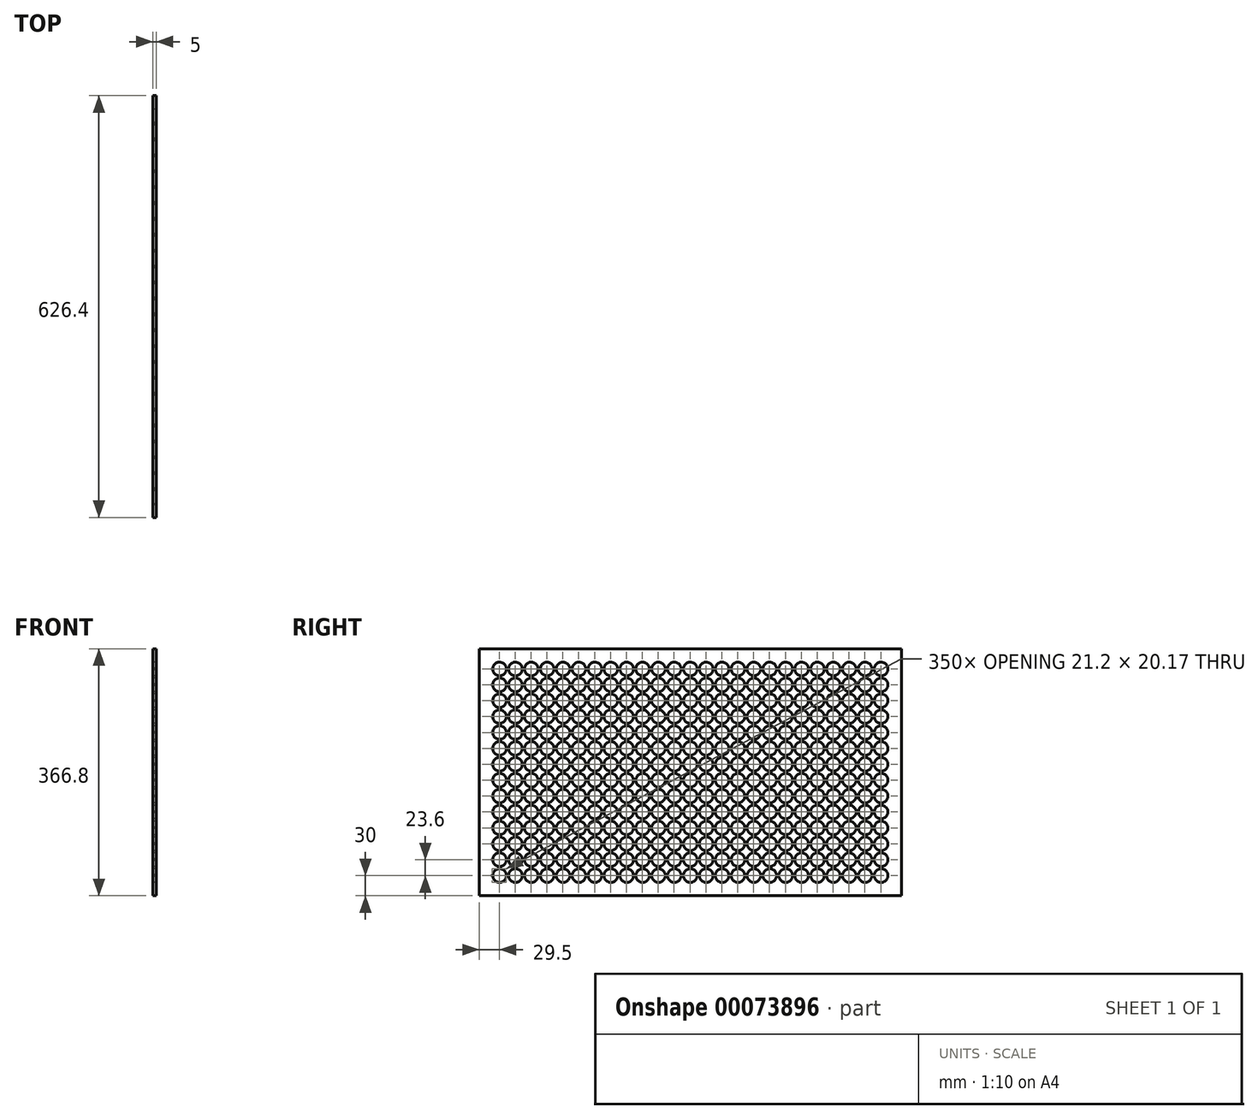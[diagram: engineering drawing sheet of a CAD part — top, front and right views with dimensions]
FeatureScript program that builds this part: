
annotation { "Feature Type Name" : "Feature", "Feature Type Description" : "" }
export const myFeature = defineFeature(function(context is Context, id is Id, definition is map)
    precondition{}
    {
        {
            var Q0;
            Q0=qCreatedBy(makeId("Right.planeOp"),FACE);
            var sketch = newSketch(context, id + "F0", { "sketchPlane" : qUnion([Q0])});
            skArc(sketch, "E0", {"start": v(-10.04, -1.1) * mm, "mid": v(10.1, 0) * mm, "end": v(-10.04, 1.1) * mm});
            skLineSegment(sketch, "E1.bottom", {"start": v(-30, 30) * mm, "end": v(596.4, 30) * mm});
            skLineSegment(sketch, "E1.top", {"start": v(-30, -336.8) * mm, "end": v(596.4, -336.8) * mm});
            skLineSegment(sketch, "E1.left", {"start": v(-30, 30) * mm, "end": v(-30, -336.8) * mm});
            skLineSegment(sketch, "E1.right", {"start": v(596.4, 30) * mm, "end": v(596.4, -336.8) * mm});
            skLineSegment(sketch, "E2", {"start": v(-10.04, -1.1) * mm, "end": v(-11.1, -1.1) * mm});
            skLineSegment(sketch, "E3", {"start": v(-10.04, 1.1) * mm, "end": v(-11.1, 1.1) * mm});
            skLineSegment(sketch, "E4", {"start": v(-11.1, 1.1) * mm, "end": v(-11.1, -1.1) * mm});
            skCircle(sketch, "E5", {"center": v(0, 0) * mm, "radius": 11.65 * mm, "construction": true});
            skArc(sketch, "E6.0.1.0", {"start": v(-10.04, -24.7) * mm, "mid": v(10.1, -23.6) * mm, "end": v(-10.04, -22.5) * mm});
            skLineSegment(sketch, "E6.0.1.1", {"start": v(-10.04, -24.7) * mm, "end": v(-11.1, -24.7) * mm});
            skLineSegment(sketch, "E6.0.1.2", {"start": v(-10.04, -22.5) * mm, "end": v(-11.1, -22.5) * mm});
            skLineSegment(sketch, "E6.0.1.3", {"start": v(-11.1, -22.5) * mm, "end": v(-11.1, -24.7) * mm});
            skArc(sketch, "E6.0.2.0", {"start": v(-10.04, -48.3) * mm, "mid": v(10.1, -47.2) * mm, "end": v(-10.04, -46.1) * mm});
            skLineSegment(sketch, "E6.0.2.1", {"start": v(-10.04, -48.3) * mm, "end": v(-11.1, -48.3) * mm});
            skLineSegment(sketch, "E6.0.2.2", {"start": v(-10.04, -46.1) * mm, "end": v(-11.1, -46.1) * mm});
            skLineSegment(sketch, "E6.0.2.3", {"start": v(-11.1, -46.1) * mm, "end": v(-11.1, -48.3) * mm});
            skArc(sketch, "E6.0.3.0", {"start": v(-10.04, -71.9) * mm, "mid": v(10.1, -70.8) * mm, "end": v(-10.04, -69.7) * mm});
            skLineSegment(sketch, "E6.0.3.1", {"start": v(-10.04, -71.9) * mm, "end": v(-11.1, -71.9) * mm});
            skLineSegment(sketch, "E6.0.3.2", {"start": v(-10.04, -69.7) * mm, "end": v(-11.1, -69.7) * mm});
            skLineSegment(sketch, "E6.0.3.3", {"start": v(-11.1, -69.7) * mm, "end": v(-11.1, -71.9) * mm});
            skArc(sketch, "E6.0.4.0", {"start": v(-10.04, -95.5) * mm, "mid": v(10.1, -94.4) * mm, "end": v(-10.04, -93.3) * mm});
            skLineSegment(sketch, "E6.0.4.1", {"start": v(-10.04, -95.5) * mm, "end": v(-11.1, -95.5) * mm});
            skLineSegment(sketch, "E6.0.4.2", {"start": v(-10.04, -93.3) * mm, "end": v(-11.1, -93.3) * mm});
            skLineSegment(sketch, "E6.0.4.3", {"start": v(-11.1, -93.3) * mm, "end": v(-11.1, -95.5) * mm});
            skArc(sketch, "E6.0.5.0", {"start": v(-10.04, -119.1) * mm, "mid": v(10.1, -118) * mm, "end": v(-10.04, -116.9) * mm});
            skLineSegment(sketch, "E6.0.5.1", {"start": v(-10.04, -119.1) * mm, "end": v(-11.1, -119.1) * mm});
            skLineSegment(sketch, "E6.0.5.2", {"start": v(-10.04, -116.9) * mm, "end": v(-11.1, -116.9) * mm});
            skLineSegment(sketch, "E6.0.5.3", {"start": v(-11.1, -116.9) * mm, "end": v(-11.1, -119.1) * mm});
            skArc(sketch, "E6.0.6.0", {"start": v(-10.04, -142.7) * mm, "mid": v(10.1, -141.6) * mm, "end": v(-10.04, -140.5) * mm});
            skLineSegment(sketch, "E6.0.6.1", {"start": v(-10.04, -142.7) * mm, "end": v(-11.1, -142.7) * mm});
            skLineSegment(sketch, "E6.0.6.2", {"start": v(-10.04, -140.5) * mm, "end": v(-11.1, -140.5) * mm});
            skLineSegment(sketch, "E6.0.6.3", {"start": v(-11.1, -140.5) * mm, "end": v(-11.1, -142.7) * mm});
            skArc(sketch, "E6.0.7.0", {"start": v(-10.04, -166.3) * mm, "mid": v(10.1, -165.2) * mm, "end": v(-10.04, -164.1) * mm});
            skLineSegment(sketch, "E6.0.7.1", {"start": v(-10.04, -166.3) * mm, "end": v(-11.1, -166.3) * mm});
            skLineSegment(sketch, "E6.0.7.2", {"start": v(-10.04, -164.1) * mm, "end": v(-11.1, -164.1) * mm});
            skLineSegment(sketch, "E6.0.7.3", {"start": v(-11.1, -164.1) * mm, "end": v(-11.1, -166.3) * mm});
            skArc(sketch, "E6.0.8.0", {"start": v(-10.04, -189.9) * mm, "mid": v(10.1, -188.8) * mm, "end": v(-10.04, -187.7) * mm});
            skLineSegment(sketch, "E6.0.8.1", {"start": v(-10.04, -189.9) * mm, "end": v(-11.1, -189.9) * mm});
            skLineSegment(sketch, "E6.0.8.2", {"start": v(-10.04, -187.7) * mm, "end": v(-11.1, -187.7) * mm});
            skLineSegment(sketch, "E6.0.8.3", {"start": v(-11.1, -187.7) * mm, "end": v(-11.1, -189.9) * mm});
            skArc(sketch, "E6.0.9.0", {"start": v(-10.04, -213.5) * mm, "mid": v(10.1, -212.4) * mm, "end": v(-10.04, -211.3) * mm});
            skLineSegment(sketch, "E6.0.9.1", {"start": v(-10.04, -213.5) * mm, "end": v(-11.1, -213.5) * mm});
            skLineSegment(sketch, "E6.0.9.2", {"start": v(-10.04, -211.3) * mm, "end": v(-11.1, -211.3) * mm});
            skLineSegment(sketch, "E6.0.9.3", {"start": v(-11.1, -211.3) * mm, "end": v(-11.1, -213.5) * mm});
            skArc(sketch, "E6.0.10.0", {"start": v(-10.04, -237.1) * mm, "mid": v(10.1, -236) * mm, "end": v(-10.04, -234.9) * mm});
            skLineSegment(sketch, "E6.0.10.1", {"start": v(-10.04, -237.1) * mm, "end": v(-11.1, -237.1) * mm});
            skLineSegment(sketch, "E6.0.10.2", {"start": v(-10.04, -234.9) * mm, "end": v(-11.1, -234.9) * mm});
            skLineSegment(sketch, "E6.0.10.3", {"start": v(-11.1, -234.9) * mm, "end": v(-11.1, -237.1) * mm});
            skArc(sketch, "E6.0.11.0", {"start": v(-10.04, -260.7) * mm, "mid": v(10.1, -259.6) * mm, "end": v(-10.04, -258.5) * mm});
            skLineSegment(sketch, "E6.0.11.1", {"start": v(-10.04, -260.7) * mm, "end": v(-11.1, -260.7) * mm});
            skLineSegment(sketch, "E6.0.11.2", {"start": v(-10.04, -258.5) * mm, "end": v(-11.1, -258.5) * mm});
            skLineSegment(sketch, "E6.0.11.3", {"start": v(-11.1, -258.5) * mm, "end": v(-11.1, -260.7) * mm});
            skArc(sketch, "E6.0.12.0", {"start": v(-10.04, -284.3) * mm, "mid": v(10.1, -283.2) * mm, "end": v(-10.04, -282.1) * mm});
            skLineSegment(sketch, "E6.0.12.1", {"start": v(-10.04, -284.3) * mm, "end": v(-11.1, -284.3) * mm});
            skLineSegment(sketch, "E6.0.12.2", {"start": v(-10.04, -282.1) * mm, "end": v(-11.1, -282.1) * mm});
            skLineSegment(sketch, "E6.0.12.3", {"start": v(-11.1, -282.1) * mm, "end": v(-11.1, -284.3) * mm});
            skArc(sketch, "E6.0.13.0", {"start": v(-10.04, -307.9) * mm, "mid": v(10.1, -306.8) * mm, "end": v(-10.04, -305.7) * mm});
            skLineSegment(sketch, "E6.0.13.1", {"start": v(-10.04, -307.9) * mm, "end": v(-11.1, -307.9) * mm});
            skLineSegment(sketch, "E6.0.13.2", {"start": v(-10.04, -305.7) * mm, "end": v(-11.1, -305.7) * mm});
            skLineSegment(sketch, "E6.0.13.3", {"start": v(-11.1, -305.7) * mm, "end": v(-11.1, -307.9) * mm});
            skArc(sketch, "E6.1.0.0", {"start": v(13.56, -1.1) * mm, "mid": v(33.7, 0) * mm, "end": v(13.56, 1.1) * mm});
            skLineSegment(sketch, "E6.1.0.1", {"start": v(13.56, -1.1) * mm, "end": v(12.5, -1.1) * mm});
            skLineSegment(sketch, "E6.1.0.2", {"start": v(13.56, 1.1) * mm, "end": v(12.5, 1.1) * mm});
            skLineSegment(sketch, "E6.1.0.3", {"start": v(12.5, 1.1) * mm, "end": v(12.5, -1.1) * mm});
            skArc(sketch, "E6.1.1.0", {"start": v(13.56, -24.7) * mm, "mid": v(33.7, -23.6) * mm, "end": v(13.56, -22.5) * mm});
            skLineSegment(sketch, "E6.1.1.1", {"start": v(13.56, -24.7) * mm, "end": v(12.5, -24.7) * mm});
            skLineSegment(sketch, "E6.1.1.2", {"start": v(13.56, -22.5) * mm, "end": v(12.5, -22.5) * mm});
            skLineSegment(sketch, "E6.1.1.3", {"start": v(12.5, -22.5) * mm, "end": v(12.5, -24.7) * mm});
            skArc(sketch, "E6.1.2.0", {"start": v(13.56, -48.3) * mm, "mid": v(33.7, -47.2) * mm, "end": v(13.56, -46.1) * mm});
            skLineSegment(sketch, "E6.1.2.1", {"start": v(13.56, -48.3) * mm, "end": v(12.5, -48.3) * mm});
            skLineSegment(sketch, "E6.1.2.2", {"start": v(13.56, -46.1) * mm, "end": v(12.5, -46.1) * mm});
            skLineSegment(sketch, "E6.1.2.3", {"start": v(12.5, -46.1) * mm, "end": v(12.5, -48.3) * mm});
            skArc(sketch, "E6.1.3.0", {"start": v(13.56, -71.9) * mm, "mid": v(33.7, -70.8) * mm, "end": v(13.56, -69.7) * mm});
            skLineSegment(sketch, "E6.1.3.1", {"start": v(13.56, -71.9) * mm, "end": v(12.5, -71.9) * mm});
            skLineSegment(sketch, "E6.1.3.2", {"start": v(13.56, -69.7) * mm, "end": v(12.5, -69.7) * mm});
            skLineSegment(sketch, "E6.1.3.3", {"start": v(12.5, -69.7) * mm, "end": v(12.5, -71.9) * mm});
            skArc(sketch, "E6.1.4.0", {"start": v(13.56, -95.5) * mm, "mid": v(33.7, -94.4) * mm, "end": v(13.56, -93.3) * mm});
            skLineSegment(sketch, "E6.1.4.1", {"start": v(13.56, -95.5) * mm, "end": v(12.5, -95.5) * mm});
            skLineSegment(sketch, "E6.1.4.2", {"start": v(13.56, -93.3) * mm, "end": v(12.5, -93.3) * mm});
            skLineSegment(sketch, "E6.1.4.3", {"start": v(12.5, -93.3) * mm, "end": v(12.5, -95.5) * mm});
            skArc(sketch, "E6.1.5.0", {"start": v(13.56, -119.1) * mm, "mid": v(33.7, -118) * mm, "end": v(13.56, -116.9) * mm});
            skLineSegment(sketch, "E6.1.5.1", {"start": v(13.56, -119.1) * mm, "end": v(12.5, -119.1) * mm});
            skLineSegment(sketch, "E6.1.5.2", {"start": v(13.56, -116.9) * mm, "end": v(12.5, -116.9) * mm});
            skLineSegment(sketch, "E6.1.5.3", {"start": v(12.5, -116.9) * mm, "end": v(12.5, -119.1) * mm});
            skArc(sketch, "E6.1.6.0", {"start": v(13.56, -142.7) * mm, "mid": v(33.7, -141.6) * mm, "end": v(13.56, -140.5) * mm});
            skLineSegment(sketch, "E6.1.6.1", {"start": v(13.56, -142.7) * mm, "end": v(12.5, -142.7) * mm});
            skLineSegment(sketch, "E6.1.6.2", {"start": v(13.56, -140.5) * mm, "end": v(12.5, -140.5) * mm});
            skLineSegment(sketch, "E6.1.6.3", {"start": v(12.5, -140.5) * mm, "end": v(12.5, -142.7) * mm});
            skArc(sketch, "E6.1.7.0", {"start": v(13.56, -166.3) * mm, "mid": v(33.7, -165.2) * mm, "end": v(13.56, -164.1) * mm});
            skLineSegment(sketch, "E6.1.7.1", {"start": v(13.56, -166.3) * mm, "end": v(12.5, -166.3) * mm});
            skLineSegment(sketch, "E6.1.7.2", {"start": v(13.56, -164.1) * mm, "end": v(12.5, -164.1) * mm});
            skLineSegment(sketch, "E6.1.7.3", {"start": v(12.5, -164.1) * mm, "end": v(12.5, -166.3) * mm});
            skArc(sketch, "E6.1.8.0", {"start": v(13.56, -189.9) * mm, "mid": v(33.7, -188.8) * mm, "end": v(13.56, -187.7) * mm});
            skLineSegment(sketch, "E6.1.8.1", {"start": v(13.56, -189.9) * mm, "end": v(12.5, -189.9) * mm});
            skLineSegment(sketch, "E6.1.8.2", {"start": v(13.56, -187.7) * mm, "end": v(12.5, -187.7) * mm});
            skLineSegment(sketch, "E6.1.8.3", {"start": v(12.5, -187.7) * mm, "end": v(12.5, -189.9) * mm});
            skArc(sketch, "E6.1.9.0", {"start": v(13.56, -213.5) * mm, "mid": v(33.7, -212.4) * mm, "end": v(13.56, -211.3) * mm});
            skLineSegment(sketch, "E6.1.9.1", {"start": v(13.56, -213.5) * mm, "end": v(12.5, -213.5) * mm});
            skLineSegment(sketch, "E6.1.9.2", {"start": v(13.56, -211.3) * mm, "end": v(12.5, -211.3) * mm});
            skLineSegment(sketch, "E6.1.9.3", {"start": v(12.5, -211.3) * mm, "end": v(12.5, -213.5) * mm});
            skArc(sketch, "E6.1.10.0", {"start": v(13.56, -237.1) * mm, "mid": v(33.7, -236) * mm, "end": v(13.56, -234.9) * mm});
            skLineSegment(sketch, "E6.1.10.1", {"start": v(13.56, -237.1) * mm, "end": v(12.5, -237.1) * mm});
            skLineSegment(sketch, "E6.1.10.2", {"start": v(13.56, -234.9) * mm, "end": v(12.5, -234.9) * mm});
            skLineSegment(sketch, "E6.1.10.3", {"start": v(12.5, -234.9) * mm, "end": v(12.5, -237.1) * mm});
            skArc(sketch, "E6.1.11.0", {"start": v(13.56, -260.7) * mm, "mid": v(33.7, -259.6) * mm, "end": v(13.56, -258.5) * mm});
            skLineSegment(sketch, "E6.1.11.1", {"start": v(13.56, -260.7) * mm, "end": v(12.5, -260.7) * mm});
            skLineSegment(sketch, "E6.1.11.2", {"start": v(13.56, -258.5) * mm, "end": v(12.5, -258.5) * mm});
            skLineSegment(sketch, "E6.1.11.3", {"start": v(12.5, -258.5) * mm, "end": v(12.5, -260.7) * mm});
            skArc(sketch, "E6.1.12.0", {"start": v(13.56, -284.3) * mm, "mid": v(33.7, -283.2) * mm, "end": v(13.56, -282.1) * mm});
            skLineSegment(sketch, "E6.1.12.1", {"start": v(13.56, -284.3) * mm, "end": v(12.5, -284.3) * mm});
            skLineSegment(sketch, "E6.1.12.2", {"start": v(13.56, -282.1) * mm, "end": v(12.5, -282.1) * mm});
            skLineSegment(sketch, "E6.1.12.3", {"start": v(12.5, -282.1) * mm, "end": v(12.5, -284.3) * mm});
            skArc(sketch, "E6.1.13.0", {"start": v(13.56, -307.9) * mm, "mid": v(33.7, -306.8) * mm, "end": v(13.56, -305.7) * mm});
            skLineSegment(sketch, "E6.1.13.1", {"start": v(13.56, -307.9) * mm, "end": v(12.5, -307.9) * mm});
            skLineSegment(sketch, "E6.1.13.2", {"start": v(13.56, -305.7) * mm, "end": v(12.5, -305.7) * mm});
            skLineSegment(sketch, "E6.1.13.3", {"start": v(12.5, -305.7) * mm, "end": v(12.5, -307.9) * mm});
            skArc(sketch, "E6.2.0.0", {"start": v(37.16, -1.1) * mm, "mid": v(57.3, 0) * mm, "end": v(37.16, 1.1) * mm});
            skLineSegment(sketch, "E6.2.0.1", {"start": v(37.16, -1.1) * mm, "end": v(36.1, -1.1) * mm});
            skLineSegment(sketch, "E6.2.0.2", {"start": v(37.16, 1.1) * mm, "end": v(36.1, 1.1) * mm});
            skLineSegment(sketch, "E6.2.0.3", {"start": v(36.1, 1.1) * mm, "end": v(36.1, -1.1) * mm});
            skArc(sketch, "E6.2.1.0", {"start": v(37.16, -24.7) * mm, "mid": v(57.3, -23.6) * mm, "end": v(37.16, -22.5) * mm});
            skLineSegment(sketch, "E6.2.1.1", {"start": v(37.16, -24.7) * mm, "end": v(36.1, -24.7) * mm});
            skLineSegment(sketch, "E6.2.1.2", {"start": v(37.16, -22.5) * mm, "end": v(36.1, -22.5) * mm});
            skLineSegment(sketch, "E6.2.1.3", {"start": v(36.1, -22.5) * mm, "end": v(36.1, -24.7) * mm});
            skArc(sketch, "E6.2.2.0", {"start": v(37.16, -48.3) * mm, "mid": v(57.3, -47.2) * mm, "end": v(37.16, -46.1) * mm});
            skLineSegment(sketch, "E6.2.2.1", {"start": v(37.16, -48.3) * mm, "end": v(36.1, -48.3) * mm});
            skLineSegment(sketch, "E6.2.2.2", {"start": v(37.16, -46.1) * mm, "end": v(36.1, -46.1) * mm});
            skLineSegment(sketch, "E6.2.2.3", {"start": v(36.1, -46.1) * mm, "end": v(36.1, -48.3) * mm});
            skArc(sketch, "E6.2.3.0", {"start": v(37.16, -71.9) * mm, "mid": v(57.3, -70.8) * mm, "end": v(37.16, -69.7) * mm});
            skLineSegment(sketch, "E6.2.3.1", {"start": v(37.16, -71.9) * mm, "end": v(36.1, -71.9) * mm});
            skLineSegment(sketch, "E6.2.3.2", {"start": v(37.16, -69.7) * mm, "end": v(36.1, -69.7) * mm});
            skLineSegment(sketch, "E6.2.3.3", {"start": v(36.1, -69.7) * mm, "end": v(36.1, -71.9) * mm});
            skArc(sketch, "E6.2.4.0", {"start": v(37.16, -95.5) * mm, "mid": v(57.3, -94.4) * mm, "end": v(37.16, -93.3) * mm});
            skLineSegment(sketch, "E6.2.4.1", {"start": v(37.16, -95.5) * mm, "end": v(36.1, -95.5) * mm});
            skLineSegment(sketch, "E6.2.4.2", {"start": v(37.16, -93.3) * mm, "end": v(36.1, -93.3) * mm});
            skLineSegment(sketch, "E6.2.4.3", {"start": v(36.1, -93.3) * mm, "end": v(36.1, -95.5) * mm});
            skArc(sketch, "E6.2.5.0", {"start": v(37.16, -119.1) * mm, "mid": v(57.3, -118) * mm, "end": v(37.16, -116.9) * mm});
            skLineSegment(sketch, "E6.2.5.1", {"start": v(37.16, -119.1) * mm, "end": v(36.1, -119.1) * mm});
            skLineSegment(sketch, "E6.2.5.2", {"start": v(37.16, -116.9) * mm, "end": v(36.1, -116.9) * mm});
            skLineSegment(sketch, "E6.2.5.3", {"start": v(36.1, -116.9) * mm, "end": v(36.1, -119.1) * mm});
            skArc(sketch, "E6.2.6.0", {"start": v(37.16, -142.7) * mm, "mid": v(57.3, -141.6) * mm, "end": v(37.16, -140.5) * mm});
            skLineSegment(sketch, "E6.2.6.1", {"start": v(37.16, -142.7) * mm, "end": v(36.1, -142.7) * mm});
            skLineSegment(sketch, "E6.2.6.2", {"start": v(37.16, -140.5) * mm, "end": v(36.1, -140.5) * mm});
            skLineSegment(sketch, "E6.2.6.3", {"start": v(36.1, -140.5) * mm, "end": v(36.1, -142.7) * mm});
            skArc(sketch, "E6.2.7.0", {"start": v(37.16, -166.3) * mm, "mid": v(57.3, -165.2) * mm, "end": v(37.16, -164.1) * mm});
            skLineSegment(sketch, "E6.2.7.1", {"start": v(37.16, -166.3) * mm, "end": v(36.1, -166.3) * mm});
            skLineSegment(sketch, "E6.2.7.2", {"start": v(37.16, -164.1) * mm, "end": v(36.1, -164.1) * mm});
            skLineSegment(sketch, "E6.2.7.3", {"start": v(36.1, -164.1) * mm, "end": v(36.1, -166.3) * mm});
            skArc(sketch, "E6.2.8.0", {"start": v(37.16, -189.9) * mm, "mid": v(57.3, -188.8) * mm, "end": v(37.16, -187.7) * mm});
            skLineSegment(sketch, "E6.2.8.1", {"start": v(37.16, -189.9) * mm, "end": v(36.1, -189.9) * mm});
            skLineSegment(sketch, "E6.2.8.2", {"start": v(37.16, -187.7) * mm, "end": v(36.1, -187.7) * mm});
            skLineSegment(sketch, "E6.2.8.3", {"start": v(36.1, -187.7) * mm, "end": v(36.1, -189.9) * mm});
            skArc(sketch, "E6.2.9.0", {"start": v(37.16, -213.5) * mm, "mid": v(57.3, -212.4) * mm, "end": v(37.16, -211.3) * mm});
            skLineSegment(sketch, "E6.2.9.1", {"start": v(37.16, -213.5) * mm, "end": v(36.1, -213.5) * mm});
            skLineSegment(sketch, "E6.2.9.2", {"start": v(37.16, -211.3) * mm, "end": v(36.1, -211.3) * mm});
            skLineSegment(sketch, "E6.2.9.3", {"start": v(36.1, -211.3) * mm, "end": v(36.1, -213.5) * mm});
            skArc(sketch, "E6.2.10.0", {"start": v(37.16, -237.1) * mm, "mid": v(57.3, -236) * mm, "end": v(37.16, -234.9) * mm});
            skLineSegment(sketch, "E6.2.10.1", {"start": v(37.16, -237.1) * mm, "end": v(36.1, -237.1) * mm});
            skLineSegment(sketch, "E6.2.10.2", {"start": v(37.16, -234.9) * mm, "end": v(36.1, -234.9) * mm});
            skLineSegment(sketch, "E6.2.10.3", {"start": v(36.1, -234.9) * mm, "end": v(36.1, -237.1) * mm});
            skArc(sketch, "E6.2.11.0", {"start": v(37.16, -260.7) * mm, "mid": v(57.3, -259.6) * mm, "end": v(37.16, -258.5) * mm});
            skLineSegment(sketch, "E6.2.11.1", {"start": v(37.16, -260.7) * mm, "end": v(36.1, -260.7) * mm});
            skLineSegment(sketch, "E6.2.11.2", {"start": v(37.16, -258.5) * mm, "end": v(36.1, -258.5) * mm});
            skLineSegment(sketch, "E6.2.11.3", {"start": v(36.1, -258.5) * mm, "end": v(36.1, -260.7) * mm});
            skArc(sketch, "E6.2.12.0", {"start": v(37.16, -284.3) * mm, "mid": v(57.3, -283.2) * mm, "end": v(37.16, -282.1) * mm});
            skLineSegment(sketch, "E6.2.12.1", {"start": v(37.16, -284.3) * mm, "end": v(36.1, -284.3) * mm});
            skLineSegment(sketch, "E6.2.12.2", {"start": v(37.16, -282.1) * mm, "end": v(36.1, -282.1) * mm});
            skLineSegment(sketch, "E6.2.12.3", {"start": v(36.1, -282.1) * mm, "end": v(36.1, -284.3) * mm});
            skArc(sketch, "E6.2.13.0", {"start": v(37.16, -307.9) * mm, "mid": v(57.3, -306.8) * mm, "end": v(37.16, -305.7) * mm});
            skLineSegment(sketch, "E6.2.13.1", {"start": v(37.16, -307.9) * mm, "end": v(36.1, -307.9) * mm});
            skLineSegment(sketch, "E6.2.13.2", {"start": v(37.16, -305.7) * mm, "end": v(36.1, -305.7) * mm});
            skLineSegment(sketch, "E6.2.13.3", {"start": v(36.1, -305.7) * mm, "end": v(36.1, -307.9) * mm});
            skArc(sketch, "E6.3.0.0", {"start": v(60.76, -1.1) * mm, "mid": v(80.9, 0) * mm, "end": v(60.76, 1.1) * mm});
            skLineSegment(sketch, "E6.3.0.1", {"start": v(60.76, -1.1) * mm, "end": v(59.7, -1.1) * mm});
            skLineSegment(sketch, "E6.3.0.2", {"start": v(60.76, 1.1) * mm, "end": v(59.7, 1.1) * mm});
            skLineSegment(sketch, "E6.3.0.3", {"start": v(59.7, 1.1) * mm, "end": v(59.7, -1.1) * mm});
            skArc(sketch, "E6.3.1.0", {"start": v(60.76, -24.7) * mm, "mid": v(80.9, -23.6) * mm, "end": v(60.76, -22.5) * mm});
            skLineSegment(sketch, "E6.3.1.1", {"start": v(60.76, -24.7) * mm, "end": v(59.7, -24.7) * mm});
            skLineSegment(sketch, "E6.3.1.2", {"start": v(60.76, -22.5) * mm, "end": v(59.7, -22.5) * mm});
            skLineSegment(sketch, "E6.3.1.3", {"start": v(59.7, -22.5) * mm, "end": v(59.7, -24.7) * mm});
            skArc(sketch, "E6.3.2.0", {"start": v(60.76, -48.3) * mm, "mid": v(80.9, -47.2) * mm, "end": v(60.76, -46.1) * mm});
            skLineSegment(sketch, "E6.3.2.1", {"start": v(60.76, -48.3) * mm, "end": v(59.7, -48.3) * mm});
            skLineSegment(sketch, "E6.3.2.2", {"start": v(60.76, -46.1) * mm, "end": v(59.7, -46.1) * mm});
            skLineSegment(sketch, "E6.3.2.3", {"start": v(59.7, -46.1) * mm, "end": v(59.7, -48.3) * mm});
            skArc(sketch, "E6.3.3.0", {"start": v(60.76, -71.9) * mm, "mid": v(80.9, -70.8) * mm, "end": v(60.76, -69.7) * mm});
            skLineSegment(sketch, "E6.3.3.1", {"start": v(60.76, -71.9) * mm, "end": v(59.7, -71.9) * mm});
            skLineSegment(sketch, "E6.3.3.2", {"start": v(60.76, -69.7) * mm, "end": v(59.7, -69.7) * mm});
            skLineSegment(sketch, "E6.3.3.3", {"start": v(59.7, -69.7) * mm, "end": v(59.7, -71.9) * mm});
            skArc(sketch, "E6.3.4.0", {"start": v(60.76, -95.5) * mm, "mid": v(80.9, -94.4) * mm, "end": v(60.76, -93.3) * mm});
            skLineSegment(sketch, "E6.3.4.1", {"start": v(60.76, -95.5) * mm, "end": v(59.7, -95.5) * mm});
            skLineSegment(sketch, "E6.3.4.2", {"start": v(60.76, -93.3) * mm, "end": v(59.7, -93.3) * mm});
            skLineSegment(sketch, "E6.3.4.3", {"start": v(59.7, -93.3) * mm, "end": v(59.7, -95.5) * mm});
            skArc(sketch, "E6.3.5.0", {"start": v(60.76, -119.1) * mm, "mid": v(80.9, -118) * mm, "end": v(60.76, -116.9) * mm});
            skLineSegment(sketch, "E6.3.5.1", {"start": v(60.76, -119.1) * mm, "end": v(59.7, -119.1) * mm});
            skLineSegment(sketch, "E6.3.5.2", {"start": v(60.76, -116.9) * mm, "end": v(59.7, -116.9) * mm});
            skLineSegment(sketch, "E6.3.5.3", {"start": v(59.7, -116.9) * mm, "end": v(59.7, -119.1) * mm});
            skArc(sketch, "E6.3.6.0", {"start": v(60.76, -142.7) * mm, "mid": v(80.9, -141.6) * mm, "end": v(60.76, -140.5) * mm});
            skLineSegment(sketch, "E6.3.6.1", {"start": v(60.76, -142.7) * mm, "end": v(59.7, -142.7) * mm});
            skLineSegment(sketch, "E6.3.6.2", {"start": v(60.76, -140.5) * mm, "end": v(59.7, -140.5) * mm});
            skLineSegment(sketch, "E6.3.6.3", {"start": v(59.7, -140.5) * mm, "end": v(59.7, -142.7) * mm});
            skArc(sketch, "E6.3.7.0", {"start": v(60.76, -166.3) * mm, "mid": v(80.9, -165.2) * mm, "end": v(60.76, -164.1) * mm});
            skLineSegment(sketch, "E6.3.7.1", {"start": v(60.76, -166.3) * mm, "end": v(59.7, -166.3) * mm});
            skLineSegment(sketch, "E6.3.7.2", {"start": v(60.76, -164.1) * mm, "end": v(59.7, -164.1) * mm});
            skLineSegment(sketch, "E6.3.7.3", {"start": v(59.7, -164.1) * mm, "end": v(59.7, -166.3) * mm});
            skArc(sketch, "E6.3.8.0", {"start": v(60.76, -189.9) * mm, "mid": v(80.9, -188.8) * mm, "end": v(60.76, -187.7) * mm});
            skLineSegment(sketch, "E6.3.8.1", {"start": v(60.76, -189.9) * mm, "end": v(59.7, -189.9) * mm});
            skLineSegment(sketch, "E6.3.8.2", {"start": v(60.76, -187.7) * mm, "end": v(59.7, -187.7) * mm});
            skLineSegment(sketch, "E6.3.8.3", {"start": v(59.7, -187.7) * mm, "end": v(59.7, -189.9) * mm});
            skArc(sketch, "E6.3.9.0", {"start": v(60.76, -213.5) * mm, "mid": v(80.9, -212.4) * mm, "end": v(60.76, -211.3) * mm});
            skLineSegment(sketch, "E6.3.9.1", {"start": v(60.76, -213.5) * mm, "end": v(59.7, -213.5) * mm});
            skLineSegment(sketch, "E6.3.9.2", {"start": v(60.76, -211.3) * mm, "end": v(59.7, -211.3) * mm});
            skLineSegment(sketch, "E6.3.9.3", {"start": v(59.7, -211.3) * mm, "end": v(59.7, -213.5) * mm});
            skArc(sketch, "E6.3.10.0", {"start": v(60.76, -237.1) * mm, "mid": v(80.9, -236) * mm, "end": v(60.76, -234.9) * mm});
            skLineSegment(sketch, "E6.3.10.1", {"start": v(60.76, -237.1) * mm, "end": v(59.7, -237.1) * mm});
            skLineSegment(sketch, "E6.3.10.2", {"start": v(60.76, -234.9) * mm, "end": v(59.7, -234.9) * mm});
            skLineSegment(sketch, "E6.3.10.3", {"start": v(59.7, -234.9) * mm, "end": v(59.7, -237.1) * mm});
            skArc(sketch, "E6.3.11.0", {"start": v(60.76, -260.7) * mm, "mid": v(80.9, -259.6) * mm, "end": v(60.76, -258.5) * mm});
            skLineSegment(sketch, "E6.3.11.1", {"start": v(60.76, -260.7) * mm, "end": v(59.7, -260.7) * mm});
            skLineSegment(sketch, "E6.3.11.2", {"start": v(60.76, -258.5) * mm, "end": v(59.7, -258.5) * mm});
            skLineSegment(sketch, "E6.3.11.3", {"start": v(59.7, -258.5) * mm, "end": v(59.7, -260.7) * mm});
            skArc(sketch, "E6.3.12.0", {"start": v(60.76, -284.3) * mm, "mid": v(80.9, -283.2) * mm, "end": v(60.76, -282.1) * mm});
            skLineSegment(sketch, "E6.3.12.1", {"start": v(60.76, -284.3) * mm, "end": v(59.7, -284.3) * mm});
            skLineSegment(sketch, "E6.3.12.2", {"start": v(60.76, -282.1) * mm, "end": v(59.7, -282.1) * mm});
            skLineSegment(sketch, "E6.3.12.3", {"start": v(59.7, -282.1) * mm, "end": v(59.7, -284.3) * mm});
            skArc(sketch, "E6.3.13.0", {"start": v(60.76, -307.9) * mm, "mid": v(80.9, -306.8) * mm, "end": v(60.76, -305.7) * mm});
            skLineSegment(sketch, "E6.3.13.1", {"start": v(60.76, -307.9) * mm, "end": v(59.7, -307.9) * mm});
            skLineSegment(sketch, "E6.3.13.2", {"start": v(60.76, -305.7) * mm, "end": v(59.7, -305.7) * mm});
            skLineSegment(sketch, "E6.3.13.3", {"start": v(59.7, -305.7) * mm, "end": v(59.7, -307.9) * mm});
            skArc(sketch, "E6.4.0.0", {"start": v(84.36, -1.1) * mm, "mid": v(104.5, 0) * mm, "end": v(84.36, 1.1) * mm});
            skLineSegment(sketch, "E6.4.0.1", {"start": v(84.36, -1.1) * mm, "end": v(83.3, -1.1) * mm});
            skLineSegment(sketch, "E6.4.0.2", {"start": v(84.36, 1.1) * mm, "end": v(83.3, 1.1) * mm});
            skLineSegment(sketch, "E6.4.0.3", {"start": v(83.3, 1.1) * mm, "end": v(83.3, -1.1) * mm});
            skArc(sketch, "E6.4.1.0", {"start": v(84.36, -24.7) * mm, "mid": v(104.5, -23.6) * mm, "end": v(84.36, -22.5) * mm});
            skLineSegment(sketch, "E6.4.1.1", {"start": v(84.36, -24.7) * mm, "end": v(83.3, -24.7) * mm});
            skLineSegment(sketch, "E6.4.1.2", {"start": v(84.36, -22.5) * mm, "end": v(83.3, -22.5) * mm});
            skLineSegment(sketch, "E6.4.1.3", {"start": v(83.3, -22.5) * mm, "end": v(83.3, -24.7) * mm});
            skArc(sketch, "E6.4.2.0", {"start": v(84.36, -48.3) * mm, "mid": v(104.5, -47.2) * mm, "end": v(84.36, -46.1) * mm});
            skLineSegment(sketch, "E6.4.2.1", {"start": v(84.36, -48.3) * mm, "end": v(83.3, -48.3) * mm});
            skLineSegment(sketch, "E6.4.2.2", {"start": v(84.36, -46.1) * mm, "end": v(83.3, -46.1) * mm});
            skLineSegment(sketch, "E6.4.2.3", {"start": v(83.3, -46.1) * mm, "end": v(83.3, -48.3) * mm});
            skArc(sketch, "E6.4.3.0", {"start": v(84.36, -71.9) * mm, "mid": v(104.5, -70.8) * mm, "end": v(84.36, -69.7) * mm});
            skLineSegment(sketch, "E6.4.3.1", {"start": v(84.36, -71.9) * mm, "end": v(83.3, -71.9) * mm});
            skLineSegment(sketch, "E6.4.3.2", {"start": v(84.36, -69.7) * mm, "end": v(83.3, -69.7) * mm});
            skLineSegment(sketch, "E6.4.3.3", {"start": v(83.3, -69.7) * mm, "end": v(83.3, -71.9) * mm});
            skArc(sketch, "E6.4.4.0", {"start": v(84.36, -95.5) * mm, "mid": v(104.5, -94.4) * mm, "end": v(84.36, -93.3) * mm});
            skLineSegment(sketch, "E6.4.4.1", {"start": v(84.36, -95.5) * mm, "end": v(83.3, -95.5) * mm});
            skLineSegment(sketch, "E6.4.4.2", {"start": v(84.36, -93.3) * mm, "end": v(83.3, -93.3) * mm});
            skLineSegment(sketch, "E6.4.4.3", {"start": v(83.3, -93.3) * mm, "end": v(83.3, -95.5) * mm});
            skArc(sketch, "E6.4.5.0", {"start": v(84.36, -119.1) * mm, "mid": v(104.5, -118) * mm, "end": v(84.36, -116.9) * mm});
            skLineSegment(sketch, "E6.4.5.1", {"start": v(84.36, -119.1) * mm, "end": v(83.3, -119.1) * mm});
            skLineSegment(sketch, "E6.4.5.2", {"start": v(84.36, -116.9) * mm, "end": v(83.3, -116.9) * mm});
            skLineSegment(sketch, "E6.4.5.3", {"start": v(83.3, -116.9) * mm, "end": v(83.3, -119.1) * mm});
            skArc(sketch, "E6.4.6.0", {"start": v(84.36, -142.7) * mm, "mid": v(104.5, -141.6) * mm, "end": v(84.36, -140.5) * mm});
            skLineSegment(sketch, "E6.4.6.1", {"start": v(84.36, -142.7) * mm, "end": v(83.3, -142.7) * mm});
            skLineSegment(sketch, "E6.4.6.2", {"start": v(84.36, -140.5) * mm, "end": v(83.3, -140.5) * mm});
            skLineSegment(sketch, "E6.4.6.3", {"start": v(83.3, -140.5) * mm, "end": v(83.3, -142.7) * mm});
            skArc(sketch, "E6.4.7.0", {"start": v(84.36, -166.3) * mm, "mid": v(104.5, -165.2) * mm, "end": v(84.36, -164.1) * mm});
            skLineSegment(sketch, "E6.4.7.1", {"start": v(84.36, -166.3) * mm, "end": v(83.3, -166.3) * mm});
            skLineSegment(sketch, "E6.4.7.2", {"start": v(84.36, -164.1) * mm, "end": v(83.3, -164.1) * mm});
            skLineSegment(sketch, "E6.4.7.3", {"start": v(83.3, -164.1) * mm, "end": v(83.3, -166.3) * mm});
            skArc(sketch, "E6.4.8.0", {"start": v(84.36, -189.9) * mm, "mid": v(104.5, -188.8) * mm, "end": v(84.36, -187.7) * mm});
            skLineSegment(sketch, "E6.4.8.1", {"start": v(84.36, -189.9) * mm, "end": v(83.3, -189.9) * mm});
            skLineSegment(sketch, "E6.4.8.2", {"start": v(84.36, -187.7) * mm, "end": v(83.3, -187.7) * mm});
            skLineSegment(sketch, "E6.4.8.3", {"start": v(83.3, -187.7) * mm, "end": v(83.3, -189.9) * mm});
            skArc(sketch, "E6.4.9.0", {"start": v(84.36, -213.5) * mm, "mid": v(104.5, -212.4) * mm, "end": v(84.36, -211.3) * mm});
            skLineSegment(sketch, "E6.4.9.1", {"start": v(84.36, -213.5) * mm, "end": v(83.3, -213.5) * mm});
            skLineSegment(sketch, "E6.4.9.2", {"start": v(84.36, -211.3) * mm, "end": v(83.3, -211.3) * mm});
            skLineSegment(sketch, "E6.4.9.3", {"start": v(83.3, -211.3) * mm, "end": v(83.3, -213.5) * mm});
            skArc(sketch, "E6.4.10.0", {"start": v(84.36, -237.1) * mm, "mid": v(104.5, -236) * mm, "end": v(84.36, -234.9) * mm});
            skLineSegment(sketch, "E6.4.10.1", {"start": v(84.36, -237.1) * mm, "end": v(83.3, -237.1) * mm});
            skLineSegment(sketch, "E6.4.10.2", {"start": v(84.36, -234.9) * mm, "end": v(83.3, -234.9) * mm});
            skLineSegment(sketch, "E6.4.10.3", {"start": v(83.3, -234.9) * mm, "end": v(83.3, -237.1) * mm});
            skArc(sketch, "E6.4.11.0", {"start": v(84.36, -260.7) * mm, "mid": v(104.5, -259.6) * mm, "end": v(84.36, -258.5) * mm});
            skLineSegment(sketch, "E6.4.11.1", {"start": v(84.36, -260.7) * mm, "end": v(83.3, -260.7) * mm});
            skLineSegment(sketch, "E6.4.11.2", {"start": v(84.36, -258.5) * mm, "end": v(83.3, -258.5) * mm});
            skLineSegment(sketch, "E6.4.11.3", {"start": v(83.3, -258.5) * mm, "end": v(83.3, -260.7) * mm});
            skArc(sketch, "E6.4.12.0", {"start": v(84.36, -284.3) * mm, "mid": v(104.5, -283.2) * mm, "end": v(84.36, -282.1) * mm});
            skLineSegment(sketch, "E6.4.12.1", {"start": v(84.36, -284.3) * mm, "end": v(83.3, -284.3) * mm});
            skLineSegment(sketch, "E6.4.12.2", {"start": v(84.36, -282.1) * mm, "end": v(83.3, -282.1) * mm});
            skLineSegment(sketch, "E6.4.12.3", {"start": v(83.3, -282.1) * mm, "end": v(83.3, -284.3) * mm});
            skArc(sketch, "E6.4.13.0", {"start": v(84.36, -307.9) * mm, "mid": v(104.5, -306.8) * mm, "end": v(84.36, -305.7) * mm});
            skLineSegment(sketch, "E6.4.13.1", {"start": v(84.36, -307.9) * mm, "end": v(83.3, -307.9) * mm});
            skLineSegment(sketch, "E6.4.13.2", {"start": v(84.36, -305.7) * mm, "end": v(83.3, -305.7) * mm});
            skLineSegment(sketch, "E6.4.13.3", {"start": v(83.3, -305.7) * mm, "end": v(83.3, -307.9) * mm});
            skArc(sketch, "E6.5.0.0", {"start": v(107.96, -1.1) * mm, "mid": v(128.1, 0) * mm, "end": v(107.96, 1.1) * mm});
            skLineSegment(sketch, "E6.5.0.1", {"start": v(107.96, -1.1) * mm, "end": v(106.9, -1.1) * mm});
            skLineSegment(sketch, "E6.5.0.2", {"start": v(107.96, 1.1) * mm, "end": v(106.9, 1.1) * mm});
            skLineSegment(sketch, "E6.5.0.3", {"start": v(106.9, 1.1) * mm, "end": v(106.9, -1.1) * mm});
            skArc(sketch, "E6.5.1.0", {"start": v(107.96, -24.7) * mm, "mid": v(128.1, -23.6) * mm, "end": v(107.96, -22.5) * mm});
            skLineSegment(sketch, "E6.5.1.1", {"start": v(107.96, -24.7) * mm, "end": v(106.9, -24.7) * mm});
            skLineSegment(sketch, "E6.5.1.2", {"start": v(107.96, -22.5) * mm, "end": v(106.9, -22.5) * mm});
            skLineSegment(sketch, "E6.5.1.3", {"start": v(106.9, -22.5) * mm, "end": v(106.9, -24.7) * mm});
            skArc(sketch, "E6.5.2.0", {"start": v(107.96, -48.3) * mm, "mid": v(128.1, -47.2) * mm, "end": v(107.96, -46.1) * mm});
            skLineSegment(sketch, "E6.5.2.1", {"start": v(107.96, -48.3) * mm, "end": v(106.9, -48.3) * mm});
            skLineSegment(sketch, "E6.5.2.2", {"start": v(107.96, -46.1) * mm, "end": v(106.9, -46.1) * mm});
            skLineSegment(sketch, "E6.5.2.3", {"start": v(106.9, -46.1) * mm, "end": v(106.9, -48.3) * mm});
            skArc(sketch, "E6.5.3.0", {"start": v(107.96, -71.9) * mm, "mid": v(128.1, -70.8) * mm, "end": v(107.96, -69.7) * mm});
            skLineSegment(sketch, "E6.5.3.1", {"start": v(107.96, -71.9) * mm, "end": v(106.9, -71.9) * mm});
            skLineSegment(sketch, "E6.5.3.2", {"start": v(107.96, -69.7) * mm, "end": v(106.9, -69.7) * mm});
            skLineSegment(sketch, "E6.5.3.3", {"start": v(106.9, -69.7) * mm, "end": v(106.9, -71.9) * mm});
            skArc(sketch, "E6.5.4.0", {"start": v(107.96, -95.5) * mm, "mid": v(128.1, -94.4) * mm, "end": v(107.96, -93.3) * mm});
            skLineSegment(sketch, "E6.5.4.1", {"start": v(107.96, -95.5) * mm, "end": v(106.9, -95.5) * mm});
            skLineSegment(sketch, "E6.5.4.2", {"start": v(107.96, -93.3) * mm, "end": v(106.9, -93.3) * mm});
            skLineSegment(sketch, "E6.5.4.3", {"start": v(106.9, -93.3) * mm, "end": v(106.9, -95.5) * mm});
            skArc(sketch, "E6.5.5.0", {"start": v(107.96, -119.1) * mm, "mid": v(128.1, -118) * mm, "end": v(107.96, -116.9) * mm});
            skLineSegment(sketch, "E6.5.5.1", {"start": v(107.96, -119.1) * mm, "end": v(106.9, -119.1) * mm});
            skLineSegment(sketch, "E6.5.5.2", {"start": v(107.96, -116.9) * mm, "end": v(106.9, -116.9) * mm});
            skLineSegment(sketch, "E6.5.5.3", {"start": v(106.9, -116.9) * mm, "end": v(106.9, -119.1) * mm});
            skArc(sketch, "E6.5.6.0", {"start": v(107.96, -142.7) * mm, "mid": v(128.1, -141.6) * mm, "end": v(107.96, -140.5) * mm});
            skLineSegment(sketch, "E6.5.6.1", {"start": v(107.96, -142.7) * mm, "end": v(106.9, -142.7) * mm});
            skLineSegment(sketch, "E6.5.6.2", {"start": v(107.96, -140.5) * mm, "end": v(106.9, -140.5) * mm});
            skLineSegment(sketch, "E6.5.6.3", {"start": v(106.9, -140.5) * mm, "end": v(106.9, -142.7) * mm});
            skArc(sketch, "E6.5.7.0", {"start": v(107.96, -166.3) * mm, "mid": v(128.1, -165.2) * mm, "end": v(107.96, -164.1) * mm});
            skLineSegment(sketch, "E6.5.7.1", {"start": v(107.96, -166.3) * mm, "end": v(106.9, -166.3) * mm});
            skLineSegment(sketch, "E6.5.7.2", {"start": v(107.96, -164.1) * mm, "end": v(106.9, -164.1) * mm});
            skLineSegment(sketch, "E6.5.7.3", {"start": v(106.9, -164.1) * mm, "end": v(106.9, -166.3) * mm});
            skArc(sketch, "E6.5.8.0", {"start": v(107.96, -189.9) * mm, "mid": v(128.1, -188.8) * mm, "end": v(107.96, -187.7) * mm});
            skLineSegment(sketch, "E6.5.8.1", {"start": v(107.96, -189.9) * mm, "end": v(106.9, -189.9) * mm});
            skLineSegment(sketch, "E6.5.8.2", {"start": v(107.96, -187.7) * mm, "end": v(106.9, -187.7) * mm});
            skLineSegment(sketch, "E6.5.8.3", {"start": v(106.9, -187.7) * mm, "end": v(106.9, -189.9) * mm});
            skArc(sketch, "E6.5.9.0", {"start": v(107.96, -213.5) * mm, "mid": v(128.1, -212.4) * mm, "end": v(107.96, -211.3) * mm});
            skLineSegment(sketch, "E6.5.9.1", {"start": v(107.96, -213.5) * mm, "end": v(106.9, -213.5) * mm});
            skLineSegment(sketch, "E6.5.9.2", {"start": v(107.96, -211.3) * mm, "end": v(106.9, -211.3) * mm});
            skLineSegment(sketch, "E6.5.9.3", {"start": v(106.9, -211.3) * mm, "end": v(106.9, -213.5) * mm});
            skArc(sketch, "E6.5.10.0", {"start": v(107.96, -237.1) * mm, "mid": v(128.1, -236) * mm, "end": v(107.96, -234.9) * mm});
            skLineSegment(sketch, "E6.5.10.1", {"start": v(107.96, -237.1) * mm, "end": v(106.9, -237.1) * mm});
            skLineSegment(sketch, "E6.5.10.2", {"start": v(107.96, -234.9) * mm, "end": v(106.9, -234.9) * mm});
            skLineSegment(sketch, "E6.5.10.3", {"start": v(106.9, -234.9) * mm, "end": v(106.9, -237.1) * mm});
            skArc(sketch, "E6.5.11.0", {"start": v(107.96, -260.7) * mm, "mid": v(128.1, -259.6) * mm, "end": v(107.96, -258.5) * mm});
            skLineSegment(sketch, "E6.5.11.1", {"start": v(107.96, -260.7) * mm, "end": v(106.9, -260.7) * mm});
            skLineSegment(sketch, "E6.5.11.2", {"start": v(107.96, -258.5) * mm, "end": v(106.9, -258.5) * mm});
            skLineSegment(sketch, "E6.5.11.3", {"start": v(106.9, -258.5) * mm, "end": v(106.9, -260.7) * mm});
            skArc(sketch, "E6.5.12.0", {"start": v(107.96, -284.3) * mm, "mid": v(128.1, -283.2) * mm, "end": v(107.96, -282.1) * mm});
            skLineSegment(sketch, "E6.5.12.1", {"start": v(107.96, -284.3) * mm, "end": v(106.9, -284.3) * mm});
            skLineSegment(sketch, "E6.5.12.2", {"start": v(107.96, -282.1) * mm, "end": v(106.9, -282.1) * mm});
            skLineSegment(sketch, "E6.5.12.3", {"start": v(106.9, -282.1) * mm, "end": v(106.9, -284.3) * mm});
            skArc(sketch, "E6.5.13.0", {"start": v(107.96, -307.9) * mm, "mid": v(128.1, -306.8) * mm, "end": v(107.96, -305.7) * mm});
            skLineSegment(sketch, "E6.5.13.1", {"start": v(107.96, -307.9) * mm, "end": v(106.9, -307.9) * mm});
            skLineSegment(sketch, "E6.5.13.2", {"start": v(107.96, -305.7) * mm, "end": v(106.9, -305.7) * mm});
            skLineSegment(sketch, "E6.5.13.3", {"start": v(106.9, -305.7) * mm, "end": v(106.9, -307.9) * mm});
            skArc(sketch, "E6.6.0.0", {"start": v(131.56, -1.1) * mm, "mid": v(151.7, 0) * mm, "end": v(131.56, 1.1) * mm});
            skLineSegment(sketch, "E6.6.0.1", {"start": v(131.56, -1.1) * mm, "end": v(130.5, -1.1) * mm});
            skLineSegment(sketch, "E6.6.0.2", {"start": v(131.56, 1.1) * mm, "end": v(130.5, 1.1) * mm});
            skLineSegment(sketch, "E6.6.0.3", {"start": v(130.5, 1.1) * mm, "end": v(130.5, -1.1) * mm});
            skArc(sketch, "E6.6.1.0", {"start": v(131.56, -24.7) * mm, "mid": v(151.7, -23.6) * mm, "end": v(131.56, -22.5) * mm});
            skLineSegment(sketch, "E6.6.1.1", {"start": v(131.56, -24.7) * mm, "end": v(130.5, -24.7) * mm});
            skLineSegment(sketch, "E6.6.1.2", {"start": v(131.56, -22.5) * mm, "end": v(130.5, -22.5) * mm});
            skLineSegment(sketch, "E6.6.1.3", {"start": v(130.5, -22.5) * mm, "end": v(130.5, -24.7) * mm});
            skArc(sketch, "E6.6.2.0", {"start": v(131.56, -48.3) * mm, "mid": v(151.7, -47.2) * mm, "end": v(131.56, -46.1) * mm});
            skLineSegment(sketch, "E6.6.2.1", {"start": v(131.56, -48.3) * mm, "end": v(130.5, -48.3) * mm});
            skLineSegment(sketch, "E6.6.2.2", {"start": v(131.56, -46.1) * mm, "end": v(130.5, -46.1) * mm});
            skLineSegment(sketch, "E6.6.2.3", {"start": v(130.5, -46.1) * mm, "end": v(130.5, -48.3) * mm});
            skArc(sketch, "E6.6.3.0", {"start": v(131.56, -71.9) * mm, "mid": v(151.7, -70.8) * mm, "end": v(131.56, -69.7) * mm});
            skLineSegment(sketch, "E6.6.3.1", {"start": v(131.56, -71.9) * mm, "end": v(130.5, -71.9) * mm});
            skLineSegment(sketch, "E6.6.3.2", {"start": v(131.56, -69.7) * mm, "end": v(130.5, -69.7) * mm});
            skLineSegment(sketch, "E6.6.3.3", {"start": v(130.5, -69.7) * mm, "end": v(130.5, -71.9) * mm});
            skArc(sketch, "E6.6.4.0", {"start": v(131.56, -95.5) * mm, "mid": v(151.7, -94.4) * mm, "end": v(131.56, -93.3) * mm});
            skLineSegment(sketch, "E6.6.4.1", {"start": v(131.56, -95.5) * mm, "end": v(130.5, -95.5) * mm});
            skLineSegment(sketch, "E6.6.4.2", {"start": v(131.56, -93.3) * mm, "end": v(130.5, -93.3) * mm});
            skLineSegment(sketch, "E6.6.4.3", {"start": v(130.5, -93.3) * mm, "end": v(130.5, -95.5) * mm});
            skArc(sketch, "E6.6.5.0", {"start": v(131.56, -119.1) * mm, "mid": v(151.7, -118) * mm, "end": v(131.56, -116.9) * mm});
            skLineSegment(sketch, "E6.6.5.1", {"start": v(131.56, -119.1) * mm, "end": v(130.5, -119.1) * mm});
            skLineSegment(sketch, "E6.6.5.2", {"start": v(131.56, -116.9) * mm, "end": v(130.5, -116.9) * mm});
            skLineSegment(sketch, "E6.6.5.3", {"start": v(130.5, -116.9) * mm, "end": v(130.5, -119.1) * mm});
            skArc(sketch, "E6.6.6.0", {"start": v(131.56, -142.7) * mm, "mid": v(151.7, -141.6) * mm, "end": v(131.56, -140.5) * mm});
            skLineSegment(sketch, "E6.6.6.1", {"start": v(131.56, -142.7) * mm, "end": v(130.5, -142.7) * mm});
            skLineSegment(sketch, "E6.6.6.2", {"start": v(131.56, -140.5) * mm, "end": v(130.5, -140.5) * mm});
            skLineSegment(sketch, "E6.6.6.3", {"start": v(130.5, -140.5) * mm, "end": v(130.5, -142.7) * mm});
            skArc(sketch, "E6.6.7.0", {"start": v(131.56, -166.3) * mm, "mid": v(151.7, -165.2) * mm, "end": v(131.56, -164.1) * mm});
            skLineSegment(sketch, "E6.6.7.1", {"start": v(131.56, -166.3) * mm, "end": v(130.5, -166.3) * mm});
            skLineSegment(sketch, "E6.6.7.2", {"start": v(131.56, -164.1) * mm, "end": v(130.5, -164.1) * mm});
            skLineSegment(sketch, "E6.6.7.3", {"start": v(130.5, -164.1) * mm, "end": v(130.5, -166.3) * mm});
            skArc(sketch, "E6.6.8.0", {"start": v(131.56, -189.9) * mm, "mid": v(151.7, -188.8) * mm, "end": v(131.56, -187.7) * mm});
            skLineSegment(sketch, "E6.6.8.1", {"start": v(131.56, -189.9) * mm, "end": v(130.5, -189.9) * mm});
            skLineSegment(sketch, "E6.6.8.2", {"start": v(131.56, -187.7) * mm, "end": v(130.5, -187.7) * mm});
            skLineSegment(sketch, "E6.6.8.3", {"start": v(130.5, -187.7) * mm, "end": v(130.5, -189.9) * mm});
            skArc(sketch, "E6.6.9.0", {"start": v(131.56, -213.5) * mm, "mid": v(151.7, -212.4) * mm, "end": v(131.56, -211.3) * mm});
            skLineSegment(sketch, "E6.6.9.1", {"start": v(131.56, -213.5) * mm, "end": v(130.5, -213.5) * mm});
            skLineSegment(sketch, "E6.6.9.2", {"start": v(131.56, -211.3) * mm, "end": v(130.5, -211.3) * mm});
            skLineSegment(sketch, "E6.6.9.3", {"start": v(130.5, -211.3) * mm, "end": v(130.5, -213.5) * mm});
            skArc(sketch, "E6.6.10.0", {"start": v(131.56, -237.1) * mm, "mid": v(151.7, -236) * mm, "end": v(131.56, -234.9) * mm});
            skLineSegment(sketch, "E6.6.10.1", {"start": v(131.56, -237.1) * mm, "end": v(130.5, -237.1) * mm});
            skLineSegment(sketch, "E6.6.10.2", {"start": v(131.56, -234.9) * mm, "end": v(130.5, -234.9) * mm});
            skLineSegment(sketch, "E6.6.10.3", {"start": v(130.5, -234.9) * mm, "end": v(130.5, -237.1) * mm});
            skArc(sketch, "E6.6.11.0", {"start": v(131.56, -260.7) * mm, "mid": v(151.7, -259.6) * mm, "end": v(131.56, -258.5) * mm});
            skLineSegment(sketch, "E6.6.11.1", {"start": v(131.56, -260.7) * mm, "end": v(130.5, -260.7) * mm});
            skLineSegment(sketch, "E6.6.11.2", {"start": v(131.56, -258.5) * mm, "end": v(130.5, -258.5) * mm});
            skLineSegment(sketch, "E6.6.11.3", {"start": v(130.5, -258.5) * mm, "end": v(130.5, -260.7) * mm});
            skArc(sketch, "E6.6.12.0", {"start": v(131.56, -284.3) * mm, "mid": v(151.7, -283.2) * mm, "end": v(131.56, -282.1) * mm});
            skLineSegment(sketch, "E6.6.12.1", {"start": v(131.56, -284.3) * mm, "end": v(130.5, -284.3) * mm});
            skLineSegment(sketch, "E6.6.12.2", {"start": v(131.56, -282.1) * mm, "end": v(130.5, -282.1) * mm});
            skLineSegment(sketch, "E6.6.12.3", {"start": v(130.5, -282.1) * mm, "end": v(130.5, -284.3) * mm});
            skArc(sketch, "E6.6.13.0", {"start": v(131.56, -307.9) * mm, "mid": v(151.7, -306.8) * mm, "end": v(131.56, -305.7) * mm});
            skLineSegment(sketch, "E6.6.13.1", {"start": v(131.56, -307.9) * mm, "end": v(130.5, -307.9) * mm});
            skLineSegment(sketch, "E6.6.13.2", {"start": v(131.56, -305.7) * mm, "end": v(130.5, -305.7) * mm});
            skLineSegment(sketch, "E6.6.13.3", {"start": v(130.5, -305.7) * mm, "end": v(130.5, -307.9) * mm});
            skArc(sketch, "E6.7.0.0", {"start": v(155.16, -1.1) * mm, "mid": v(175.3, 0) * mm, "end": v(155.16, 1.1) * mm});
            skLineSegment(sketch, "E6.7.0.1", {"start": v(155.16, -1.1) * mm, "end": v(154.1, -1.1) * mm});
            skLineSegment(sketch, "E6.7.0.2", {"start": v(155.16, 1.1) * mm, "end": v(154.1, 1.1) * mm});
            skLineSegment(sketch, "E6.7.0.3", {"start": v(154.1, 1.1) * mm, "end": v(154.1, -1.1) * mm});
            skArc(sketch, "E6.7.1.0", {"start": v(155.16, -24.7) * mm, "mid": v(175.3, -23.6) * mm, "end": v(155.16, -22.5) * mm});
            skLineSegment(sketch, "E6.7.1.1", {"start": v(155.16, -24.7) * mm, "end": v(154.1, -24.7) * mm});
            skLineSegment(sketch, "E6.7.1.2", {"start": v(155.16, -22.5) * mm, "end": v(154.1, -22.5) * mm});
            skLineSegment(sketch, "E6.7.1.3", {"start": v(154.1, -22.5) * mm, "end": v(154.1, -24.7) * mm});
            skArc(sketch, "E6.7.2.0", {"start": v(155.16, -48.3) * mm, "mid": v(175.3, -47.2) * mm, "end": v(155.16, -46.1) * mm});
            skLineSegment(sketch, "E6.7.2.1", {"start": v(155.16, -48.3) * mm, "end": v(154.1, -48.3) * mm});
            skLineSegment(sketch, "E6.7.2.2", {"start": v(155.16, -46.1) * mm, "end": v(154.1, -46.1) * mm});
            skLineSegment(sketch, "E6.7.2.3", {"start": v(154.1, -46.1) * mm, "end": v(154.1, -48.3) * mm});
            skArc(sketch, "E6.7.3.0", {"start": v(155.16, -71.9) * mm, "mid": v(175.3, -70.8) * mm, "end": v(155.16, -69.7) * mm});
            skLineSegment(sketch, "E6.7.3.1", {"start": v(155.16, -71.9) * mm, "end": v(154.1, -71.9) * mm});
            skLineSegment(sketch, "E6.7.3.2", {"start": v(155.16, -69.7) * mm, "end": v(154.1, -69.7) * mm});
            skLineSegment(sketch, "E6.7.3.3", {"start": v(154.1, -69.7) * mm, "end": v(154.1, -71.9) * mm});
            skArc(sketch, "E6.7.4.0", {"start": v(155.16, -95.5) * mm, "mid": v(175.3, -94.4) * mm, "end": v(155.16, -93.3) * mm});
            skLineSegment(sketch, "E6.7.4.1", {"start": v(155.16, -95.5) * mm, "end": v(154.1, -95.5) * mm});
            skLineSegment(sketch, "E6.7.4.2", {"start": v(155.16, -93.3) * mm, "end": v(154.1, -93.3) * mm});
            skLineSegment(sketch, "E6.7.4.3", {"start": v(154.1, -93.3) * mm, "end": v(154.1, -95.5) * mm});
            skArc(sketch, "E6.7.5.0", {"start": v(155.16, -119.1) * mm, "mid": v(175.3, -118) * mm, "end": v(155.16, -116.9) * mm});
            skLineSegment(sketch, "E6.7.5.1", {"start": v(155.16, -119.1) * mm, "end": v(154.1, -119.1) * mm});
            skLineSegment(sketch, "E6.7.5.2", {"start": v(155.16, -116.9) * mm, "end": v(154.1, -116.9) * mm});
            skLineSegment(sketch, "E6.7.5.3", {"start": v(154.1, -116.9) * mm, "end": v(154.1, -119.1) * mm});
            skArc(sketch, "E6.7.6.0", {"start": v(155.16, -142.7) * mm, "mid": v(175.3, -141.6) * mm, "end": v(155.16, -140.5) * mm});
            skLineSegment(sketch, "E6.7.6.1", {"start": v(155.16, -142.7) * mm, "end": v(154.1, -142.7) * mm});
            skLineSegment(sketch, "E6.7.6.2", {"start": v(155.16, -140.5) * mm, "end": v(154.1, -140.5) * mm});
            skLineSegment(sketch, "E6.7.6.3", {"start": v(154.1, -140.5) * mm, "end": v(154.1, -142.7) * mm});
            skArc(sketch, "E6.7.7.0", {"start": v(155.16, -166.3) * mm, "mid": v(175.3, -165.2) * mm, "end": v(155.16, -164.1) * mm});
            skLineSegment(sketch, "E6.7.7.1", {"start": v(155.16, -166.3) * mm, "end": v(154.1, -166.3) * mm});
            skLineSegment(sketch, "E6.7.7.2", {"start": v(155.16, -164.1) * mm, "end": v(154.1, -164.1) * mm});
            skLineSegment(sketch, "E6.7.7.3", {"start": v(154.1, -164.1) * mm, "end": v(154.1, -166.3) * mm});
            skArc(sketch, "E6.7.8.0", {"start": v(155.16, -189.9) * mm, "mid": v(175.3, -188.8) * mm, "end": v(155.16, -187.7) * mm});
            skLineSegment(sketch, "E6.7.8.1", {"start": v(155.16, -189.9) * mm, "end": v(154.1, -189.9) * mm});
            skLineSegment(sketch, "E6.7.8.2", {"start": v(155.16, -187.7) * mm, "end": v(154.1, -187.7) * mm});
            skLineSegment(sketch, "E6.7.8.3", {"start": v(154.1, -187.7) * mm, "end": v(154.1, -189.9) * mm});
            skArc(sketch, "E6.7.9.0", {"start": v(155.16, -213.5) * mm, "mid": v(175.3, -212.4) * mm, "end": v(155.16, -211.3) * mm});
            skLineSegment(sketch, "E6.7.9.1", {"start": v(155.16, -213.5) * mm, "end": v(154.1, -213.5) * mm});
            skLineSegment(sketch, "E6.7.9.2", {"start": v(155.16, -211.3) * mm, "end": v(154.1, -211.3) * mm});
            skLineSegment(sketch, "E6.7.9.3", {"start": v(154.1, -211.3) * mm, "end": v(154.1, -213.5) * mm});
            skArc(sketch, "E6.7.10.0", {"start": v(155.16, -237.1) * mm, "mid": v(175.3, -236) * mm, "end": v(155.16, -234.9) * mm});
            skLineSegment(sketch, "E6.7.10.1", {"start": v(155.16, -237.1) * mm, "end": v(154.1, -237.1) * mm});
            skLineSegment(sketch, "E6.7.10.2", {"start": v(155.16, -234.9) * mm, "end": v(154.1, -234.9) * mm});
            skLineSegment(sketch, "E6.7.10.3", {"start": v(154.1, -234.9) * mm, "end": v(154.1, -237.1) * mm});
            skArc(sketch, "E6.7.11.0", {"start": v(155.16, -260.7) * mm, "mid": v(175.3, -259.6) * mm, "end": v(155.16, -258.5) * mm});
            skLineSegment(sketch, "E6.7.11.1", {"start": v(155.16, -260.7) * mm, "end": v(154.1, -260.7) * mm});
            skLineSegment(sketch, "E6.7.11.2", {"start": v(155.16, -258.5) * mm, "end": v(154.1, -258.5) * mm});
            skLineSegment(sketch, "E6.7.11.3", {"start": v(154.1, -258.5) * mm, "end": v(154.1, -260.7) * mm});
            skArc(sketch, "E6.7.12.0", {"start": v(155.16, -284.3) * mm, "mid": v(175.3, -283.2) * mm, "end": v(155.16, -282.1) * mm});
            skLineSegment(sketch, "E6.7.12.1", {"start": v(155.16, -284.3) * mm, "end": v(154.1, -284.3) * mm});
            skLineSegment(sketch, "E6.7.12.2", {"start": v(155.16, -282.1) * mm, "end": v(154.1, -282.1) * mm});
            skLineSegment(sketch, "E6.7.12.3", {"start": v(154.1, -282.1) * mm, "end": v(154.1, -284.3) * mm});
            skArc(sketch, "E6.7.13.0", {"start": v(155.16, -307.9) * mm, "mid": v(175.3, -306.8) * mm, "end": v(155.16, -305.7) * mm});
            skLineSegment(sketch, "E6.7.13.1", {"start": v(155.16, -307.9) * mm, "end": v(154.1, -307.9) * mm});
            skLineSegment(sketch, "E6.7.13.2", {"start": v(155.16, -305.7) * mm, "end": v(154.1, -305.7) * mm});
            skLineSegment(sketch, "E6.7.13.3", {"start": v(154.1, -305.7) * mm, "end": v(154.1, -307.9) * mm});
            skArc(sketch, "E6.8.0.0", {"start": v(178.76, -1.1) * mm, "mid": v(198.9, 0) * mm, "end": v(178.76, 1.1) * mm});
            skLineSegment(sketch, "E6.8.0.1", {"start": v(178.76, -1.1) * mm, "end": v(177.7, -1.1) * mm});
            skLineSegment(sketch, "E6.8.0.2", {"start": v(178.76, 1.1) * mm, "end": v(177.7, 1.1) * mm});
            skLineSegment(sketch, "E6.8.0.3", {"start": v(177.7, 1.1) * mm, "end": v(177.7, -1.1) * mm});
            skArc(sketch, "E6.8.1.0", {"start": v(178.76, -24.7) * mm, "mid": v(198.9, -23.6) * mm, "end": v(178.76, -22.5) * mm});
            skLineSegment(sketch, "E6.8.1.1", {"start": v(178.76, -24.7) * mm, "end": v(177.7, -24.7) * mm});
            skLineSegment(sketch, "E6.8.1.2", {"start": v(178.76, -22.5) * mm, "end": v(177.7, -22.5) * mm});
            skLineSegment(sketch, "E6.8.1.3", {"start": v(177.7, -22.5) * mm, "end": v(177.7, -24.7) * mm});
            skArc(sketch, "E6.8.2.0", {"start": v(178.76, -48.3) * mm, "mid": v(198.9, -47.2) * mm, "end": v(178.76, -46.1) * mm});
            skLineSegment(sketch, "E6.8.2.1", {"start": v(178.76, -48.3) * mm, "end": v(177.7, -48.3) * mm});
            skLineSegment(sketch, "E6.8.2.2", {"start": v(178.76, -46.1) * mm, "end": v(177.7, -46.1) * mm});
            skLineSegment(sketch, "E6.8.2.3", {"start": v(177.7, -46.1) * mm, "end": v(177.7, -48.3) * mm});
            skArc(sketch, "E6.8.3.0", {"start": v(178.76, -71.9) * mm, "mid": v(198.9, -70.8) * mm, "end": v(178.76, -69.7) * mm});
            skLineSegment(sketch, "E6.8.3.1", {"start": v(178.76, -71.9) * mm, "end": v(177.7, -71.9) * mm});
            skLineSegment(sketch, "E6.8.3.2", {"start": v(178.76, -69.7) * mm, "end": v(177.7, -69.7) * mm});
            skLineSegment(sketch, "E6.8.3.3", {"start": v(177.7, -69.7) * mm, "end": v(177.7, -71.9) * mm});
            skArc(sketch, "E6.8.4.0", {"start": v(178.76, -95.5) * mm, "mid": v(198.9, -94.4) * mm, "end": v(178.76, -93.3) * mm});
            skLineSegment(sketch, "E6.8.4.1", {"start": v(178.76, -95.5) * mm, "end": v(177.7, -95.5) * mm});
            skLineSegment(sketch, "E6.8.4.2", {"start": v(178.76, -93.3) * mm, "end": v(177.7, -93.3) * mm});
            skLineSegment(sketch, "E6.8.4.3", {"start": v(177.7, -93.3) * mm, "end": v(177.7, -95.5) * mm});
            skArc(sketch, "E6.8.5.0", {"start": v(178.76, -119.1) * mm, "mid": v(198.9, -118) * mm, "end": v(178.76, -116.9) * mm});
            skLineSegment(sketch, "E6.8.5.1", {"start": v(178.76, -119.1) * mm, "end": v(177.7, -119.1) * mm});
            skLineSegment(sketch, "E6.8.5.2", {"start": v(178.76, -116.9) * mm, "end": v(177.7, -116.9) * mm});
            skLineSegment(sketch, "E6.8.5.3", {"start": v(177.7, -116.9) * mm, "end": v(177.7, -119.1) * mm});
            skArc(sketch, "E6.8.6.0", {"start": v(178.76, -142.7) * mm, "mid": v(198.9, -141.6) * mm, "end": v(178.76, -140.5) * mm});
            skLineSegment(sketch, "E6.8.6.1", {"start": v(178.76, -142.7) * mm, "end": v(177.7, -142.7) * mm});
            skLineSegment(sketch, "E6.8.6.2", {"start": v(178.76, -140.5) * mm, "end": v(177.7, -140.5) * mm});
            skLineSegment(sketch, "E6.8.6.3", {"start": v(177.7, -140.5) * mm, "end": v(177.7, -142.7) * mm});
            skArc(sketch, "E6.8.7.0", {"start": v(178.76, -166.3) * mm, "mid": v(198.9, -165.2) * mm, "end": v(178.76, -164.1) * mm});
            skLineSegment(sketch, "E6.8.7.1", {"start": v(178.76, -166.3) * mm, "end": v(177.7, -166.3) * mm});
            skLineSegment(sketch, "E6.8.7.2", {"start": v(178.76, -164.1) * mm, "end": v(177.7, -164.1) * mm});
            skLineSegment(sketch, "E6.8.7.3", {"start": v(177.7, -164.1) * mm, "end": v(177.7, -166.3) * mm});
            skArc(sketch, "E6.8.8.0", {"start": v(178.76, -189.9) * mm, "mid": v(198.9, -188.8) * mm, "end": v(178.76, -187.7) * mm});
            skLineSegment(sketch, "E6.8.8.1", {"start": v(178.76, -189.9) * mm, "end": v(177.7, -189.9) * mm});
            skLineSegment(sketch, "E6.8.8.2", {"start": v(178.76, -187.7) * mm, "end": v(177.7, -187.7) * mm});
            skLineSegment(sketch, "E6.8.8.3", {"start": v(177.7, -187.7) * mm, "end": v(177.7, -189.9) * mm});
            skArc(sketch, "E6.8.9.0", {"start": v(178.76, -213.5) * mm, "mid": v(198.9, -212.4) * mm, "end": v(178.76, -211.3) * mm});
            skLineSegment(sketch, "E6.8.9.1", {"start": v(178.76, -213.5) * mm, "end": v(177.7, -213.5) * mm});
            skLineSegment(sketch, "E6.8.9.2", {"start": v(178.76, -211.3) * mm, "end": v(177.7, -211.3) * mm});
            skLineSegment(sketch, "E6.8.9.3", {"start": v(177.7, -211.3) * mm, "end": v(177.7, -213.5) * mm});
            skArc(sketch, "E6.8.10.0", {"start": v(178.76, -237.1) * mm, "mid": v(198.9, -236) * mm, "end": v(178.76, -234.9) * mm});
            skLineSegment(sketch, "E6.8.10.1", {"start": v(178.76, -237.1) * mm, "end": v(177.7, -237.1) * mm});
            skLineSegment(sketch, "E6.8.10.2", {"start": v(178.76, -234.9) * mm, "end": v(177.7, -234.9) * mm});
            skLineSegment(sketch, "E6.8.10.3", {"start": v(177.7, -234.9) * mm, "end": v(177.7, -237.1) * mm});
            skArc(sketch, "E6.8.11.0", {"start": v(178.76, -260.7) * mm, "mid": v(198.9, -259.6) * mm, "end": v(178.76, -258.5) * mm});
            skLineSegment(sketch, "E6.8.11.1", {"start": v(178.76, -260.7) * mm, "end": v(177.7, -260.7) * mm});
            skLineSegment(sketch, "E6.8.11.2", {"start": v(178.76, -258.5) * mm, "end": v(177.7, -258.5) * mm});
            skLineSegment(sketch, "E6.8.11.3", {"start": v(177.7, -258.5) * mm, "end": v(177.7, -260.7) * mm});
            skArc(sketch, "E6.8.12.0", {"start": v(178.76, -284.3) * mm, "mid": v(198.9, -283.2) * mm, "end": v(178.76, -282.1) * mm});
            skLineSegment(sketch, "E6.8.12.1", {"start": v(178.76, -284.3) * mm, "end": v(177.7, -284.3) * mm});
            skLineSegment(sketch, "E6.8.12.2", {"start": v(178.76, -282.1) * mm, "end": v(177.7, -282.1) * mm});
            skLineSegment(sketch, "E6.8.12.3", {"start": v(177.7, -282.1) * mm, "end": v(177.7, -284.3) * mm});
            skArc(sketch, "E6.8.13.0", {"start": v(178.76, -307.9) * mm, "mid": v(198.9, -306.8) * mm, "end": v(178.76, -305.7) * mm});
            skLineSegment(sketch, "E6.8.13.1", {"start": v(178.76, -307.9) * mm, "end": v(177.7, -307.9) * mm});
            skLineSegment(sketch, "E6.8.13.2", {"start": v(178.76, -305.7) * mm, "end": v(177.7, -305.7) * mm});
            skLineSegment(sketch, "E6.8.13.3", {"start": v(177.7, -305.7) * mm, "end": v(177.7, -307.9) * mm});
            skArc(sketch, "E6.9.0.0", {"start": v(202.36, -1.1) * mm, "mid": v(222.5, 0) * mm, "end": v(202.36, 1.1) * mm});
            skLineSegment(sketch, "E6.9.0.1", {"start": v(202.36, -1.1) * mm, "end": v(201.3, -1.1) * mm});
            skLineSegment(sketch, "E6.9.0.2", {"start": v(202.36, 1.1) * mm, "end": v(201.3, 1.1) * mm});
            skLineSegment(sketch, "E6.9.0.3", {"start": v(201.3, 1.1) * mm, "end": v(201.3, -1.1) * mm});
            skArc(sketch, "E6.9.1.0", {"start": v(202.36, -24.7) * mm, "mid": v(222.5, -23.6) * mm, "end": v(202.36, -22.5) * mm});
            skLineSegment(sketch, "E6.9.1.1", {"start": v(202.36, -24.7) * mm, "end": v(201.3, -24.7) * mm});
            skLineSegment(sketch, "E6.9.1.2", {"start": v(202.36, -22.5) * mm, "end": v(201.3, -22.5) * mm});
            skLineSegment(sketch, "E6.9.1.3", {"start": v(201.3, -22.5) * mm, "end": v(201.3, -24.7) * mm});
            skArc(sketch, "E6.9.2.0", {"start": v(202.36, -48.3) * mm, "mid": v(222.5, -47.2) * mm, "end": v(202.36, -46.1) * mm});
            skLineSegment(sketch, "E6.9.2.1", {"start": v(202.36, -48.3) * mm, "end": v(201.3, -48.3) * mm});
            skLineSegment(sketch, "E6.9.2.2", {"start": v(202.36, -46.1) * mm, "end": v(201.3, -46.1) * mm});
            skLineSegment(sketch, "E6.9.2.3", {"start": v(201.3, -46.1) * mm, "end": v(201.3, -48.3) * mm});
            skArc(sketch, "E6.9.3.0", {"start": v(202.36, -71.9) * mm, "mid": v(222.5, -70.8) * mm, "end": v(202.36, -69.7) * mm});
            skLineSegment(sketch, "E6.9.3.1", {"start": v(202.36, -71.9) * mm, "end": v(201.3, -71.9) * mm});
            skLineSegment(sketch, "E6.9.3.2", {"start": v(202.36, -69.7) * mm, "end": v(201.3, -69.7) * mm});
            skLineSegment(sketch, "E6.9.3.3", {"start": v(201.3, -69.7) * mm, "end": v(201.3, -71.9) * mm});
            skArc(sketch, "E6.9.4.0", {"start": v(202.36, -95.5) * mm, "mid": v(222.5, -94.4) * mm, "end": v(202.36, -93.3) * mm});
            skLineSegment(sketch, "E6.9.4.1", {"start": v(202.36, -95.5) * mm, "end": v(201.3, -95.5) * mm});
            skLineSegment(sketch, "E6.9.4.2", {"start": v(202.36, -93.3) * mm, "end": v(201.3, -93.3) * mm});
            skLineSegment(sketch, "E6.9.4.3", {"start": v(201.3, -93.3) * mm, "end": v(201.3, -95.5) * mm});
            skArc(sketch, "E6.9.5.0", {"start": v(202.36, -119.1) * mm, "mid": v(222.5, -118) * mm, "end": v(202.36, -116.9) * mm});
            skLineSegment(sketch, "E6.9.5.1", {"start": v(202.36, -119.1) * mm, "end": v(201.3, -119.1) * mm});
            skLineSegment(sketch, "E6.9.5.2", {"start": v(202.36, -116.9) * mm, "end": v(201.3, -116.9) * mm});
            skLineSegment(sketch, "E6.9.5.3", {"start": v(201.3, -116.9) * mm, "end": v(201.3, -119.1) * mm});
            skArc(sketch, "E6.9.6.0", {"start": v(202.36, -142.7) * mm, "mid": v(222.5, -141.6) * mm, "end": v(202.36, -140.5) * mm});
            skLineSegment(sketch, "E6.9.6.1", {"start": v(202.36, -142.7) * mm, "end": v(201.3, -142.7) * mm});
            skLineSegment(sketch, "E6.9.6.2", {"start": v(202.36, -140.5) * mm, "end": v(201.3, -140.5) * mm});
            skLineSegment(sketch, "E6.9.6.3", {"start": v(201.3, -140.5) * mm, "end": v(201.3, -142.7) * mm});
            skArc(sketch, "E6.9.7.0", {"start": v(202.36, -166.3) * mm, "mid": v(222.5, -165.2) * mm, "end": v(202.36, -164.1) * mm});
            skLineSegment(sketch, "E6.9.7.1", {"start": v(202.36, -166.3) * mm, "end": v(201.3, -166.3) * mm});
            skLineSegment(sketch, "E6.9.7.2", {"start": v(202.36, -164.1) * mm, "end": v(201.3, -164.1) * mm});
            skLineSegment(sketch, "E6.9.7.3", {"start": v(201.3, -164.1) * mm, "end": v(201.3, -166.3) * mm});
            skArc(sketch, "E6.9.8.0", {"start": v(202.36, -189.9) * mm, "mid": v(222.5, -188.8) * mm, "end": v(202.36, -187.7) * mm});
            skLineSegment(sketch, "E6.9.8.1", {"start": v(202.36, -189.9) * mm, "end": v(201.3, -189.9) * mm});
            skLineSegment(sketch, "E6.9.8.2", {"start": v(202.36, -187.7) * mm, "end": v(201.3, -187.7) * mm});
            skLineSegment(sketch, "E6.9.8.3", {"start": v(201.3, -187.7) * mm, "end": v(201.3, -189.9) * mm});
            skArc(sketch, "E6.9.9.0", {"start": v(202.36, -213.5) * mm, "mid": v(222.5, -212.4) * mm, "end": v(202.36, -211.3) * mm});
            skLineSegment(sketch, "E6.9.9.1", {"start": v(202.36, -213.5) * mm, "end": v(201.3, -213.5) * mm});
            skLineSegment(sketch, "E6.9.9.2", {"start": v(202.36, -211.3) * mm, "end": v(201.3, -211.3) * mm});
            skLineSegment(sketch, "E6.9.9.3", {"start": v(201.3, -211.3) * mm, "end": v(201.3, -213.5) * mm});
            skArc(sketch, "E6.9.10.0", {"start": v(202.36, -237.1) * mm, "mid": v(222.5, -236) * mm, "end": v(202.36, -234.9) * mm});
            skLineSegment(sketch, "E6.9.10.1", {"start": v(202.36, -237.1) * mm, "end": v(201.3, -237.1) * mm});
            skLineSegment(sketch, "E6.9.10.2", {"start": v(202.36, -234.9) * mm, "end": v(201.3, -234.9) * mm});
            skLineSegment(sketch, "E6.9.10.3", {"start": v(201.3, -234.9) * mm, "end": v(201.3, -237.1) * mm});
            skArc(sketch, "E6.9.11.0", {"start": v(202.36, -260.7) * mm, "mid": v(222.5, -259.6) * mm, "end": v(202.36, -258.5) * mm});
            skLineSegment(sketch, "E6.9.11.1", {"start": v(202.36, -260.7) * mm, "end": v(201.3, -260.7) * mm});
            skLineSegment(sketch, "E6.9.11.2", {"start": v(202.36, -258.5) * mm, "end": v(201.3, -258.5) * mm});
            skLineSegment(sketch, "E6.9.11.3", {"start": v(201.3, -258.5) * mm, "end": v(201.3, -260.7) * mm});
            skArc(sketch, "E6.9.12.0", {"start": v(202.36, -284.3) * mm, "mid": v(222.5, -283.2) * mm, "end": v(202.36, -282.1) * mm});
            skLineSegment(sketch, "E6.9.12.1", {"start": v(202.36, -284.3) * mm, "end": v(201.3, -284.3) * mm});
            skLineSegment(sketch, "E6.9.12.2", {"start": v(202.36, -282.1) * mm, "end": v(201.3, -282.1) * mm});
            skLineSegment(sketch, "E6.9.12.3", {"start": v(201.3, -282.1) * mm, "end": v(201.3, -284.3) * mm});
            skArc(sketch, "E6.9.13.0", {"start": v(202.36, -307.9) * mm, "mid": v(222.5, -306.8) * mm, "end": v(202.36, -305.7) * mm});
            skLineSegment(sketch, "E6.9.13.1", {"start": v(202.36, -307.9) * mm, "end": v(201.3, -307.9) * mm});
            skLineSegment(sketch, "E6.9.13.2", {"start": v(202.36, -305.7) * mm, "end": v(201.3, -305.7) * mm});
            skLineSegment(sketch, "E6.9.13.3", {"start": v(201.3, -305.7) * mm, "end": v(201.3, -307.9) * mm});
            skArc(sketch, "E6.10.0.0", {"start": v(225.96, -1.1) * mm, "mid": v(246.1, 0) * mm, "end": v(225.96, 1.1) * mm});
            skLineSegment(sketch, "E6.10.0.1", {"start": v(225.96, -1.1) * mm, "end": v(224.9, -1.1) * mm});
            skLineSegment(sketch, "E6.10.0.2", {"start": v(225.96, 1.1) * mm, "end": v(224.9, 1.1) * mm});
            skLineSegment(sketch, "E6.10.0.3", {"start": v(224.9, 1.1) * mm, "end": v(224.9, -1.1) * mm});
            skArc(sketch, "E6.10.1.0", {"start": v(225.96, -24.7) * mm, "mid": v(246.1, -23.6) * mm, "end": v(225.96, -22.5) * mm});
            skLineSegment(sketch, "E6.10.1.1", {"start": v(225.96, -24.7) * mm, "end": v(224.9, -24.7) * mm});
            skLineSegment(sketch, "E6.10.1.2", {"start": v(225.96, -22.5) * mm, "end": v(224.9, -22.5) * mm});
            skLineSegment(sketch, "E6.10.1.3", {"start": v(224.9, -22.5) * mm, "end": v(224.9, -24.7) * mm});
            skArc(sketch, "E6.10.2.0", {"start": v(225.96, -48.3) * mm, "mid": v(246.1, -47.2) * mm, "end": v(225.96, -46.1) * mm});
            skLineSegment(sketch, "E6.10.2.1", {"start": v(225.96, -48.3) * mm, "end": v(224.9, -48.3) * mm});
            skLineSegment(sketch, "E6.10.2.2", {"start": v(225.96, -46.1) * mm, "end": v(224.9, -46.1) * mm});
            skLineSegment(sketch, "E6.10.2.3", {"start": v(224.9, -46.1) * mm, "end": v(224.9, -48.3) * mm});
            skArc(sketch, "E6.10.3.0", {"start": v(225.96, -71.9) * mm, "mid": v(246.1, -70.8) * mm, "end": v(225.96, -69.7) * mm});
            skLineSegment(sketch, "E6.10.3.1", {"start": v(225.96, -71.9) * mm, "end": v(224.9, -71.9) * mm});
            skLineSegment(sketch, "E6.10.3.2", {"start": v(225.96, -69.7) * mm, "end": v(224.9, -69.7) * mm});
            skLineSegment(sketch, "E6.10.3.3", {"start": v(224.9, -69.7) * mm, "end": v(224.9, -71.9) * mm});
            skArc(sketch, "E6.10.4.0", {"start": v(225.96, -95.5) * mm, "mid": v(246.1, -94.4) * mm, "end": v(225.96, -93.3) * mm});
            skLineSegment(sketch, "E6.10.4.1", {"start": v(225.96, -95.5) * mm, "end": v(224.9, -95.5) * mm});
            skLineSegment(sketch, "E6.10.4.2", {"start": v(225.96, -93.3) * mm, "end": v(224.9, -93.3) * mm});
            skLineSegment(sketch, "E6.10.4.3", {"start": v(224.9, -93.3) * mm, "end": v(224.9, -95.5) * mm});
            skArc(sketch, "E6.10.5.0", {"start": v(225.96, -119.1) * mm, "mid": v(246.1, -118) * mm, "end": v(225.96, -116.9) * mm});
            skLineSegment(sketch, "E6.10.5.1", {"start": v(225.96, -119.1) * mm, "end": v(224.9, -119.1) * mm});
            skLineSegment(sketch, "E6.10.5.2", {"start": v(225.96, -116.9) * mm, "end": v(224.9, -116.9) * mm});
            skLineSegment(sketch, "E6.10.5.3", {"start": v(224.9, -116.9) * mm, "end": v(224.9, -119.1) * mm});
            skArc(sketch, "E6.10.6.0", {"start": v(225.96, -142.7) * mm, "mid": v(246.1, -141.6) * mm, "end": v(225.96, -140.5) * mm});
            skLineSegment(sketch, "E6.10.6.1", {"start": v(225.96, -142.7) * mm, "end": v(224.9, -142.7) * mm});
            skLineSegment(sketch, "E6.10.6.2", {"start": v(225.96, -140.5) * mm, "end": v(224.9, -140.5) * mm});
            skLineSegment(sketch, "E6.10.6.3", {"start": v(224.9, -140.5) * mm, "end": v(224.9, -142.7) * mm});
            skArc(sketch, "E6.10.7.0", {"start": v(225.96, -166.3) * mm, "mid": v(246.1, -165.2) * mm, "end": v(225.96, -164.1) * mm});
            skLineSegment(sketch, "E6.10.7.1", {"start": v(225.96, -166.3) * mm, "end": v(224.9, -166.3) * mm});
            skLineSegment(sketch, "E6.10.7.2", {"start": v(225.96, -164.1) * mm, "end": v(224.9, -164.1) * mm});
            skLineSegment(sketch, "E6.10.7.3", {"start": v(224.9, -164.1) * mm, "end": v(224.9, -166.3) * mm});
            skArc(sketch, "E6.10.8.0", {"start": v(225.96, -189.9) * mm, "mid": v(246.1, -188.8) * mm, "end": v(225.96, -187.7) * mm});
            skLineSegment(sketch, "E6.10.8.1", {"start": v(225.96, -189.9) * mm, "end": v(224.9, -189.9) * mm});
            skLineSegment(sketch, "E6.10.8.2", {"start": v(225.96, -187.7) * mm, "end": v(224.9, -187.7) * mm});
            skLineSegment(sketch, "E6.10.8.3", {"start": v(224.9, -187.7) * mm, "end": v(224.9, -189.9) * mm});
            skArc(sketch, "E6.10.9.0", {"start": v(225.96, -213.5) * mm, "mid": v(246.1, -212.4) * mm, "end": v(225.96, -211.3) * mm});
            skLineSegment(sketch, "E6.10.9.1", {"start": v(225.96, -213.5) * mm, "end": v(224.9, -213.5) * mm});
            skLineSegment(sketch, "E6.10.9.2", {"start": v(225.96, -211.3) * mm, "end": v(224.9, -211.3) * mm});
            skLineSegment(sketch, "E6.10.9.3", {"start": v(224.9, -211.3) * mm, "end": v(224.9, -213.5) * mm});
            skArc(sketch, "E6.10.10.0", {"start": v(225.96, -237.1) * mm, "mid": v(246.1, -236) * mm, "end": v(225.96, -234.9) * mm});
            skLineSegment(sketch, "E6.10.10.1", {"start": v(225.96, -237.1) * mm, "end": v(224.9, -237.1) * mm});
            skLineSegment(sketch, "E6.10.10.2", {"start": v(225.96, -234.9) * mm, "end": v(224.9, -234.9) * mm});
            skLineSegment(sketch, "E6.10.10.3", {"start": v(224.9, -234.9) * mm, "end": v(224.9, -237.1) * mm});
            skArc(sketch, "E6.10.11.0", {"start": v(225.96, -260.7) * mm, "mid": v(246.1, -259.6) * mm, "end": v(225.96, -258.5) * mm});
            skLineSegment(sketch, "E6.10.11.1", {"start": v(225.96, -260.7) * mm, "end": v(224.9, -260.7) * mm});
            skLineSegment(sketch, "E6.10.11.2", {"start": v(225.96, -258.5) * mm, "end": v(224.9, -258.5) * mm});
            skLineSegment(sketch, "E6.10.11.3", {"start": v(224.9, -258.5) * mm, "end": v(224.9, -260.7) * mm});
            skArc(sketch, "E6.10.12.0", {"start": v(225.96, -284.3) * mm, "mid": v(246.1, -283.2) * mm, "end": v(225.96, -282.1) * mm});
            skLineSegment(sketch, "E6.10.12.1", {"start": v(225.96, -284.3) * mm, "end": v(224.9, -284.3) * mm});
            skLineSegment(sketch, "E6.10.12.2", {"start": v(225.96, -282.1) * mm, "end": v(224.9, -282.1) * mm});
            skLineSegment(sketch, "E6.10.12.3", {"start": v(224.9, -282.1) * mm, "end": v(224.9, -284.3) * mm});
            skArc(sketch, "E6.10.13.0", {"start": v(225.96, -307.9) * mm, "mid": v(246.1, -306.8) * mm, "end": v(225.96, -305.7) * mm});
            skLineSegment(sketch, "E6.10.13.1", {"start": v(225.96, -307.9) * mm, "end": v(224.9, -307.9) * mm});
            skLineSegment(sketch, "E6.10.13.2", {"start": v(225.96, -305.7) * mm, "end": v(224.9, -305.7) * mm});
            skLineSegment(sketch, "E6.10.13.3", {"start": v(224.9, -305.7) * mm, "end": v(224.9, -307.9) * mm});
            skArc(sketch, "E6.11.0.0", {"start": v(249.56, -1.1) * mm, "mid": v(269.7, 0) * mm, "end": v(249.56, 1.1) * mm});
            skLineSegment(sketch, "E6.11.0.1", {"start": v(249.56, -1.1) * mm, "end": v(248.5, -1.1) * mm});
            skLineSegment(sketch, "E6.11.0.2", {"start": v(249.56, 1.1) * mm, "end": v(248.5, 1.1) * mm});
            skLineSegment(sketch, "E6.11.0.3", {"start": v(248.5, 1.1) * mm, "end": v(248.5, -1.1) * mm});
            skArc(sketch, "E6.11.1.0", {"start": v(249.56, -24.7) * mm, "mid": v(269.7, -23.6) * mm, "end": v(249.56, -22.5) * mm});
            skLineSegment(sketch, "E6.11.1.1", {"start": v(249.56, -24.7) * mm, "end": v(248.5, -24.7) * mm});
            skLineSegment(sketch, "E6.11.1.2", {"start": v(249.56, -22.5) * mm, "end": v(248.5, -22.5) * mm});
            skLineSegment(sketch, "E6.11.1.3", {"start": v(248.5, -22.5) * mm, "end": v(248.5, -24.7) * mm});
            skArc(sketch, "E6.11.2.0", {"start": v(249.56, -48.3) * mm, "mid": v(269.7, -47.2) * mm, "end": v(249.56, -46.1) * mm});
            skLineSegment(sketch, "E6.11.2.1", {"start": v(249.56, -48.3) * mm, "end": v(248.5, -48.3) * mm});
            skLineSegment(sketch, "E6.11.2.2", {"start": v(249.56, -46.1) * mm, "end": v(248.5, -46.1) * mm});
            skLineSegment(sketch, "E6.11.2.3", {"start": v(248.5, -46.1) * mm, "end": v(248.5, -48.3) * mm});
            skArc(sketch, "E6.11.3.0", {"start": v(249.56, -71.9) * mm, "mid": v(269.7, -70.8) * mm, "end": v(249.56, -69.7) * mm});
            skLineSegment(sketch, "E6.11.3.1", {"start": v(249.56, -71.9) * mm, "end": v(248.5, -71.9) * mm});
            skLineSegment(sketch, "E6.11.3.2", {"start": v(249.56, -69.7) * mm, "end": v(248.5, -69.7) * mm});
            skLineSegment(sketch, "E6.11.3.3", {"start": v(248.5, -69.7) * mm, "end": v(248.5, -71.9) * mm});
            skArc(sketch, "E6.11.4.0", {"start": v(249.56, -95.5) * mm, "mid": v(269.7, -94.4) * mm, "end": v(249.56, -93.3) * mm});
            skLineSegment(sketch, "E6.11.4.1", {"start": v(249.56, -95.5) * mm, "end": v(248.5, -95.5) * mm});
            skLineSegment(sketch, "E6.11.4.2", {"start": v(249.56, -93.3) * mm, "end": v(248.5, -93.3) * mm});
            skLineSegment(sketch, "E6.11.4.3", {"start": v(248.5, -93.3) * mm, "end": v(248.5, -95.5) * mm});
            skArc(sketch, "E6.11.5.0", {"start": v(249.56, -119.1) * mm, "mid": v(269.7, -118) * mm, "end": v(249.56, -116.9) * mm});
            skLineSegment(sketch, "E6.11.5.1", {"start": v(249.56, -119.1) * mm, "end": v(248.5, -119.1) * mm});
            skLineSegment(sketch, "E6.11.5.2", {"start": v(249.56, -116.9) * mm, "end": v(248.5, -116.9) * mm});
            skLineSegment(sketch, "E6.11.5.3", {"start": v(248.5, -116.9) * mm, "end": v(248.5, -119.1) * mm});
            skArc(sketch, "E6.11.6.0", {"start": v(249.56, -142.7) * mm, "mid": v(269.7, -141.6) * mm, "end": v(249.56, -140.5) * mm});
            skLineSegment(sketch, "E6.11.6.1", {"start": v(249.56, -142.7) * mm, "end": v(248.5, -142.7) * mm});
            skLineSegment(sketch, "E6.11.6.2", {"start": v(249.56, -140.5) * mm, "end": v(248.5, -140.5) * mm});
            skLineSegment(sketch, "E6.11.6.3", {"start": v(248.5, -140.5) * mm, "end": v(248.5, -142.7) * mm});
            skArc(sketch, "E6.11.7.0", {"start": v(249.56, -166.3) * mm, "mid": v(269.7, -165.2) * mm, "end": v(249.56, -164.1) * mm});
            skLineSegment(sketch, "E6.11.7.1", {"start": v(249.56, -166.3) * mm, "end": v(248.5, -166.3) * mm});
            skLineSegment(sketch, "E6.11.7.2", {"start": v(249.56, -164.1) * mm, "end": v(248.5, -164.1) * mm});
            skLineSegment(sketch, "E6.11.7.3", {"start": v(248.5, -164.1) * mm, "end": v(248.5, -166.3) * mm});
            skArc(sketch, "E6.11.8.0", {"start": v(249.56, -189.9) * mm, "mid": v(269.7, -188.8) * mm, "end": v(249.56, -187.7) * mm});
            skLineSegment(sketch, "E6.11.8.1", {"start": v(249.56, -189.9) * mm, "end": v(248.5, -189.9) * mm});
            skLineSegment(sketch, "E6.11.8.2", {"start": v(249.56, -187.7) * mm, "end": v(248.5, -187.7) * mm});
            skLineSegment(sketch, "E6.11.8.3", {"start": v(248.5, -187.7) * mm, "end": v(248.5, -189.9) * mm});
            skArc(sketch, "E6.11.9.0", {"start": v(249.56, -213.5) * mm, "mid": v(269.7, -212.4) * mm, "end": v(249.56, -211.3) * mm});
            skLineSegment(sketch, "E6.11.9.1", {"start": v(249.56, -213.5) * mm, "end": v(248.5, -213.5) * mm});
            skLineSegment(sketch, "E6.11.9.2", {"start": v(249.56, -211.3) * mm, "end": v(248.5, -211.3) * mm});
            skLineSegment(sketch, "E6.11.9.3", {"start": v(248.5, -211.3) * mm, "end": v(248.5, -213.5) * mm});
            skArc(sketch, "E6.11.10.0", {"start": v(249.56, -237.1) * mm, "mid": v(269.7, -236) * mm, "end": v(249.56, -234.9) * mm});
            skLineSegment(sketch, "E6.11.10.1", {"start": v(249.56, -237.1) * mm, "end": v(248.5, -237.1) * mm});
            skLineSegment(sketch, "E6.11.10.2", {"start": v(249.56, -234.9) * mm, "end": v(248.5, -234.9) * mm});
            skLineSegment(sketch, "E6.11.10.3", {"start": v(248.5, -234.9) * mm, "end": v(248.5, -237.1) * mm});
            skArc(sketch, "E6.11.11.0", {"start": v(249.56, -260.7) * mm, "mid": v(269.7, -259.6) * mm, "end": v(249.56, -258.5) * mm});
            skLineSegment(sketch, "E6.11.11.1", {"start": v(249.56, -260.7) * mm, "end": v(248.5, -260.7) * mm});
            skLineSegment(sketch, "E6.11.11.2", {"start": v(249.56, -258.5) * mm, "end": v(248.5, -258.5) * mm});
            skLineSegment(sketch, "E6.11.11.3", {"start": v(248.5, -258.5) * mm, "end": v(248.5, -260.7) * mm});
            skArc(sketch, "E6.11.12.0", {"start": v(249.56, -284.3) * mm, "mid": v(269.7, -283.2) * mm, "end": v(249.56, -282.1) * mm});
            skLineSegment(sketch, "E6.11.12.1", {"start": v(249.56, -284.3) * mm, "end": v(248.5, -284.3) * mm});
            skLineSegment(sketch, "E6.11.12.2", {"start": v(249.56, -282.1) * mm, "end": v(248.5, -282.1) * mm});
            skLineSegment(sketch, "E6.11.12.3", {"start": v(248.5, -282.1) * mm, "end": v(248.5, -284.3) * mm});
            skArc(sketch, "E6.11.13.0", {"start": v(249.56, -307.9) * mm, "mid": v(269.7, -306.8) * mm, "end": v(249.56, -305.7) * mm});
            skLineSegment(sketch, "E6.11.13.1", {"start": v(249.56, -307.9) * mm, "end": v(248.5, -307.9) * mm});
            skLineSegment(sketch, "E6.11.13.2", {"start": v(249.56, -305.7) * mm, "end": v(248.5, -305.7) * mm});
            skLineSegment(sketch, "E6.11.13.3", {"start": v(248.5, -305.7) * mm, "end": v(248.5, -307.9) * mm});
            skArc(sketch, "E6.12.0.0", {"start": v(273.16, -1.1) * mm, "mid": v(293.3, 0) * mm, "end": v(273.16, 1.1) * mm});
            skLineSegment(sketch, "E6.12.0.1", {"start": v(273.16, -1.1) * mm, "end": v(272.1, -1.1) * mm});
            skLineSegment(sketch, "E6.12.0.2", {"start": v(273.16, 1.1) * mm, "end": v(272.1, 1.1) * mm});
            skLineSegment(sketch, "E6.12.0.3", {"start": v(272.1, 1.1) * mm, "end": v(272.1, -1.1) * mm});
            skArc(sketch, "E6.12.1.0", {"start": v(273.16, -24.7) * mm, "mid": v(293.3, -23.6) * mm, "end": v(273.16, -22.5) * mm});
            skLineSegment(sketch, "E6.12.1.1", {"start": v(273.16, -24.7) * mm, "end": v(272.1, -24.7) * mm});
            skLineSegment(sketch, "E6.12.1.2", {"start": v(273.16, -22.5) * mm, "end": v(272.1, -22.5) * mm});
            skLineSegment(sketch, "E6.12.1.3", {"start": v(272.1, -22.5) * mm, "end": v(272.1, -24.7) * mm});
            skArc(sketch, "E6.12.2.0", {"start": v(273.16, -48.3) * mm, "mid": v(293.3, -47.2) * mm, "end": v(273.16, -46.1) * mm});
            skLineSegment(sketch, "E6.12.2.1", {"start": v(273.16, -48.3) * mm, "end": v(272.1, -48.3) * mm});
            skLineSegment(sketch, "E6.12.2.2", {"start": v(273.16, -46.1) * mm, "end": v(272.1, -46.1) * mm});
            skLineSegment(sketch, "E6.12.2.3", {"start": v(272.1, -46.1) * mm, "end": v(272.1, -48.3) * mm});
            skArc(sketch, "E6.12.3.0", {"start": v(273.16, -71.9) * mm, "mid": v(293.3, -70.8) * mm, "end": v(273.16, -69.7) * mm});
            skLineSegment(sketch, "E6.12.3.1", {"start": v(273.16, -71.9) * mm, "end": v(272.1, -71.9) * mm});
            skLineSegment(sketch, "E6.12.3.2", {"start": v(273.16, -69.7) * mm, "end": v(272.1, -69.7) * mm});
            skLineSegment(sketch, "E6.12.3.3", {"start": v(272.1, -69.7) * mm, "end": v(272.1, -71.9) * mm});
            skArc(sketch, "E6.12.4.0", {"start": v(273.16, -95.5) * mm, "mid": v(293.3, -94.4) * mm, "end": v(273.16, -93.3) * mm});
            skLineSegment(sketch, "E6.12.4.1", {"start": v(273.16, -95.5) * mm, "end": v(272.1, -95.5) * mm});
            skLineSegment(sketch, "E6.12.4.2", {"start": v(273.16, -93.3) * mm, "end": v(272.1, -93.3) * mm});
            skLineSegment(sketch, "E6.12.4.3", {"start": v(272.1, -93.3) * mm, "end": v(272.1, -95.5) * mm});
            skArc(sketch, "E6.12.5.0", {"start": v(273.16, -119.1) * mm, "mid": v(293.3, -118) * mm, "end": v(273.16, -116.9) * mm});
            skLineSegment(sketch, "E6.12.5.1", {"start": v(273.16, -119.1) * mm, "end": v(272.1, -119.1) * mm});
            skLineSegment(sketch, "E6.12.5.2", {"start": v(273.16, -116.9) * mm, "end": v(272.1, -116.9) * mm});
            skLineSegment(sketch, "E6.12.5.3", {"start": v(272.1, -116.9) * mm, "end": v(272.1, -119.1) * mm});
            skArc(sketch, "E6.12.6.0", {"start": v(273.16, -142.7) * mm, "mid": v(293.3, -141.6) * mm, "end": v(273.16, -140.5) * mm});
            skLineSegment(sketch, "E6.12.6.1", {"start": v(273.16, -142.7) * mm, "end": v(272.1, -142.7) * mm});
            skLineSegment(sketch, "E6.12.6.2", {"start": v(273.16, -140.5) * mm, "end": v(272.1, -140.5) * mm});
            skLineSegment(sketch, "E6.12.6.3", {"start": v(272.1, -140.5) * mm, "end": v(272.1, -142.7) * mm});
            skArc(sketch, "E6.12.7.0", {"start": v(273.16, -166.3) * mm, "mid": v(293.3, -165.2) * mm, "end": v(273.16, -164.1) * mm});
            skLineSegment(sketch, "E6.12.7.1", {"start": v(273.16, -166.3) * mm, "end": v(272.1, -166.3) * mm});
            skLineSegment(sketch, "E6.12.7.2", {"start": v(273.16, -164.1) * mm, "end": v(272.1, -164.1) * mm});
            skLineSegment(sketch, "E6.12.7.3", {"start": v(272.1, -164.1) * mm, "end": v(272.1, -166.3) * mm});
            skArc(sketch, "E6.12.8.0", {"start": v(273.16, -189.9) * mm, "mid": v(293.3, -188.8) * mm, "end": v(273.16, -187.7) * mm});
            skLineSegment(sketch, "E6.12.8.1", {"start": v(273.16, -189.9) * mm, "end": v(272.1, -189.9) * mm});
            skLineSegment(sketch, "E6.12.8.2", {"start": v(273.16, -187.7) * mm, "end": v(272.1, -187.7) * mm});
            skLineSegment(sketch, "E6.12.8.3", {"start": v(272.1, -187.7) * mm, "end": v(272.1, -189.9) * mm});
            skArc(sketch, "E6.12.9.0", {"start": v(273.16, -213.5) * mm, "mid": v(293.3, -212.4) * mm, "end": v(273.16, -211.3) * mm});
            skLineSegment(sketch, "E6.12.9.1", {"start": v(273.16, -213.5) * mm, "end": v(272.1, -213.5) * mm});
            skLineSegment(sketch, "E6.12.9.2", {"start": v(273.16, -211.3) * mm, "end": v(272.1, -211.3) * mm});
            skLineSegment(sketch, "E6.12.9.3", {"start": v(272.1, -211.3) * mm, "end": v(272.1, -213.5) * mm});
            skArc(sketch, "E6.12.10.0", {"start": v(273.16, -237.1) * mm, "mid": v(293.3, -236) * mm, "end": v(273.16, -234.9) * mm});
            skLineSegment(sketch, "E6.12.10.1", {"start": v(273.16, -237.1) * mm, "end": v(272.1, -237.1) * mm});
            skLineSegment(sketch, "E6.12.10.2", {"start": v(273.16, -234.9) * mm, "end": v(272.1, -234.9) * mm});
            skLineSegment(sketch, "E6.12.10.3", {"start": v(272.1, -234.9) * mm, "end": v(272.1, -237.1) * mm});
            skArc(sketch, "E6.12.11.0", {"start": v(273.16, -260.7) * mm, "mid": v(293.3, -259.6) * mm, "end": v(273.16, -258.5) * mm});
            skLineSegment(sketch, "E6.12.11.1", {"start": v(273.16, -260.7) * mm, "end": v(272.1, -260.7) * mm});
            skLineSegment(sketch, "E6.12.11.2", {"start": v(273.16, -258.5) * mm, "end": v(272.1, -258.5) * mm});
            skLineSegment(sketch, "E6.12.11.3", {"start": v(272.1, -258.5) * mm, "end": v(272.1, -260.7) * mm});
            skArc(sketch, "E6.12.12.0", {"start": v(273.16, -284.3) * mm, "mid": v(293.3, -283.2) * mm, "end": v(273.16, -282.1) * mm});
            skLineSegment(sketch, "E6.12.12.1", {"start": v(273.16, -284.3) * mm, "end": v(272.1, -284.3) * mm});
            skLineSegment(sketch, "E6.12.12.2", {"start": v(273.16, -282.1) * mm, "end": v(272.1, -282.1) * mm});
            skLineSegment(sketch, "E6.12.12.3", {"start": v(272.1, -282.1) * mm, "end": v(272.1, -284.3) * mm});
            skArc(sketch, "E6.12.13.0", {"start": v(273.16, -307.9) * mm, "mid": v(293.3, -306.8) * mm, "end": v(273.16, -305.7) * mm});
            skLineSegment(sketch, "E6.12.13.1", {"start": v(273.16, -307.9) * mm, "end": v(272.1, -307.9) * mm});
            skLineSegment(sketch, "E6.12.13.2", {"start": v(273.16, -305.7) * mm, "end": v(272.1, -305.7) * mm});
            skLineSegment(sketch, "E6.12.13.3", {"start": v(272.1, -305.7) * mm, "end": v(272.1, -307.9) * mm});
            skArc(sketch, "E6.13.0.0", {"start": v(296.76, -1.1) * mm, "mid": v(316.9, 0) * mm, "end": v(296.76, 1.1) * mm});
            skLineSegment(sketch, "E6.13.0.1", {"start": v(296.76, -1.1) * mm, "end": v(295.7, -1.1) * mm});
            skLineSegment(sketch, "E6.13.0.2", {"start": v(296.76, 1.1) * mm, "end": v(295.7, 1.1) * mm});
            skLineSegment(sketch, "E6.13.0.3", {"start": v(295.7, 1.1) * mm, "end": v(295.7, -1.1) * mm});
            skArc(sketch, "E6.13.1.0", {"start": v(296.76, -24.7) * mm, "mid": v(316.9, -23.6) * mm, "end": v(296.76, -22.5) * mm});
            skLineSegment(sketch, "E6.13.1.1", {"start": v(296.76, -24.7) * mm, "end": v(295.7, -24.7) * mm});
            skLineSegment(sketch, "E6.13.1.2", {"start": v(296.76, -22.5) * mm, "end": v(295.7, -22.5) * mm});
            skLineSegment(sketch, "E6.13.1.3", {"start": v(295.7, -22.5) * mm, "end": v(295.7, -24.7) * mm});
            skArc(sketch, "E6.13.2.0", {"start": v(296.76, -48.3) * mm, "mid": v(316.9, -47.2) * mm, "end": v(296.76, -46.1) * mm});
            skLineSegment(sketch, "E6.13.2.1", {"start": v(296.76, -48.3) * mm, "end": v(295.7, -48.3) * mm});
            skLineSegment(sketch, "E6.13.2.2", {"start": v(296.76, -46.1) * mm, "end": v(295.7, -46.1) * mm});
            skLineSegment(sketch, "E6.13.2.3", {"start": v(295.7, -46.1) * mm, "end": v(295.7, -48.3) * mm});
            skArc(sketch, "E6.13.3.0", {"start": v(296.76, -71.9) * mm, "mid": v(316.9, -70.8) * mm, "end": v(296.76, -69.7) * mm});
            skLineSegment(sketch, "E6.13.3.1", {"start": v(296.76, -71.9) * mm, "end": v(295.7, -71.9) * mm});
            skLineSegment(sketch, "E6.13.3.2", {"start": v(296.76, -69.7) * mm, "end": v(295.7, -69.7) * mm});
            skLineSegment(sketch, "E6.13.3.3", {"start": v(295.7, -69.7) * mm, "end": v(295.7, -71.9) * mm});
            skArc(sketch, "E6.13.4.0", {"start": v(296.76, -95.5) * mm, "mid": v(316.9, -94.4) * mm, "end": v(296.76, -93.3) * mm});
            skLineSegment(sketch, "E6.13.4.1", {"start": v(296.76, -95.5) * mm, "end": v(295.7, -95.5) * mm});
            skLineSegment(sketch, "E6.13.4.2", {"start": v(296.76, -93.3) * mm, "end": v(295.7, -93.3) * mm});
            skLineSegment(sketch, "E6.13.4.3", {"start": v(295.7, -93.3) * mm, "end": v(295.7, -95.5) * mm});
            skArc(sketch, "E6.13.5.0", {"start": v(296.76, -119.1) * mm, "mid": v(316.9, -118) * mm, "end": v(296.76, -116.9) * mm});
            skLineSegment(sketch, "E6.13.5.1", {"start": v(296.76, -119.1) * mm, "end": v(295.7, -119.1) * mm});
            skLineSegment(sketch, "E6.13.5.2", {"start": v(296.76, -116.9) * mm, "end": v(295.7, -116.9) * mm});
            skLineSegment(sketch, "E6.13.5.3", {"start": v(295.7, -116.9) * mm, "end": v(295.7, -119.1) * mm});
            skArc(sketch, "E6.13.6.0", {"start": v(296.76, -142.7) * mm, "mid": v(316.9, -141.6) * mm, "end": v(296.76, -140.5) * mm});
            skLineSegment(sketch, "E6.13.6.1", {"start": v(296.76, -142.7) * mm, "end": v(295.7, -142.7) * mm});
            skLineSegment(sketch, "E6.13.6.2", {"start": v(296.76, -140.5) * mm, "end": v(295.7, -140.5) * mm});
            skLineSegment(sketch, "E6.13.6.3", {"start": v(295.7, -140.5) * mm, "end": v(295.7, -142.7) * mm});
            skArc(sketch, "E6.13.7.0", {"start": v(296.76, -166.3) * mm, "mid": v(316.9, -165.2) * mm, "end": v(296.76, -164.1) * mm});
            skLineSegment(sketch, "E6.13.7.1", {"start": v(296.76, -166.3) * mm, "end": v(295.7, -166.3) * mm});
            skLineSegment(sketch, "E6.13.7.2", {"start": v(296.76, -164.1) * mm, "end": v(295.7, -164.1) * mm});
            skLineSegment(sketch, "E6.13.7.3", {"start": v(295.7, -164.1) * mm, "end": v(295.7, -166.3) * mm});
            skArc(sketch, "E6.13.8.0", {"start": v(296.76, -189.9) * mm, "mid": v(316.9, -188.8) * mm, "end": v(296.76, -187.7) * mm});
            skLineSegment(sketch, "E6.13.8.1", {"start": v(296.76, -189.9) * mm, "end": v(295.7, -189.9) * mm});
            skLineSegment(sketch, "E6.13.8.2", {"start": v(296.76, -187.7) * mm, "end": v(295.7, -187.7) * mm});
            skLineSegment(sketch, "E6.13.8.3", {"start": v(295.7, -187.7) * mm, "end": v(295.7, -189.9) * mm});
            skArc(sketch, "E6.13.9.0", {"start": v(296.76, -213.5) * mm, "mid": v(316.9, -212.4) * mm, "end": v(296.76, -211.3) * mm});
            skLineSegment(sketch, "E6.13.9.1", {"start": v(296.76, -213.5) * mm, "end": v(295.7, -213.5) * mm});
            skLineSegment(sketch, "E6.13.9.2", {"start": v(296.76, -211.3) * mm, "end": v(295.7, -211.3) * mm});
            skLineSegment(sketch, "E6.13.9.3", {"start": v(295.7, -211.3) * mm, "end": v(295.7, -213.5) * mm});
            skArc(sketch, "E6.13.10.0", {"start": v(296.76, -237.1) * mm, "mid": v(316.9, -236) * mm, "end": v(296.76, -234.9) * mm});
            skLineSegment(sketch, "E6.13.10.1", {"start": v(296.76, -237.1) * mm, "end": v(295.7, -237.1) * mm});
            skLineSegment(sketch, "E6.13.10.2", {"start": v(296.76, -234.9) * mm, "end": v(295.7, -234.9) * mm});
            skLineSegment(sketch, "E6.13.10.3", {"start": v(295.7, -234.9) * mm, "end": v(295.7, -237.1) * mm});
            skArc(sketch, "E6.13.11.0", {"start": v(296.76, -260.7) * mm, "mid": v(316.9, -259.6) * mm, "end": v(296.76, -258.5) * mm});
            skLineSegment(sketch, "E6.13.11.1", {"start": v(296.76, -260.7) * mm, "end": v(295.7, -260.7) * mm});
            skLineSegment(sketch, "E6.13.11.2", {"start": v(296.76, -258.5) * mm, "end": v(295.7, -258.5) * mm});
            skLineSegment(sketch, "E6.13.11.3", {"start": v(295.7, -258.5) * mm, "end": v(295.7, -260.7) * mm});
            skArc(sketch, "E6.13.12.0", {"start": v(296.76, -284.3) * mm, "mid": v(316.9, -283.2) * mm, "end": v(296.76, -282.1) * mm});
            skLineSegment(sketch, "E6.13.12.1", {"start": v(296.76, -284.3) * mm, "end": v(295.7, -284.3) * mm});
            skLineSegment(sketch, "E6.13.12.2", {"start": v(296.76, -282.1) * mm, "end": v(295.7, -282.1) * mm});
            skLineSegment(sketch, "E6.13.12.3", {"start": v(295.7, -282.1) * mm, "end": v(295.7, -284.3) * mm});
            skArc(sketch, "E6.13.13.0", {"start": v(296.76, -307.9) * mm, "mid": v(316.9, -306.8) * mm, "end": v(296.76, -305.7) * mm});
            skLineSegment(sketch, "E6.13.13.1", {"start": v(296.76, -307.9) * mm, "end": v(295.7, -307.9) * mm});
            skLineSegment(sketch, "E6.13.13.2", {"start": v(296.76, -305.7) * mm, "end": v(295.7, -305.7) * mm});
            skLineSegment(sketch, "E6.13.13.3", {"start": v(295.7, -305.7) * mm, "end": v(295.7, -307.9) * mm});
            skArc(sketch, "E6.14.0.0", {"start": v(320.36, -1.1) * mm, "mid": v(340.5, 0) * mm, "end": v(320.36, 1.1) * mm});
            skLineSegment(sketch, "E6.14.0.1", {"start": v(320.36, -1.1) * mm, "end": v(319.3, -1.1) * mm});
            skLineSegment(sketch, "E6.14.0.2", {"start": v(320.36, 1.1) * mm, "end": v(319.3, 1.1) * mm});
            skLineSegment(sketch, "E6.14.0.3", {"start": v(319.3, 1.1) * mm, "end": v(319.3, -1.1) * mm});
            skArc(sketch, "E6.14.1.0", {"start": v(320.36, -24.7) * mm, "mid": v(340.5, -23.6) * mm, "end": v(320.36, -22.5) * mm});
            skLineSegment(sketch, "E6.14.1.1", {"start": v(320.36, -24.7) * mm, "end": v(319.3, -24.7) * mm});
            skLineSegment(sketch, "E6.14.1.2", {"start": v(320.36, -22.5) * mm, "end": v(319.3, -22.5) * mm});
            skLineSegment(sketch, "E6.14.1.3", {"start": v(319.3, -22.5) * mm, "end": v(319.3, -24.7) * mm});
            skArc(sketch, "E6.14.2.0", {"start": v(320.36, -48.3) * mm, "mid": v(340.5, -47.2) * mm, "end": v(320.36, -46.1) * mm});
            skLineSegment(sketch, "E6.14.2.1", {"start": v(320.36, -48.3) * mm, "end": v(319.3, -48.3) * mm});
            skLineSegment(sketch, "E6.14.2.2", {"start": v(320.36, -46.1) * mm, "end": v(319.3, -46.1) * mm});
            skLineSegment(sketch, "E6.14.2.3", {"start": v(319.3, -46.1) * mm, "end": v(319.3, -48.3) * mm});
            skArc(sketch, "E6.14.3.0", {"start": v(320.36, -71.9) * mm, "mid": v(340.5, -70.8) * mm, "end": v(320.36, -69.7) * mm});
            skLineSegment(sketch, "E6.14.3.1", {"start": v(320.36, -71.9) * mm, "end": v(319.3, -71.9) * mm});
            skLineSegment(sketch, "E6.14.3.2", {"start": v(320.36, -69.7) * mm, "end": v(319.3, -69.7) * mm});
            skLineSegment(sketch, "E6.14.3.3", {"start": v(319.3, -69.7) * mm, "end": v(319.3, -71.9) * mm});
            skArc(sketch, "E6.14.4.0", {"start": v(320.36, -95.5) * mm, "mid": v(340.5, -94.4) * mm, "end": v(320.36, -93.3) * mm});
            skLineSegment(sketch, "E6.14.4.1", {"start": v(320.36, -95.5) * mm, "end": v(319.3, -95.5) * mm});
            skLineSegment(sketch, "E6.14.4.2", {"start": v(320.36, -93.3) * mm, "end": v(319.3, -93.3) * mm});
            skLineSegment(sketch, "E6.14.4.3", {"start": v(319.3, -93.3) * mm, "end": v(319.3, -95.5) * mm});
            skArc(sketch, "E6.14.5.0", {"start": v(320.36, -119.1) * mm, "mid": v(340.5, -118) * mm, "end": v(320.36, -116.9) * mm});
            skLineSegment(sketch, "E6.14.5.1", {"start": v(320.36, -119.1) * mm, "end": v(319.3, -119.1) * mm});
            skLineSegment(sketch, "E6.14.5.2", {"start": v(320.36, -116.9) * mm, "end": v(319.3, -116.9) * mm});
            skLineSegment(sketch, "E6.14.5.3", {"start": v(319.3, -116.9) * mm, "end": v(319.3, -119.1) * mm});
            skArc(sketch, "E6.14.6.0", {"start": v(320.36, -142.7) * mm, "mid": v(340.5, -141.6) * mm, "end": v(320.36, -140.5) * mm});
            skLineSegment(sketch, "E6.14.6.1", {"start": v(320.36, -142.7) * mm, "end": v(319.3, -142.7) * mm});
            skLineSegment(sketch, "E6.14.6.2", {"start": v(320.36, -140.5) * mm, "end": v(319.3, -140.5) * mm});
            skLineSegment(sketch, "E6.14.6.3", {"start": v(319.3, -140.5) * mm, "end": v(319.3, -142.7) * mm});
            skArc(sketch, "E6.14.7.0", {"start": v(320.36, -166.3) * mm, "mid": v(340.5, -165.2) * mm, "end": v(320.36, -164.1) * mm});
            skLineSegment(sketch, "E6.14.7.1", {"start": v(320.36, -166.3) * mm, "end": v(319.3, -166.3) * mm});
            skLineSegment(sketch, "E6.14.7.2", {"start": v(320.36, -164.1) * mm, "end": v(319.3, -164.1) * mm});
            skLineSegment(sketch, "E6.14.7.3", {"start": v(319.3, -164.1) * mm, "end": v(319.3, -166.3) * mm});
            skArc(sketch, "E6.14.8.0", {"start": v(320.36, -189.9) * mm, "mid": v(340.5, -188.8) * mm, "end": v(320.36, -187.7) * mm});
            skLineSegment(sketch, "E6.14.8.1", {"start": v(320.36, -189.9) * mm, "end": v(319.3, -189.9) * mm});
            skLineSegment(sketch, "E6.14.8.2", {"start": v(320.36, -187.7) * mm, "end": v(319.3, -187.7) * mm});
            skLineSegment(sketch, "E6.14.8.3", {"start": v(319.3, -187.7) * mm, "end": v(319.3, -189.9) * mm});
            skArc(sketch, "E6.14.9.0", {"start": v(320.36, -213.5) * mm, "mid": v(340.5, -212.4) * mm, "end": v(320.36, -211.3) * mm});
            skLineSegment(sketch, "E6.14.9.1", {"start": v(320.36, -213.5) * mm, "end": v(319.3, -213.5) * mm});
            skLineSegment(sketch, "E6.14.9.2", {"start": v(320.36, -211.3) * mm, "end": v(319.3, -211.3) * mm});
            skLineSegment(sketch, "E6.14.9.3", {"start": v(319.3, -211.3) * mm, "end": v(319.3, -213.5) * mm});
            skArc(sketch, "E6.14.10.0", {"start": v(320.36, -237.1) * mm, "mid": v(340.5, -236) * mm, "end": v(320.36, -234.9) * mm});
            skLineSegment(sketch, "E6.14.10.1", {"start": v(320.36, -237.1) * mm, "end": v(319.3, -237.1) * mm});
            skLineSegment(sketch, "E6.14.10.2", {"start": v(320.36, -234.9) * mm, "end": v(319.3, -234.9) * mm});
            skLineSegment(sketch, "E6.14.10.3", {"start": v(319.3, -234.9) * mm, "end": v(319.3, -237.1) * mm});
            skArc(sketch, "E6.14.11.0", {"start": v(320.36, -260.7) * mm, "mid": v(340.5, -259.6) * mm, "end": v(320.36, -258.5) * mm});
            skLineSegment(sketch, "E6.14.11.1", {"start": v(320.36, -260.7) * mm, "end": v(319.3, -260.7) * mm});
            skLineSegment(sketch, "E6.14.11.2", {"start": v(320.36, -258.5) * mm, "end": v(319.3, -258.5) * mm});
            skLineSegment(sketch, "E6.14.11.3", {"start": v(319.3, -258.5) * mm, "end": v(319.3, -260.7) * mm});
            skArc(sketch, "E6.14.12.0", {"start": v(320.36, -284.3) * mm, "mid": v(340.5, -283.2) * mm, "end": v(320.36, -282.1) * mm});
            skLineSegment(sketch, "E6.14.12.1", {"start": v(320.36, -284.3) * mm, "end": v(319.3, -284.3) * mm});
            skLineSegment(sketch, "E6.14.12.2", {"start": v(320.36, -282.1) * mm, "end": v(319.3, -282.1) * mm});
            skLineSegment(sketch, "E6.14.12.3", {"start": v(319.3, -282.1) * mm, "end": v(319.3, -284.3) * mm});
            skArc(sketch, "E6.14.13.0", {"start": v(320.36, -307.9) * mm, "mid": v(340.5, -306.8) * mm, "end": v(320.36, -305.7) * mm});
            skLineSegment(sketch, "E6.14.13.1", {"start": v(320.36, -307.9) * mm, "end": v(319.3, -307.9) * mm});
            skLineSegment(sketch, "E6.14.13.2", {"start": v(320.36, -305.7) * mm, "end": v(319.3, -305.7) * mm});
            skLineSegment(sketch, "E6.14.13.3", {"start": v(319.3, -305.7) * mm, "end": v(319.3, -307.9) * mm});
            skArc(sketch, "E6.15.0.0", {"start": v(343.96, -1.1) * mm, "mid": v(364.1, 0) * mm, "end": v(343.96, 1.1) * mm});
            skLineSegment(sketch, "E6.15.0.1", {"start": v(343.96, -1.1) * mm, "end": v(342.9, -1.1) * mm});
            skLineSegment(sketch, "E6.15.0.2", {"start": v(343.96, 1.1) * mm, "end": v(342.9, 1.1) * mm});
            skLineSegment(sketch, "E6.15.0.3", {"start": v(342.9, 1.1) * mm, "end": v(342.9, -1.1) * mm});
            skArc(sketch, "E6.15.1.0", {"start": v(343.96, -24.7) * mm, "mid": v(364.1, -23.6) * mm, "end": v(343.96, -22.5) * mm});
            skLineSegment(sketch, "E6.15.1.1", {"start": v(343.96, -24.7) * mm, "end": v(342.9, -24.7) * mm});
            skLineSegment(sketch, "E6.15.1.2", {"start": v(343.96, -22.5) * mm, "end": v(342.9, -22.5) * mm});
            skLineSegment(sketch, "E6.15.1.3", {"start": v(342.9, -22.5) * mm, "end": v(342.9, -24.7) * mm});
            skArc(sketch, "E6.15.2.0", {"start": v(343.96, -48.3) * mm, "mid": v(364.1, -47.2) * mm, "end": v(343.96, -46.1) * mm});
            skLineSegment(sketch, "E6.15.2.1", {"start": v(343.96, -48.3) * mm, "end": v(342.9, -48.3) * mm});
            skLineSegment(sketch, "E6.15.2.2", {"start": v(343.96, -46.1) * mm, "end": v(342.9, -46.1) * mm});
            skLineSegment(sketch, "E6.15.2.3", {"start": v(342.9, -46.1) * mm, "end": v(342.9, -48.3) * mm});
            skArc(sketch, "E6.15.3.0", {"start": v(343.96, -71.9) * mm, "mid": v(364.1, -70.8) * mm, "end": v(343.96, -69.7) * mm});
            skLineSegment(sketch, "E6.15.3.1", {"start": v(343.96, -71.9) * mm, "end": v(342.9, -71.9) * mm});
            skLineSegment(sketch, "E6.15.3.2", {"start": v(343.96, -69.7) * mm, "end": v(342.9, -69.7) * mm});
            skLineSegment(sketch, "E6.15.3.3", {"start": v(342.9, -69.7) * mm, "end": v(342.9, -71.9) * mm});
            skArc(sketch, "E6.15.4.0", {"start": v(343.96, -95.5) * mm, "mid": v(364.1, -94.4) * mm, "end": v(343.96, -93.3) * mm});
            skLineSegment(sketch, "E6.15.4.1", {"start": v(343.96, -95.5) * mm, "end": v(342.9, -95.5) * mm});
            skLineSegment(sketch, "E6.15.4.2", {"start": v(343.96, -93.3) * mm, "end": v(342.9, -93.3) * mm});
            skLineSegment(sketch, "E6.15.4.3", {"start": v(342.9, -93.3) * mm, "end": v(342.9, -95.5) * mm});
            skArc(sketch, "E6.15.5.0", {"start": v(343.96, -119.1) * mm, "mid": v(364.1, -118) * mm, "end": v(343.96, -116.9) * mm});
            skLineSegment(sketch, "E6.15.5.1", {"start": v(343.96, -119.1) * mm, "end": v(342.9, -119.1) * mm});
            skLineSegment(sketch, "E6.15.5.2", {"start": v(343.96, -116.9) * mm, "end": v(342.9, -116.9) * mm});
            skLineSegment(sketch, "E6.15.5.3", {"start": v(342.9, -116.9) * mm, "end": v(342.9, -119.1) * mm});
            skArc(sketch, "E6.15.6.0", {"start": v(343.96, -142.7) * mm, "mid": v(364.1, -141.6) * mm, "end": v(343.96, -140.5) * mm});
            skLineSegment(sketch, "E6.15.6.1", {"start": v(343.96, -142.7) * mm, "end": v(342.9, -142.7) * mm});
            skLineSegment(sketch, "E6.15.6.2", {"start": v(343.96, -140.5) * mm, "end": v(342.9, -140.5) * mm});
            skLineSegment(sketch, "E6.15.6.3", {"start": v(342.9, -140.5) * mm, "end": v(342.9, -142.7) * mm});
            skArc(sketch, "E6.15.7.0", {"start": v(343.96, -166.3) * mm, "mid": v(364.1, -165.2) * mm, "end": v(343.96, -164.1) * mm});
            skLineSegment(sketch, "E6.15.7.1", {"start": v(343.96, -166.3) * mm, "end": v(342.9, -166.3) * mm});
            skLineSegment(sketch, "E6.15.7.2", {"start": v(343.96, -164.1) * mm, "end": v(342.9, -164.1) * mm});
            skLineSegment(sketch, "E6.15.7.3", {"start": v(342.9, -164.1) * mm, "end": v(342.9, -166.3) * mm});
            skArc(sketch, "E6.15.8.0", {"start": v(343.96, -189.9) * mm, "mid": v(364.1, -188.8) * mm, "end": v(343.96, -187.7) * mm});
            skLineSegment(sketch, "E6.15.8.1", {"start": v(343.96, -189.9) * mm, "end": v(342.9, -189.9) * mm});
            skLineSegment(sketch, "E6.15.8.2", {"start": v(343.96, -187.7) * mm, "end": v(342.9, -187.7) * mm});
            skLineSegment(sketch, "E6.15.8.3", {"start": v(342.9, -187.7) * mm, "end": v(342.9, -189.9) * mm});
            skArc(sketch, "E6.15.9.0", {"start": v(343.96, -213.5) * mm, "mid": v(364.1, -212.4) * mm, "end": v(343.96, -211.3) * mm});
            skLineSegment(sketch, "E6.15.9.1", {"start": v(343.96, -213.5) * mm, "end": v(342.9, -213.5) * mm});
            skLineSegment(sketch, "E6.15.9.2", {"start": v(343.96, -211.3) * mm, "end": v(342.9, -211.3) * mm});
            skLineSegment(sketch, "E6.15.9.3", {"start": v(342.9, -211.3) * mm, "end": v(342.9, -213.5) * mm});
            skArc(sketch, "E6.15.10.0", {"start": v(343.96, -237.1) * mm, "mid": v(364.1, -236) * mm, "end": v(343.96, -234.9) * mm});
            skLineSegment(sketch, "E6.15.10.1", {"start": v(343.96, -237.1) * mm, "end": v(342.9, -237.1) * mm});
            skLineSegment(sketch, "E6.15.10.2", {"start": v(343.96, -234.9) * mm, "end": v(342.9, -234.9) * mm});
            skLineSegment(sketch, "E6.15.10.3", {"start": v(342.9, -234.9) * mm, "end": v(342.9, -237.1) * mm});
            skArc(sketch, "E6.15.11.0", {"start": v(343.96, -260.7) * mm, "mid": v(364.1, -259.6) * mm, "end": v(343.96, -258.5) * mm});
            skLineSegment(sketch, "E6.15.11.1", {"start": v(343.96, -260.7) * mm, "end": v(342.9, -260.7) * mm});
            skLineSegment(sketch, "E6.15.11.2", {"start": v(343.96, -258.5) * mm, "end": v(342.9, -258.5) * mm});
            skLineSegment(sketch, "E6.15.11.3", {"start": v(342.9, -258.5) * mm, "end": v(342.9, -260.7) * mm});
            skArc(sketch, "E6.15.12.0", {"start": v(343.96, -284.3) * mm, "mid": v(364.1, -283.2) * mm, "end": v(343.96, -282.1) * mm});
            skLineSegment(sketch, "E6.15.12.1", {"start": v(343.96, -284.3) * mm, "end": v(342.9, -284.3) * mm});
            skLineSegment(sketch, "E6.15.12.2", {"start": v(343.96, -282.1) * mm, "end": v(342.9, -282.1) * mm});
            skLineSegment(sketch, "E6.15.12.3", {"start": v(342.9, -282.1) * mm, "end": v(342.9, -284.3) * mm});
            skArc(sketch, "E6.15.13.0", {"start": v(343.96, -307.9) * mm, "mid": v(364.1, -306.8) * mm, "end": v(343.96, -305.7) * mm});
            skLineSegment(sketch, "E6.15.13.1", {"start": v(343.96, -307.9) * mm, "end": v(342.9, -307.9) * mm});
            skLineSegment(sketch, "E6.15.13.2", {"start": v(343.96, -305.7) * mm, "end": v(342.9, -305.7) * mm});
            skLineSegment(sketch, "E6.15.13.3", {"start": v(342.9, -305.7) * mm, "end": v(342.9, -307.9) * mm});
            skArc(sketch, "E6.16.0.0", {"start": v(367.56, -1.1) * mm, "mid": v(387.7, 0) * mm, "end": v(367.56, 1.1) * mm});
            skLineSegment(sketch, "E6.16.0.1", {"start": v(367.56, -1.1) * mm, "end": v(366.5, -1.1) * mm});
            skLineSegment(sketch, "E6.16.0.2", {"start": v(367.56, 1.1) * mm, "end": v(366.5, 1.1) * mm});
            skLineSegment(sketch, "E6.16.0.3", {"start": v(366.5, 1.1) * mm, "end": v(366.5, -1.1) * mm});
            skArc(sketch, "E6.16.1.0", {"start": v(367.56, -24.7) * mm, "mid": v(387.7, -23.6) * mm, "end": v(367.56, -22.5) * mm});
            skLineSegment(sketch, "E6.16.1.1", {"start": v(367.56, -24.7) * mm, "end": v(366.5, -24.7) * mm});
            skLineSegment(sketch, "E6.16.1.2", {"start": v(367.56, -22.5) * mm, "end": v(366.5, -22.5) * mm});
            skLineSegment(sketch, "E6.16.1.3", {"start": v(366.5, -22.5) * mm, "end": v(366.5, -24.7) * mm});
            skArc(sketch, "E6.16.2.0", {"start": v(367.56, -48.3) * mm, "mid": v(387.7, -47.2) * mm, "end": v(367.56, -46.1) * mm});
            skLineSegment(sketch, "E6.16.2.1", {"start": v(367.56, -48.3) * mm, "end": v(366.5, -48.3) * mm});
            skLineSegment(sketch, "E6.16.2.2", {"start": v(367.56, -46.1) * mm, "end": v(366.5, -46.1) * mm});
            skLineSegment(sketch, "E6.16.2.3", {"start": v(366.5, -46.1) * mm, "end": v(366.5, -48.3) * mm});
            skArc(sketch, "E6.16.3.0", {"start": v(367.56, -71.9) * mm, "mid": v(387.7, -70.8) * mm, "end": v(367.56, -69.7) * mm});
            skLineSegment(sketch, "E6.16.3.1", {"start": v(367.56, -71.9) * mm, "end": v(366.5, -71.9) * mm});
            skLineSegment(sketch, "E6.16.3.2", {"start": v(367.56, -69.7) * mm, "end": v(366.5, -69.7) * mm});
            skLineSegment(sketch, "E6.16.3.3", {"start": v(366.5, -69.7) * mm, "end": v(366.5, -71.9) * mm});
            skArc(sketch, "E6.16.4.0", {"start": v(367.56, -95.5) * mm, "mid": v(387.7, -94.4) * mm, "end": v(367.56, -93.3) * mm});
            skLineSegment(sketch, "E6.16.4.1", {"start": v(367.56, -95.5) * mm, "end": v(366.5, -95.5) * mm});
            skLineSegment(sketch, "E6.16.4.2", {"start": v(367.56, -93.3) * mm, "end": v(366.5, -93.3) * mm});
            skLineSegment(sketch, "E6.16.4.3", {"start": v(366.5, -93.3) * mm, "end": v(366.5, -95.5) * mm});
            skArc(sketch, "E6.16.5.0", {"start": v(367.56, -119.1) * mm, "mid": v(387.7, -118) * mm, "end": v(367.56, -116.9) * mm});
            skLineSegment(sketch, "E6.16.5.1", {"start": v(367.56, -119.1) * mm, "end": v(366.5, -119.1) * mm});
            skLineSegment(sketch, "E6.16.5.2", {"start": v(367.56, -116.9) * mm, "end": v(366.5, -116.9) * mm});
            skLineSegment(sketch, "E6.16.5.3", {"start": v(366.5, -116.9) * mm, "end": v(366.5, -119.1) * mm});
            skArc(sketch, "E6.16.6.0", {"start": v(367.56, -142.7) * mm, "mid": v(387.7, -141.6) * mm, "end": v(367.56, -140.5) * mm});
            skLineSegment(sketch, "E6.16.6.1", {"start": v(367.56, -142.7) * mm, "end": v(366.5, -142.7) * mm});
            skLineSegment(sketch, "E6.16.6.2", {"start": v(367.56, -140.5) * mm, "end": v(366.5, -140.5) * mm});
            skLineSegment(sketch, "E6.16.6.3", {"start": v(366.5, -140.5) * mm, "end": v(366.5, -142.7) * mm});
            skArc(sketch, "E6.16.7.0", {"start": v(367.56, -166.3) * mm, "mid": v(387.7, -165.2) * mm, "end": v(367.56, -164.1) * mm});
            skLineSegment(sketch, "E6.16.7.1", {"start": v(367.56, -166.3) * mm, "end": v(366.5, -166.3) * mm});
            skLineSegment(sketch, "E6.16.7.2", {"start": v(367.56, -164.1) * mm, "end": v(366.5, -164.1) * mm});
            skLineSegment(sketch, "E6.16.7.3", {"start": v(366.5, -164.1) * mm, "end": v(366.5, -166.3) * mm});
            skArc(sketch, "E6.16.8.0", {"start": v(367.56, -189.9) * mm, "mid": v(387.7, -188.8) * mm, "end": v(367.56, -187.7) * mm});
            skLineSegment(sketch, "E6.16.8.1", {"start": v(367.56, -189.9) * mm, "end": v(366.5, -189.9) * mm});
            skLineSegment(sketch, "E6.16.8.2", {"start": v(367.56, -187.7) * mm, "end": v(366.5, -187.7) * mm});
            skLineSegment(sketch, "E6.16.8.3", {"start": v(366.5, -187.7) * mm, "end": v(366.5, -189.9) * mm});
            skArc(sketch, "E6.16.9.0", {"start": v(367.56, -213.5) * mm, "mid": v(387.7, -212.4) * mm, "end": v(367.56, -211.3) * mm});
            skLineSegment(sketch, "E6.16.9.1", {"start": v(367.56, -213.5) * mm, "end": v(366.5, -213.5) * mm});
            skLineSegment(sketch, "E6.16.9.2", {"start": v(367.56, -211.3) * mm, "end": v(366.5, -211.3) * mm});
            skLineSegment(sketch, "E6.16.9.3", {"start": v(366.5, -211.3) * mm, "end": v(366.5, -213.5) * mm});
            skArc(sketch, "E6.16.10.0", {"start": v(367.56, -237.1) * mm, "mid": v(387.7, -236) * mm, "end": v(367.56, -234.9) * mm});
            skLineSegment(sketch, "E6.16.10.1", {"start": v(367.56, -237.1) * mm, "end": v(366.5, -237.1) * mm});
            skLineSegment(sketch, "E6.16.10.2", {"start": v(367.56, -234.9) * mm, "end": v(366.5, -234.9) * mm});
            skLineSegment(sketch, "E6.16.10.3", {"start": v(366.5, -234.9) * mm, "end": v(366.5, -237.1) * mm});
            skArc(sketch, "E6.16.11.0", {"start": v(367.56, -260.7) * mm, "mid": v(387.7, -259.6) * mm, "end": v(367.56, -258.5) * mm});
            skLineSegment(sketch, "E6.16.11.1", {"start": v(367.56, -260.7) * mm, "end": v(366.5, -260.7) * mm});
            skLineSegment(sketch, "E6.16.11.2", {"start": v(367.56, -258.5) * mm, "end": v(366.5, -258.5) * mm});
            skLineSegment(sketch, "E6.16.11.3", {"start": v(366.5, -258.5) * mm, "end": v(366.5, -260.7) * mm});
            skArc(sketch, "E6.16.12.0", {"start": v(367.56, -284.3) * mm, "mid": v(387.7, -283.2) * mm, "end": v(367.56, -282.1) * mm});
            skLineSegment(sketch, "E6.16.12.1", {"start": v(367.56, -284.3) * mm, "end": v(366.5, -284.3) * mm});
            skLineSegment(sketch, "E6.16.12.2", {"start": v(367.56, -282.1) * mm, "end": v(366.5, -282.1) * mm});
            skLineSegment(sketch, "E6.16.12.3", {"start": v(366.5, -282.1) * mm, "end": v(366.5, -284.3) * mm});
            skArc(sketch, "E6.16.13.0", {"start": v(367.56, -307.9) * mm, "mid": v(387.7, -306.8) * mm, "end": v(367.56, -305.7) * mm});
            skLineSegment(sketch, "E6.16.13.1", {"start": v(367.56, -307.9) * mm, "end": v(366.5, -307.9) * mm});
            skLineSegment(sketch, "E6.16.13.2", {"start": v(367.56, -305.7) * mm, "end": v(366.5, -305.7) * mm});
            skLineSegment(sketch, "E6.16.13.3", {"start": v(366.5, -305.7) * mm, "end": v(366.5, -307.9) * mm});
            skArc(sketch, "E6.17.0.0", {"start": v(391.16, -1.1) * mm, "mid": v(411.3, 0) * mm, "end": v(391.16, 1.1) * mm});
            skLineSegment(sketch, "E6.17.0.1", {"start": v(391.16, -1.1) * mm, "end": v(390.1, -1.1) * mm});
            skLineSegment(sketch, "E6.17.0.2", {"start": v(391.16, 1.1) * mm, "end": v(390.1, 1.1) * mm});
            skLineSegment(sketch, "E6.17.0.3", {"start": v(390.1, 1.1) * mm, "end": v(390.1, -1.1) * mm});
            skArc(sketch, "E6.17.1.0", {"start": v(391.16, -24.7) * mm, "mid": v(411.3, -23.6) * mm, "end": v(391.16, -22.5) * mm});
            skLineSegment(sketch, "E6.17.1.1", {"start": v(391.16, -24.7) * mm, "end": v(390.1, -24.7) * mm});
            skLineSegment(sketch, "E6.17.1.2", {"start": v(391.16, -22.5) * mm, "end": v(390.1, -22.5) * mm});
            skLineSegment(sketch, "E6.17.1.3", {"start": v(390.1, -22.5) * mm, "end": v(390.1, -24.7) * mm});
            skArc(sketch, "E6.17.2.0", {"start": v(391.16, -48.3) * mm, "mid": v(411.3, -47.2) * mm, "end": v(391.16, -46.1) * mm});
            skLineSegment(sketch, "E6.17.2.1", {"start": v(391.16, -48.3) * mm, "end": v(390.1, -48.3) * mm});
            skLineSegment(sketch, "E6.17.2.2", {"start": v(391.16, -46.1) * mm, "end": v(390.1, -46.1) * mm});
            skLineSegment(sketch, "E6.17.2.3", {"start": v(390.1, -46.1) * mm, "end": v(390.1, -48.3) * mm});
            skArc(sketch, "E6.17.3.0", {"start": v(391.16, -71.9) * mm, "mid": v(411.3, -70.8) * mm, "end": v(391.16, -69.7) * mm});
            skLineSegment(sketch, "E6.17.3.1", {"start": v(391.16, -71.9) * mm, "end": v(390.1, -71.9) * mm});
            skLineSegment(sketch, "E6.17.3.2", {"start": v(391.16, -69.7) * mm, "end": v(390.1, -69.7) * mm});
            skLineSegment(sketch, "E6.17.3.3", {"start": v(390.1, -69.7) * mm, "end": v(390.1, -71.9) * mm});
            skArc(sketch, "E6.17.4.0", {"start": v(391.16, -95.5) * mm, "mid": v(411.3, -94.4) * mm, "end": v(391.16, -93.3) * mm});
            skLineSegment(sketch, "E6.17.4.1", {"start": v(391.16, -95.5) * mm, "end": v(390.1, -95.5) * mm});
            skLineSegment(sketch, "E6.17.4.2", {"start": v(391.16, -93.3) * mm, "end": v(390.1, -93.3) * mm});
            skLineSegment(sketch, "E6.17.4.3", {"start": v(390.1, -93.3) * mm, "end": v(390.1, -95.5) * mm});
            skArc(sketch, "E6.17.5.0", {"start": v(391.16, -119.1) * mm, "mid": v(411.3, -118) * mm, "end": v(391.16, -116.9) * mm});
            skLineSegment(sketch, "E6.17.5.1", {"start": v(391.16, -119.1) * mm, "end": v(390.1, -119.1) * mm});
            skLineSegment(sketch, "E6.17.5.2", {"start": v(391.16, -116.9) * mm, "end": v(390.1, -116.9) * mm});
            skLineSegment(sketch, "E6.17.5.3", {"start": v(390.1, -116.9) * mm, "end": v(390.1, -119.1) * mm});
            skArc(sketch, "E6.17.6.0", {"start": v(391.16, -142.7) * mm, "mid": v(411.3, -141.6) * mm, "end": v(391.16, -140.5) * mm});
            skLineSegment(sketch, "E6.17.6.1", {"start": v(391.16, -142.7) * mm, "end": v(390.1, -142.7) * mm});
            skLineSegment(sketch, "E6.17.6.2", {"start": v(391.16, -140.5) * mm, "end": v(390.1, -140.5) * mm});
            skLineSegment(sketch, "E6.17.6.3", {"start": v(390.1, -140.5) * mm, "end": v(390.1, -142.7) * mm});
            skArc(sketch, "E6.17.7.0", {"start": v(391.16, -166.3) * mm, "mid": v(411.3, -165.2) * mm, "end": v(391.16, -164.1) * mm});
            skLineSegment(sketch, "E6.17.7.1", {"start": v(391.16, -166.3) * mm, "end": v(390.1, -166.3) * mm});
            skLineSegment(sketch, "E6.17.7.2", {"start": v(391.16, -164.1) * mm, "end": v(390.1, -164.1) * mm});
            skLineSegment(sketch, "E6.17.7.3", {"start": v(390.1, -164.1) * mm, "end": v(390.1, -166.3) * mm});
            skArc(sketch, "E6.17.8.0", {"start": v(391.16, -189.9) * mm, "mid": v(411.3, -188.8) * mm, "end": v(391.16, -187.7) * mm});
            skLineSegment(sketch, "E6.17.8.1", {"start": v(391.16, -189.9) * mm, "end": v(390.1, -189.9) * mm});
            skLineSegment(sketch, "E6.17.8.2", {"start": v(391.16, -187.7) * mm, "end": v(390.1, -187.7) * mm});
            skLineSegment(sketch, "E6.17.8.3", {"start": v(390.1, -187.7) * mm, "end": v(390.1, -189.9) * mm});
            skArc(sketch, "E6.17.9.0", {"start": v(391.16, -213.5) * mm, "mid": v(411.3, -212.4) * mm, "end": v(391.16, -211.3) * mm});
            skLineSegment(sketch, "E6.17.9.1", {"start": v(391.16, -213.5) * mm, "end": v(390.1, -213.5) * mm});
            skLineSegment(sketch, "E6.17.9.2", {"start": v(391.16, -211.3) * mm, "end": v(390.1, -211.3) * mm});
            skLineSegment(sketch, "E6.17.9.3", {"start": v(390.1, -211.3) * mm, "end": v(390.1, -213.5) * mm});
            skArc(sketch, "E6.17.10.0", {"start": v(391.16, -237.1) * mm, "mid": v(411.3, -236) * mm, "end": v(391.16, -234.9) * mm});
            skLineSegment(sketch, "E6.17.10.1", {"start": v(391.16, -237.1) * mm, "end": v(390.1, -237.1) * mm});
            skLineSegment(sketch, "E6.17.10.2", {"start": v(391.16, -234.9) * mm, "end": v(390.1, -234.9) * mm});
            skLineSegment(sketch, "E6.17.10.3", {"start": v(390.1, -234.9) * mm, "end": v(390.1, -237.1) * mm});
            skArc(sketch, "E6.17.11.0", {"start": v(391.16, -260.7) * mm, "mid": v(411.3, -259.6) * mm, "end": v(391.16, -258.5) * mm});
            skLineSegment(sketch, "E6.17.11.1", {"start": v(391.16, -260.7) * mm, "end": v(390.1, -260.7) * mm});
            skLineSegment(sketch, "E6.17.11.2", {"start": v(391.16, -258.5) * mm, "end": v(390.1, -258.5) * mm});
            skLineSegment(sketch, "E6.17.11.3", {"start": v(390.1, -258.5) * mm, "end": v(390.1, -260.7) * mm});
            skArc(sketch, "E6.17.12.0", {"start": v(391.16, -284.3) * mm, "mid": v(411.3, -283.2) * mm, "end": v(391.16, -282.1) * mm});
            skLineSegment(sketch, "E6.17.12.1", {"start": v(391.16, -284.3) * mm, "end": v(390.1, -284.3) * mm});
            skLineSegment(sketch, "E6.17.12.2", {"start": v(391.16, -282.1) * mm, "end": v(390.1, -282.1) * mm});
            skLineSegment(sketch, "E6.17.12.3", {"start": v(390.1, -282.1) * mm, "end": v(390.1, -284.3) * mm});
            skArc(sketch, "E6.17.13.0", {"start": v(391.16, -307.9) * mm, "mid": v(411.3, -306.8) * mm, "end": v(391.16, -305.7) * mm});
            skLineSegment(sketch, "E6.17.13.1", {"start": v(391.16, -307.9) * mm, "end": v(390.1, -307.9) * mm});
            skLineSegment(sketch, "E6.17.13.2", {"start": v(391.16, -305.7) * mm, "end": v(390.1, -305.7) * mm});
            skLineSegment(sketch, "E6.17.13.3", {"start": v(390.1, -305.7) * mm, "end": v(390.1, -307.9) * mm});
            skArc(sketch, "E6.18.0.0", {"start": v(414.76, -1.1) * mm, "mid": v(434.9, 0) * mm, "end": v(414.76, 1.1) * mm});
            skLineSegment(sketch, "E6.18.0.1", {"start": v(414.76, -1.1) * mm, "end": v(413.7, -1.1) * mm});
            skLineSegment(sketch, "E6.18.0.2", {"start": v(414.76, 1.1) * mm, "end": v(413.7, 1.1) * mm});
            skLineSegment(sketch, "E6.18.0.3", {"start": v(413.7, 1.1) * mm, "end": v(413.7, -1.1) * mm});
            skArc(sketch, "E6.18.1.0", {"start": v(414.76, -24.7) * mm, "mid": v(434.9, -23.6) * mm, "end": v(414.76, -22.5) * mm});
            skLineSegment(sketch, "E6.18.1.1", {"start": v(414.76, -24.7) * mm, "end": v(413.7, -24.7) * mm});
            skLineSegment(sketch, "E6.18.1.2", {"start": v(414.76, -22.5) * mm, "end": v(413.7, -22.5) * mm});
            skLineSegment(sketch, "E6.18.1.3", {"start": v(413.7, -22.5) * mm, "end": v(413.7, -24.7) * mm});
            skArc(sketch, "E6.18.2.0", {"start": v(414.76, -48.3) * mm, "mid": v(434.9, -47.2) * mm, "end": v(414.76, -46.1) * mm});
            skLineSegment(sketch, "E6.18.2.1", {"start": v(414.76, -48.3) * mm, "end": v(413.7, -48.3) * mm});
            skLineSegment(sketch, "E6.18.2.2", {"start": v(414.76, -46.1) * mm, "end": v(413.7, -46.1) * mm});
            skLineSegment(sketch, "E6.18.2.3", {"start": v(413.7, -46.1) * mm, "end": v(413.7, -48.3) * mm});
            skArc(sketch, "E6.18.3.0", {"start": v(414.76, -71.9) * mm, "mid": v(434.9, -70.8) * mm, "end": v(414.76, -69.7) * mm});
            skLineSegment(sketch, "E6.18.3.1", {"start": v(414.76, -71.9) * mm, "end": v(413.7, -71.9) * mm});
            skLineSegment(sketch, "E6.18.3.2", {"start": v(414.76, -69.7) * mm, "end": v(413.7, -69.7) * mm});
            skLineSegment(sketch, "E6.18.3.3", {"start": v(413.7, -69.7) * mm, "end": v(413.7, -71.9) * mm});
            skArc(sketch, "E6.18.4.0", {"start": v(414.76, -95.5) * mm, "mid": v(434.9, -94.4) * mm, "end": v(414.76, -93.3) * mm});
            skLineSegment(sketch, "E6.18.4.1", {"start": v(414.76, -95.5) * mm, "end": v(413.7, -95.5) * mm});
            skLineSegment(sketch, "E6.18.4.2", {"start": v(414.76, -93.3) * mm, "end": v(413.7, -93.3) * mm});
            skLineSegment(sketch, "E6.18.4.3", {"start": v(413.7, -93.3) * mm, "end": v(413.7, -95.5) * mm});
            skArc(sketch, "E6.18.5.0", {"start": v(414.76, -119.1) * mm, "mid": v(434.9, -118) * mm, "end": v(414.76, -116.9) * mm});
            skLineSegment(sketch, "E6.18.5.1", {"start": v(414.76, -119.1) * mm, "end": v(413.7, -119.1) * mm});
            skLineSegment(sketch, "E6.18.5.2", {"start": v(414.76, -116.9) * mm, "end": v(413.7, -116.9) * mm});
            skLineSegment(sketch, "E6.18.5.3", {"start": v(413.7, -116.9) * mm, "end": v(413.7, -119.1) * mm});
            skArc(sketch, "E6.18.6.0", {"start": v(414.76, -142.7) * mm, "mid": v(434.9, -141.6) * mm, "end": v(414.76, -140.5) * mm});
            skLineSegment(sketch, "E6.18.6.1", {"start": v(414.76, -142.7) * mm, "end": v(413.7, -142.7) * mm});
            skLineSegment(sketch, "E6.18.6.2", {"start": v(414.76, -140.5) * mm, "end": v(413.7, -140.5) * mm});
            skLineSegment(sketch, "E6.18.6.3", {"start": v(413.7, -140.5) * mm, "end": v(413.7, -142.7) * mm});
            skArc(sketch, "E6.18.7.0", {"start": v(414.76, -166.3) * mm, "mid": v(434.9, -165.2) * mm, "end": v(414.76, -164.1) * mm});
            skLineSegment(sketch, "E6.18.7.1", {"start": v(414.76, -166.3) * mm, "end": v(413.7, -166.3) * mm});
            skLineSegment(sketch, "E6.18.7.2", {"start": v(414.76, -164.1) * mm, "end": v(413.7, -164.1) * mm});
            skLineSegment(sketch, "E6.18.7.3", {"start": v(413.7, -164.1) * mm, "end": v(413.7, -166.3) * mm});
            skArc(sketch, "E6.18.8.0", {"start": v(414.76, -189.9) * mm, "mid": v(434.9, -188.8) * mm, "end": v(414.76, -187.7) * mm});
            skLineSegment(sketch, "E6.18.8.1", {"start": v(414.76, -189.9) * mm, "end": v(413.7, -189.9) * mm});
            skLineSegment(sketch, "E6.18.8.2", {"start": v(414.76, -187.7) * mm, "end": v(413.7, -187.7) * mm});
            skLineSegment(sketch, "E6.18.8.3", {"start": v(413.7, -187.7) * mm, "end": v(413.7, -189.9) * mm});
            skArc(sketch, "E6.18.9.0", {"start": v(414.76, -213.5) * mm, "mid": v(434.9, -212.4) * mm, "end": v(414.76, -211.3) * mm});
            skLineSegment(sketch, "E6.18.9.1", {"start": v(414.76, -213.5) * mm, "end": v(413.7, -213.5) * mm});
            skLineSegment(sketch, "E6.18.9.2", {"start": v(414.76, -211.3) * mm, "end": v(413.7, -211.3) * mm});
            skLineSegment(sketch, "E6.18.9.3", {"start": v(413.7, -211.3) * mm, "end": v(413.7, -213.5) * mm});
            skArc(sketch, "E6.18.10.0", {"start": v(414.76, -237.1) * mm, "mid": v(434.9, -236) * mm, "end": v(414.76, -234.9) * mm});
            skLineSegment(sketch, "E6.18.10.1", {"start": v(414.76, -237.1) * mm, "end": v(413.7, -237.1) * mm});
            skLineSegment(sketch, "E6.18.10.2", {"start": v(414.76, -234.9) * mm, "end": v(413.7, -234.9) * mm});
            skLineSegment(sketch, "E6.18.10.3", {"start": v(413.7, -234.9) * mm, "end": v(413.7, -237.1) * mm});
            skArc(sketch, "E6.18.11.0", {"start": v(414.76, -260.7) * mm, "mid": v(434.9, -259.6) * mm, "end": v(414.76, -258.5) * mm});
            skLineSegment(sketch, "E6.18.11.1", {"start": v(414.76, -260.7) * mm, "end": v(413.7, -260.7) * mm});
            skLineSegment(sketch, "E6.18.11.2", {"start": v(414.76, -258.5) * mm, "end": v(413.7, -258.5) * mm});
            skLineSegment(sketch, "E6.18.11.3", {"start": v(413.7, -258.5) * mm, "end": v(413.7, -260.7) * mm});
            skArc(sketch, "E6.18.12.0", {"start": v(414.76, -284.3) * mm, "mid": v(434.9, -283.2) * mm, "end": v(414.76, -282.1) * mm});
            skLineSegment(sketch, "E6.18.12.1", {"start": v(414.76, -284.3) * mm, "end": v(413.7, -284.3) * mm});
            skLineSegment(sketch, "E6.18.12.2", {"start": v(414.76, -282.1) * mm, "end": v(413.7, -282.1) * mm});
            skLineSegment(sketch, "E6.18.12.3", {"start": v(413.7, -282.1) * mm, "end": v(413.7, -284.3) * mm});
            skArc(sketch, "E6.18.13.0", {"start": v(414.76, -307.9) * mm, "mid": v(434.9, -306.8) * mm, "end": v(414.76, -305.7) * mm});
            skLineSegment(sketch, "E6.18.13.1", {"start": v(414.76, -307.9) * mm, "end": v(413.7, -307.9) * mm});
            skLineSegment(sketch, "E6.18.13.2", {"start": v(414.76, -305.7) * mm, "end": v(413.7, -305.7) * mm});
            skLineSegment(sketch, "E6.18.13.3", {"start": v(413.7, -305.7) * mm, "end": v(413.7, -307.9) * mm});
            skArc(sketch, "E6.19.0.0", {"start": v(438.36, -1.1) * mm, "mid": v(458.5, 0) * mm, "end": v(438.36, 1.1) * mm});
            skLineSegment(sketch, "E6.19.0.1", {"start": v(438.36, -1.1) * mm, "end": v(437.3, -1.1) * mm});
            skLineSegment(sketch, "E6.19.0.2", {"start": v(438.36, 1.1) * mm, "end": v(437.3, 1.1) * mm});
            skLineSegment(sketch, "E6.19.0.3", {"start": v(437.3, 1.1) * mm, "end": v(437.3, -1.1) * mm});
            skArc(sketch, "E6.19.1.0", {"start": v(438.36, -24.7) * mm, "mid": v(458.5, -23.6) * mm, "end": v(438.36, -22.5) * mm});
            skLineSegment(sketch, "E6.19.1.1", {"start": v(438.36, -24.7) * mm, "end": v(437.3, -24.7) * mm});
            skLineSegment(sketch, "E6.19.1.2", {"start": v(438.36, -22.5) * mm, "end": v(437.3, -22.5) * mm});
            skLineSegment(sketch, "E6.19.1.3", {"start": v(437.3, -22.5) * mm, "end": v(437.3, -24.7) * mm});
            skArc(sketch, "E6.19.2.0", {"start": v(438.36, -48.3) * mm, "mid": v(458.5, -47.2) * mm, "end": v(438.36, -46.1) * mm});
            skLineSegment(sketch, "E6.19.2.1", {"start": v(438.36, -48.3) * mm, "end": v(437.3, -48.3) * mm});
            skLineSegment(sketch, "E6.19.2.2", {"start": v(438.36, -46.1) * mm, "end": v(437.3, -46.1) * mm});
            skLineSegment(sketch, "E6.19.2.3", {"start": v(437.3, -46.1) * mm, "end": v(437.3, -48.3) * mm});
            skArc(sketch, "E6.19.3.0", {"start": v(438.36, -71.9) * mm, "mid": v(458.5, -70.8) * mm, "end": v(438.36, -69.7) * mm});
            skLineSegment(sketch, "E6.19.3.1", {"start": v(438.36, -71.9) * mm, "end": v(437.3, -71.9) * mm});
            skLineSegment(sketch, "E6.19.3.2", {"start": v(438.36, -69.7) * mm, "end": v(437.3, -69.7) * mm});
            skLineSegment(sketch, "E6.19.3.3", {"start": v(437.3, -69.7) * mm, "end": v(437.3, -71.9) * mm});
            skArc(sketch, "E6.19.4.0", {"start": v(438.36, -95.5) * mm, "mid": v(458.5, -94.4) * mm, "end": v(438.36, -93.3) * mm});
            skLineSegment(sketch, "E6.19.4.1", {"start": v(438.36, -95.5) * mm, "end": v(437.3, -95.5) * mm});
            skLineSegment(sketch, "E6.19.4.2", {"start": v(438.36, -93.3) * mm, "end": v(437.3, -93.3) * mm});
            skLineSegment(sketch, "E6.19.4.3", {"start": v(437.3, -93.3) * mm, "end": v(437.3, -95.5) * mm});
            skArc(sketch, "E6.19.5.0", {"start": v(438.36, -119.1) * mm, "mid": v(458.5, -118) * mm, "end": v(438.36, -116.9) * mm});
            skLineSegment(sketch, "E6.19.5.1", {"start": v(438.36, -119.1) * mm, "end": v(437.3, -119.1) * mm});
            skLineSegment(sketch, "E6.19.5.2", {"start": v(438.36, -116.9) * mm, "end": v(437.3, -116.9) * mm});
            skLineSegment(sketch, "E6.19.5.3", {"start": v(437.3, -116.9) * mm, "end": v(437.3, -119.1) * mm});
            skArc(sketch, "E6.19.6.0", {"start": v(438.36, -142.7) * mm, "mid": v(458.5, -141.6) * mm, "end": v(438.36, -140.5) * mm});
            skLineSegment(sketch, "E6.19.6.1", {"start": v(438.36, -142.7) * mm, "end": v(437.3, -142.7) * mm});
            skLineSegment(sketch, "E6.19.6.2", {"start": v(438.36, -140.5) * mm, "end": v(437.3, -140.5) * mm});
            skLineSegment(sketch, "E6.19.6.3", {"start": v(437.3, -140.5) * mm, "end": v(437.3, -142.7) * mm});
            skArc(sketch, "E6.19.7.0", {"start": v(438.36, -166.3) * mm, "mid": v(458.5, -165.2) * mm, "end": v(438.36, -164.1) * mm});
            skLineSegment(sketch, "E6.19.7.1", {"start": v(438.36, -166.3) * mm, "end": v(437.3, -166.3) * mm});
            skLineSegment(sketch, "E6.19.7.2", {"start": v(438.36, -164.1) * mm, "end": v(437.3, -164.1) * mm});
            skLineSegment(sketch, "E6.19.7.3", {"start": v(437.3, -164.1) * mm, "end": v(437.3, -166.3) * mm});
            skArc(sketch, "E6.19.8.0", {"start": v(438.36, -189.9) * mm, "mid": v(458.5, -188.8) * mm, "end": v(438.36, -187.7) * mm});
            skLineSegment(sketch, "E6.19.8.1", {"start": v(438.36, -189.9) * mm, "end": v(437.3, -189.9) * mm});
            skLineSegment(sketch, "E6.19.8.2", {"start": v(438.36, -187.7) * mm, "end": v(437.3, -187.7) * mm});
            skLineSegment(sketch, "E6.19.8.3", {"start": v(437.3, -187.7) * mm, "end": v(437.3, -189.9) * mm});
            skArc(sketch, "E6.19.9.0", {"start": v(438.36, -213.5) * mm, "mid": v(458.5, -212.4) * mm, "end": v(438.36, -211.3) * mm});
            skLineSegment(sketch, "E6.19.9.1", {"start": v(438.36, -213.5) * mm, "end": v(437.3, -213.5) * mm});
            skLineSegment(sketch, "E6.19.9.2", {"start": v(438.36, -211.3) * mm, "end": v(437.3, -211.3) * mm});
            skLineSegment(sketch, "E6.19.9.3", {"start": v(437.3, -211.3) * mm, "end": v(437.3, -213.5) * mm});
            skArc(sketch, "E6.19.10.0", {"start": v(438.36, -237.1) * mm, "mid": v(458.5, -236) * mm, "end": v(438.36, -234.9) * mm});
            skLineSegment(sketch, "E6.19.10.1", {"start": v(438.36, -237.1) * mm, "end": v(437.3, -237.1) * mm});
            skLineSegment(sketch, "E6.19.10.2", {"start": v(438.36, -234.9) * mm, "end": v(437.3, -234.9) * mm});
            skLineSegment(sketch, "E6.19.10.3", {"start": v(437.3, -234.9) * mm, "end": v(437.3, -237.1) * mm});
            skArc(sketch, "E6.19.11.0", {"start": v(438.36, -260.7) * mm, "mid": v(458.5, -259.6) * mm, "end": v(438.36, -258.5) * mm});
            skLineSegment(sketch, "E6.19.11.1", {"start": v(438.36, -260.7) * mm, "end": v(437.3, -260.7) * mm});
            skLineSegment(sketch, "E6.19.11.2", {"start": v(438.36, -258.5) * mm, "end": v(437.3, -258.5) * mm});
            skLineSegment(sketch, "E6.19.11.3", {"start": v(437.3, -258.5) * mm, "end": v(437.3, -260.7) * mm});
            skArc(sketch, "E6.19.12.0", {"start": v(438.36, -284.3) * mm, "mid": v(458.5, -283.2) * mm, "end": v(438.36, -282.1) * mm});
            skLineSegment(sketch, "E6.19.12.1", {"start": v(438.36, -284.3) * mm, "end": v(437.3, -284.3) * mm});
            skLineSegment(sketch, "E6.19.12.2", {"start": v(438.36, -282.1) * mm, "end": v(437.3, -282.1) * mm});
            skLineSegment(sketch, "E6.19.12.3", {"start": v(437.3, -282.1) * mm, "end": v(437.3, -284.3) * mm});
            skArc(sketch, "E6.19.13.0", {"start": v(438.36, -307.9) * mm, "mid": v(458.5, -306.8) * mm, "end": v(438.36, -305.7) * mm});
            skLineSegment(sketch, "E6.19.13.1", {"start": v(438.36, -307.9) * mm, "end": v(437.3, -307.9) * mm});
            skLineSegment(sketch, "E6.19.13.2", {"start": v(438.36, -305.7) * mm, "end": v(437.3, -305.7) * mm});
            skLineSegment(sketch, "E6.19.13.3", {"start": v(437.3, -305.7) * mm, "end": v(437.3, -307.9) * mm});
            skArc(sketch, "E6.20.0.0", {"start": v(461.96, -1.1) * mm, "mid": v(482.1, 0) * mm, "end": v(461.96, 1.1) * mm});
            skLineSegment(sketch, "E6.20.0.1", {"start": v(461.96, -1.1) * mm, "end": v(460.9, -1.1) * mm});
            skLineSegment(sketch, "E6.20.0.2", {"start": v(461.96, 1.1) * mm, "end": v(460.9, 1.1) * mm});
            skLineSegment(sketch, "E6.20.0.3", {"start": v(460.9, 1.1) * mm, "end": v(460.9, -1.1) * mm});
            skArc(sketch, "E6.20.1.0", {"start": v(461.96, -24.7) * mm, "mid": v(482.1, -23.6) * mm, "end": v(461.96, -22.5) * mm});
            skLineSegment(sketch, "E6.20.1.1", {"start": v(461.96, -24.7) * mm, "end": v(460.9, -24.7) * mm});
            skLineSegment(sketch, "E6.20.1.2", {"start": v(461.96, -22.5) * mm, "end": v(460.9, -22.5) * mm});
            skLineSegment(sketch, "E6.20.1.3", {"start": v(460.9, -22.5) * mm, "end": v(460.9, -24.7) * mm});
            skArc(sketch, "E6.20.2.0", {"start": v(461.96, -48.3) * mm, "mid": v(482.1, -47.2) * mm, "end": v(461.96, -46.1) * mm});
            skLineSegment(sketch, "E6.20.2.1", {"start": v(461.96, -48.3) * mm, "end": v(460.9, -48.3) * mm});
            skLineSegment(sketch, "E6.20.2.2", {"start": v(461.96, -46.1) * mm, "end": v(460.9, -46.1) * mm});
            skLineSegment(sketch, "E6.20.2.3", {"start": v(460.9, -46.1) * mm, "end": v(460.9, -48.3) * mm});
            skArc(sketch, "E6.20.3.0", {"start": v(461.96, -71.9) * mm, "mid": v(482.1, -70.8) * mm, "end": v(461.96, -69.7) * mm});
            skLineSegment(sketch, "E6.20.3.1", {"start": v(461.96, -71.9) * mm, "end": v(460.9, -71.9) * mm});
            skLineSegment(sketch, "E6.20.3.2", {"start": v(461.96, -69.7) * mm, "end": v(460.9, -69.7) * mm});
            skLineSegment(sketch, "E6.20.3.3", {"start": v(460.9, -69.7) * mm, "end": v(460.9, -71.9) * mm});
            skArc(sketch, "E6.20.4.0", {"start": v(461.96, -95.5) * mm, "mid": v(482.1, -94.4) * mm, "end": v(461.96, -93.3) * mm});
            skLineSegment(sketch, "E6.20.4.1", {"start": v(461.96, -95.5) * mm, "end": v(460.9, -95.5) * mm});
            skLineSegment(sketch, "E6.20.4.2", {"start": v(461.96, -93.3) * mm, "end": v(460.9, -93.3) * mm});
            skLineSegment(sketch, "E6.20.4.3", {"start": v(460.9, -93.3) * mm, "end": v(460.9, -95.5) * mm});
            skArc(sketch, "E6.20.5.0", {"start": v(461.96, -119.1) * mm, "mid": v(482.1, -118) * mm, "end": v(461.96, -116.9) * mm});
            skLineSegment(sketch, "E6.20.5.1", {"start": v(461.96, -119.1) * mm, "end": v(460.9, -119.1) * mm});
            skLineSegment(sketch, "E6.20.5.2", {"start": v(461.96, -116.9) * mm, "end": v(460.9, -116.9) * mm});
            skLineSegment(sketch, "E6.20.5.3", {"start": v(460.9, -116.9) * mm, "end": v(460.9, -119.1) * mm});
            skArc(sketch, "E6.20.6.0", {"start": v(461.96, -142.7) * mm, "mid": v(482.1, -141.6) * mm, "end": v(461.96, -140.5) * mm});
            skLineSegment(sketch, "E6.20.6.1", {"start": v(461.96, -142.7) * mm, "end": v(460.9, -142.7) * mm});
            skLineSegment(sketch, "E6.20.6.2", {"start": v(461.96, -140.5) * mm, "end": v(460.9, -140.5) * mm});
            skLineSegment(sketch, "E6.20.6.3", {"start": v(460.9, -140.5) * mm, "end": v(460.9, -142.7) * mm});
            skArc(sketch, "E6.20.7.0", {"start": v(461.96, -166.3) * mm, "mid": v(482.1, -165.2) * mm, "end": v(461.96, -164.1) * mm});
            skLineSegment(sketch, "E6.20.7.1", {"start": v(461.96, -166.3) * mm, "end": v(460.9, -166.3) * mm});
            skLineSegment(sketch, "E6.20.7.2", {"start": v(461.96, -164.1) * mm, "end": v(460.9, -164.1) * mm});
            skLineSegment(sketch, "E6.20.7.3", {"start": v(460.9, -164.1) * mm, "end": v(460.9, -166.3) * mm});
            skArc(sketch, "E6.20.8.0", {"start": v(461.96, -189.9) * mm, "mid": v(482.1, -188.8) * mm, "end": v(461.96, -187.7) * mm});
            skLineSegment(sketch, "E6.20.8.1", {"start": v(461.96, -189.9) * mm, "end": v(460.9, -189.9) * mm});
            skLineSegment(sketch, "E6.20.8.2", {"start": v(461.96, -187.7) * mm, "end": v(460.9, -187.7) * mm});
            skLineSegment(sketch, "E6.20.8.3", {"start": v(460.9, -187.7) * mm, "end": v(460.9, -189.9) * mm});
            skArc(sketch, "E6.20.9.0", {"start": v(461.96, -213.5) * mm, "mid": v(482.1, -212.4) * mm, "end": v(461.96, -211.3) * mm});
            skLineSegment(sketch, "E6.20.9.1", {"start": v(461.96, -213.5) * mm, "end": v(460.9, -213.5) * mm});
            skLineSegment(sketch, "E6.20.9.2", {"start": v(461.96, -211.3) * mm, "end": v(460.9, -211.3) * mm});
            skLineSegment(sketch, "E6.20.9.3", {"start": v(460.9, -211.3) * mm, "end": v(460.9, -213.5) * mm});
            skArc(sketch, "E6.20.10.0", {"start": v(461.96, -237.1) * mm, "mid": v(482.1, -236) * mm, "end": v(461.96, -234.9) * mm});
            skLineSegment(sketch, "E6.20.10.1", {"start": v(461.96, -237.1) * mm, "end": v(460.9, -237.1) * mm});
            skLineSegment(sketch, "E6.20.10.2", {"start": v(461.96, -234.9) * mm, "end": v(460.9, -234.9) * mm});
            skLineSegment(sketch, "E6.20.10.3", {"start": v(460.9, -234.9) * mm, "end": v(460.9, -237.1) * mm});
            skArc(sketch, "E6.20.11.0", {"start": v(461.96, -260.7) * mm, "mid": v(482.1, -259.6) * mm, "end": v(461.96, -258.5) * mm});
            skLineSegment(sketch, "E6.20.11.1", {"start": v(461.96, -260.7) * mm, "end": v(460.9, -260.7) * mm});
            skLineSegment(sketch, "E6.20.11.2", {"start": v(461.96, -258.5) * mm, "end": v(460.9, -258.5) * mm});
            skLineSegment(sketch, "E6.20.11.3", {"start": v(460.9, -258.5) * mm, "end": v(460.9, -260.7) * mm});
            skArc(sketch, "E6.20.12.0", {"start": v(461.96, -284.3) * mm, "mid": v(482.1, -283.2) * mm, "end": v(461.96, -282.1) * mm});
            skLineSegment(sketch, "E6.20.12.1", {"start": v(461.96, -284.3) * mm, "end": v(460.9, -284.3) * mm});
            skLineSegment(sketch, "E6.20.12.2", {"start": v(461.96, -282.1) * mm, "end": v(460.9, -282.1) * mm});
            skLineSegment(sketch, "E6.20.12.3", {"start": v(460.9, -282.1) * mm, "end": v(460.9, -284.3) * mm});
            skArc(sketch, "E6.20.13.0", {"start": v(461.96, -307.9) * mm, "mid": v(482.1, -306.8) * mm, "end": v(461.96, -305.7) * mm});
            skLineSegment(sketch, "E6.20.13.1", {"start": v(461.96, -307.9) * mm, "end": v(460.9, -307.9) * mm});
            skLineSegment(sketch, "E6.20.13.2", {"start": v(461.96, -305.7) * mm, "end": v(460.9, -305.7) * mm});
            skLineSegment(sketch, "E6.20.13.3", {"start": v(460.9, -305.7) * mm, "end": v(460.9, -307.9) * mm});
            skArc(sketch, "E6.21.0.0", {"start": v(485.56, -1.1) * mm, "mid": v(505.7, 0) * mm, "end": v(485.56, 1.1) * mm});
            skLineSegment(sketch, "E6.21.0.1", {"start": v(485.56, -1.1) * mm, "end": v(484.5, -1.1) * mm});
            skLineSegment(sketch, "E6.21.0.2", {"start": v(485.56, 1.1) * mm, "end": v(484.5, 1.1) * mm});
            skLineSegment(sketch, "E6.21.0.3", {"start": v(484.5, 1.1) * mm, "end": v(484.5, -1.1) * mm});
            skArc(sketch, "E6.21.1.0", {"start": v(485.56, -24.7) * mm, "mid": v(505.7, -23.6) * mm, "end": v(485.56, -22.5) * mm});
            skLineSegment(sketch, "E6.21.1.1", {"start": v(485.56, -24.7) * mm, "end": v(484.5, -24.7) * mm});
            skLineSegment(sketch, "E6.21.1.2", {"start": v(485.56, -22.5) * mm, "end": v(484.5, -22.5) * mm});
            skLineSegment(sketch, "E6.21.1.3", {"start": v(484.5, -22.5) * mm, "end": v(484.5, -24.7) * mm});
            skArc(sketch, "E6.21.2.0", {"start": v(485.56, -48.3) * mm, "mid": v(505.7, -47.2) * mm, "end": v(485.56, -46.1) * mm});
            skLineSegment(sketch, "E6.21.2.1", {"start": v(485.56, -48.3) * mm, "end": v(484.5, -48.3) * mm});
            skLineSegment(sketch, "E6.21.2.2", {"start": v(485.56, -46.1) * mm, "end": v(484.5, -46.1) * mm});
            skLineSegment(sketch, "E6.21.2.3", {"start": v(484.5, -46.1) * mm, "end": v(484.5, -48.3) * mm});
            skArc(sketch, "E6.21.3.0", {"start": v(485.56, -71.9) * mm, "mid": v(505.7, -70.8) * mm, "end": v(485.56, -69.7) * mm});
            skLineSegment(sketch, "E6.21.3.1", {"start": v(485.56, -71.9) * mm, "end": v(484.5, -71.9) * mm});
            skLineSegment(sketch, "E6.21.3.2", {"start": v(485.56, -69.7) * mm, "end": v(484.5, -69.7) * mm});
            skLineSegment(sketch, "E6.21.3.3", {"start": v(484.5, -69.7) * mm, "end": v(484.5, -71.9) * mm});
            skArc(sketch, "E6.21.4.0", {"start": v(485.56, -95.5) * mm, "mid": v(505.7, -94.4) * mm, "end": v(485.56, -93.3) * mm});
            skLineSegment(sketch, "E6.21.4.1", {"start": v(485.56, -95.5) * mm, "end": v(484.5, -95.5) * mm});
            skLineSegment(sketch, "E6.21.4.2", {"start": v(485.56, -93.3) * mm, "end": v(484.5, -93.3) * mm});
            skLineSegment(sketch, "E6.21.4.3", {"start": v(484.5, -93.3) * mm, "end": v(484.5, -95.5) * mm});
            skArc(sketch, "E6.21.5.0", {"start": v(485.56, -119.1) * mm, "mid": v(505.7, -118) * mm, "end": v(485.56, -116.9) * mm});
            skLineSegment(sketch, "E6.21.5.1", {"start": v(485.56, -119.1) * mm, "end": v(484.5, -119.1) * mm});
            skLineSegment(sketch, "E6.21.5.2", {"start": v(485.56, -116.9) * mm, "end": v(484.5, -116.9) * mm});
            skLineSegment(sketch, "E6.21.5.3", {"start": v(484.5, -116.9) * mm, "end": v(484.5, -119.1) * mm});
            skArc(sketch, "E6.21.6.0", {"start": v(485.56, -142.7) * mm, "mid": v(505.7, -141.6) * mm, "end": v(485.56, -140.5) * mm});
            skLineSegment(sketch, "E6.21.6.1", {"start": v(485.56, -142.7) * mm, "end": v(484.5, -142.7) * mm});
            skLineSegment(sketch, "E6.21.6.2", {"start": v(485.56, -140.5) * mm, "end": v(484.5, -140.5) * mm});
            skLineSegment(sketch, "E6.21.6.3", {"start": v(484.5, -140.5) * mm, "end": v(484.5, -142.7) * mm});
            skArc(sketch, "E6.21.7.0", {"start": v(485.56, -166.3) * mm, "mid": v(505.7, -165.2) * mm, "end": v(485.56, -164.1) * mm});
            skLineSegment(sketch, "E6.21.7.1", {"start": v(485.56, -166.3) * mm, "end": v(484.5, -166.3) * mm});
            skLineSegment(sketch, "E6.21.7.2", {"start": v(485.56, -164.1) * mm, "end": v(484.5, -164.1) * mm});
            skLineSegment(sketch, "E6.21.7.3", {"start": v(484.5, -164.1) * mm, "end": v(484.5, -166.3) * mm});
            skArc(sketch, "E6.21.8.0", {"start": v(485.56, -189.9) * mm, "mid": v(505.7, -188.8) * mm, "end": v(485.56, -187.7) * mm});
            skLineSegment(sketch, "E6.21.8.1", {"start": v(485.56, -189.9) * mm, "end": v(484.5, -189.9) * mm});
            skLineSegment(sketch, "E6.21.8.2", {"start": v(485.56, -187.7) * mm, "end": v(484.5, -187.7) * mm});
            skLineSegment(sketch, "E6.21.8.3", {"start": v(484.5, -187.7) * mm, "end": v(484.5, -189.9) * mm});
            skArc(sketch, "E6.21.9.0", {"start": v(485.56, -213.5) * mm, "mid": v(505.7, -212.4) * mm, "end": v(485.56, -211.3) * mm});
            skLineSegment(sketch, "E6.21.9.1", {"start": v(485.56, -213.5) * mm, "end": v(484.5, -213.5) * mm});
            skLineSegment(sketch, "E6.21.9.2", {"start": v(485.56, -211.3) * mm, "end": v(484.5, -211.3) * mm});
            skLineSegment(sketch, "E6.21.9.3", {"start": v(484.5, -211.3) * mm, "end": v(484.5, -213.5) * mm});
            skArc(sketch, "E6.21.10.0", {"start": v(485.56, -237.1) * mm, "mid": v(505.7, -236) * mm, "end": v(485.56, -234.9) * mm});
            skLineSegment(sketch, "E6.21.10.1", {"start": v(485.56, -237.1) * mm, "end": v(484.5, -237.1) * mm});
            skLineSegment(sketch, "E6.21.10.2", {"start": v(485.56, -234.9) * mm, "end": v(484.5, -234.9) * mm});
            skLineSegment(sketch, "E6.21.10.3", {"start": v(484.5, -234.9) * mm, "end": v(484.5, -237.1) * mm});
            skArc(sketch, "E6.21.11.0", {"start": v(485.56, -260.7) * mm, "mid": v(505.7, -259.6) * mm, "end": v(485.56, -258.5) * mm});
            skLineSegment(sketch, "E6.21.11.1", {"start": v(485.56, -260.7) * mm, "end": v(484.5, -260.7) * mm});
            skLineSegment(sketch, "E6.21.11.2", {"start": v(485.56, -258.5) * mm, "end": v(484.5, -258.5) * mm});
            skLineSegment(sketch, "E6.21.11.3", {"start": v(484.5, -258.5) * mm, "end": v(484.5, -260.7) * mm});
            skArc(sketch, "E6.21.12.0", {"start": v(485.56, -284.3) * mm, "mid": v(505.7, -283.2) * mm, "end": v(485.56, -282.1) * mm});
            skLineSegment(sketch, "E6.21.12.1", {"start": v(485.56, -284.3) * mm, "end": v(484.5, -284.3) * mm});
            skLineSegment(sketch, "E6.21.12.2", {"start": v(485.56, -282.1) * mm, "end": v(484.5, -282.1) * mm});
            skLineSegment(sketch, "E6.21.12.3", {"start": v(484.5, -282.1) * mm, "end": v(484.5, -284.3) * mm});
            skArc(sketch, "E6.21.13.0", {"start": v(485.56, -307.9) * mm, "mid": v(505.7, -306.8) * mm, "end": v(485.56, -305.7) * mm});
            skLineSegment(sketch, "E6.21.13.1", {"start": v(485.56, -307.9) * mm, "end": v(484.5, -307.9) * mm});
            skLineSegment(sketch, "E6.21.13.2", {"start": v(485.56, -305.7) * mm, "end": v(484.5, -305.7) * mm});
            skLineSegment(sketch, "E6.21.13.3", {"start": v(484.5, -305.7) * mm, "end": v(484.5, -307.9) * mm});
            skArc(sketch, "E6.22.0.0", {"start": v(509.16, -1.1) * mm, "mid": v(529.3, 0) * mm, "end": v(509.16, 1.1) * mm});
            skLineSegment(sketch, "E6.22.0.1", {"start": v(509.16, -1.1) * mm, "end": v(508.1, -1.1) * mm});
            skLineSegment(sketch, "E6.22.0.2", {"start": v(509.16, 1.1) * mm, "end": v(508.1, 1.1) * mm});
            skLineSegment(sketch, "E6.22.0.3", {"start": v(508.1, 1.1) * mm, "end": v(508.1, -1.1) * mm});
            skArc(sketch, "E6.22.1.0", {"start": v(509.16, -24.7) * mm, "mid": v(529.3, -23.6) * mm, "end": v(509.16, -22.5) * mm});
            skLineSegment(sketch, "E6.22.1.1", {"start": v(509.16, -24.7) * mm, "end": v(508.1, -24.7) * mm});
            skLineSegment(sketch, "E6.22.1.2", {"start": v(509.16, -22.5) * mm, "end": v(508.1, -22.5) * mm});
            skLineSegment(sketch, "E6.22.1.3", {"start": v(508.1, -22.5) * mm, "end": v(508.1, -24.7) * mm});
            skArc(sketch, "E6.22.2.0", {"start": v(509.16, -48.3) * mm, "mid": v(529.3, -47.2) * mm, "end": v(509.16, -46.1) * mm});
            skLineSegment(sketch, "E6.22.2.1", {"start": v(509.16, -48.3) * mm, "end": v(508.1, -48.3) * mm});
            skLineSegment(sketch, "E6.22.2.2", {"start": v(509.16, -46.1) * mm, "end": v(508.1, -46.1) * mm});
            skLineSegment(sketch, "E6.22.2.3", {"start": v(508.1, -46.1) * mm, "end": v(508.1, -48.3) * mm});
            skArc(sketch, "E6.22.3.0", {"start": v(509.16, -71.9) * mm, "mid": v(529.3, -70.8) * mm, "end": v(509.16, -69.7) * mm});
            skLineSegment(sketch, "E6.22.3.1", {"start": v(509.16, -71.9) * mm, "end": v(508.1, -71.9) * mm});
            skLineSegment(sketch, "E6.22.3.2", {"start": v(509.16, -69.7) * mm, "end": v(508.1, -69.7) * mm});
            skLineSegment(sketch, "E6.22.3.3", {"start": v(508.1, -69.7) * mm, "end": v(508.1, -71.9) * mm});
            skArc(sketch, "E6.22.4.0", {"start": v(509.16, -95.5) * mm, "mid": v(529.3, -94.4) * mm, "end": v(509.16, -93.3) * mm});
            skLineSegment(sketch, "E6.22.4.1", {"start": v(509.16, -95.5) * mm, "end": v(508.1, -95.5) * mm});
            skLineSegment(sketch, "E6.22.4.2", {"start": v(509.16, -93.3) * mm, "end": v(508.1, -93.3) * mm});
            skLineSegment(sketch, "E6.22.4.3", {"start": v(508.1, -93.3) * mm, "end": v(508.1, -95.5) * mm});
            skArc(sketch, "E6.22.5.0", {"start": v(509.16, -119.1) * mm, "mid": v(529.3, -118) * mm, "end": v(509.16, -116.9) * mm});
            skLineSegment(sketch, "E6.22.5.1", {"start": v(509.16, -119.1) * mm, "end": v(508.1, -119.1) * mm});
            skLineSegment(sketch, "E6.22.5.2", {"start": v(509.16, -116.9) * mm, "end": v(508.1, -116.9) * mm});
            skLineSegment(sketch, "E6.22.5.3", {"start": v(508.1, -116.9) * mm, "end": v(508.1, -119.1) * mm});
            skArc(sketch, "E6.22.6.0", {"start": v(509.16, -142.7) * mm, "mid": v(529.3, -141.6) * mm, "end": v(509.16, -140.5) * mm});
            skLineSegment(sketch, "E6.22.6.1", {"start": v(509.16, -142.7) * mm, "end": v(508.1, -142.7) * mm});
            skLineSegment(sketch, "E6.22.6.2", {"start": v(509.16, -140.5) * mm, "end": v(508.1, -140.5) * mm});
            skLineSegment(sketch, "E6.22.6.3", {"start": v(508.1, -140.5) * mm, "end": v(508.1, -142.7) * mm});
            skArc(sketch, "E6.22.7.0", {"start": v(509.16, -166.3) * mm, "mid": v(529.3, -165.2) * mm, "end": v(509.16, -164.1) * mm});
            skLineSegment(sketch, "E6.22.7.1", {"start": v(509.16, -166.3) * mm, "end": v(508.1, -166.3) * mm});
            skLineSegment(sketch, "E6.22.7.2", {"start": v(509.16, -164.1) * mm, "end": v(508.1, -164.1) * mm});
            skLineSegment(sketch, "E6.22.7.3", {"start": v(508.1, -164.1) * mm, "end": v(508.1, -166.3) * mm});
            skArc(sketch, "E6.22.8.0", {"start": v(509.16, -189.9) * mm, "mid": v(529.3, -188.8) * mm, "end": v(509.16, -187.7) * mm});
            skLineSegment(sketch, "E6.22.8.1", {"start": v(509.16, -189.9) * mm, "end": v(508.1, -189.9) * mm});
            skLineSegment(sketch, "E6.22.8.2", {"start": v(509.16, -187.7) * mm, "end": v(508.1, -187.7) * mm});
            skLineSegment(sketch, "E6.22.8.3", {"start": v(508.1, -187.7) * mm, "end": v(508.1, -189.9) * mm});
            skArc(sketch, "E6.22.9.0", {"start": v(509.16, -213.5) * mm, "mid": v(529.3, -212.4) * mm, "end": v(509.16, -211.3) * mm});
            skLineSegment(sketch, "E6.22.9.1", {"start": v(509.16, -213.5) * mm, "end": v(508.1, -213.5) * mm});
            skLineSegment(sketch, "E6.22.9.2", {"start": v(509.16, -211.3) * mm, "end": v(508.1, -211.3) * mm});
            skLineSegment(sketch, "E6.22.9.3", {"start": v(508.1, -211.3) * mm, "end": v(508.1, -213.5) * mm});
            skArc(sketch, "E6.22.10.0", {"start": v(509.16, -237.1) * mm, "mid": v(529.3, -236) * mm, "end": v(509.16, -234.9) * mm});
            skLineSegment(sketch, "E6.22.10.1", {"start": v(509.16, -237.1) * mm, "end": v(508.1, -237.1) * mm});
            skLineSegment(sketch, "E6.22.10.2", {"start": v(509.16, -234.9) * mm, "end": v(508.1, -234.9) * mm});
            skLineSegment(sketch, "E6.22.10.3", {"start": v(508.1, -234.9) * mm, "end": v(508.1, -237.1) * mm});
            skArc(sketch, "E6.22.11.0", {"start": v(509.16, -260.7) * mm, "mid": v(529.3, -259.6) * mm, "end": v(509.16, -258.5) * mm});
            skLineSegment(sketch, "E6.22.11.1", {"start": v(509.16, -260.7) * mm, "end": v(508.1, -260.7) * mm});
            skLineSegment(sketch, "E6.22.11.2", {"start": v(509.16, -258.5) * mm, "end": v(508.1, -258.5) * mm});
            skLineSegment(sketch, "E6.22.11.3", {"start": v(508.1, -258.5) * mm, "end": v(508.1, -260.7) * mm});
            skArc(sketch, "E6.22.12.0", {"start": v(509.16, -284.3) * mm, "mid": v(529.3, -283.2) * mm, "end": v(509.16, -282.1) * mm});
            skLineSegment(sketch, "E6.22.12.1", {"start": v(509.16, -284.3) * mm, "end": v(508.1, -284.3) * mm});
            skLineSegment(sketch, "E6.22.12.2", {"start": v(509.16, -282.1) * mm, "end": v(508.1, -282.1) * mm});
            skLineSegment(sketch, "E6.22.12.3", {"start": v(508.1, -282.1) * mm, "end": v(508.1, -284.3) * mm});
            skArc(sketch, "E6.22.13.0", {"start": v(509.16, -307.9) * mm, "mid": v(529.3, -306.8) * mm, "end": v(509.16, -305.7) * mm});
            skLineSegment(sketch, "E6.22.13.1", {"start": v(509.16, -307.9) * mm, "end": v(508.1, -307.9) * mm});
            skLineSegment(sketch, "E6.22.13.2", {"start": v(509.16, -305.7) * mm, "end": v(508.1, -305.7) * mm});
            skLineSegment(sketch, "E6.22.13.3", {"start": v(508.1, -305.7) * mm, "end": v(508.1, -307.9) * mm});
            skArc(sketch, "E6.23.0.0", {"start": v(532.76, -1.1) * mm, "mid": v(552.9, 0) * mm, "end": v(532.76, 1.1) * mm});
            skLineSegment(sketch, "E6.23.0.1", {"start": v(532.76, -1.1) * mm, "end": v(531.7, -1.1) * mm});
            skLineSegment(sketch, "E6.23.0.2", {"start": v(532.76, 1.1) * mm, "end": v(531.7, 1.1) * mm});
            skLineSegment(sketch, "E6.23.0.3", {"start": v(531.7, 1.1) * mm, "end": v(531.7, -1.1) * mm});
            skArc(sketch, "E6.23.1.0", {"start": v(532.76, -24.7) * mm, "mid": v(552.9, -23.6) * mm, "end": v(532.76, -22.5) * mm});
            skLineSegment(sketch, "E6.23.1.1", {"start": v(532.76, -24.7) * mm, "end": v(531.7, -24.7) * mm});
            skLineSegment(sketch, "E6.23.1.2", {"start": v(532.76, -22.5) * mm, "end": v(531.7, -22.5) * mm});
            skLineSegment(sketch, "E6.23.1.3", {"start": v(531.7, -22.5) * mm, "end": v(531.7, -24.7) * mm});
            skArc(sketch, "E6.23.2.0", {"start": v(532.76, -48.3) * mm, "mid": v(552.9, -47.2) * mm, "end": v(532.76, -46.1) * mm});
            skLineSegment(sketch, "E6.23.2.1", {"start": v(532.76, -48.3) * mm, "end": v(531.7, -48.3) * mm});
            skLineSegment(sketch, "E6.23.2.2", {"start": v(532.76, -46.1) * mm, "end": v(531.7, -46.1) * mm});
            skLineSegment(sketch, "E6.23.2.3", {"start": v(531.7, -46.1) * mm, "end": v(531.7, -48.3) * mm});
            skArc(sketch, "E6.23.3.0", {"start": v(532.76, -71.9) * mm, "mid": v(552.9, -70.8) * mm, "end": v(532.76, -69.7) * mm});
            skLineSegment(sketch, "E6.23.3.1", {"start": v(532.76, -71.9) * mm, "end": v(531.7, -71.9) * mm});
            skLineSegment(sketch, "E6.23.3.2", {"start": v(532.76, -69.7) * mm, "end": v(531.7, -69.7) * mm});
            skLineSegment(sketch, "E6.23.3.3", {"start": v(531.7, -69.7) * mm, "end": v(531.7, -71.9) * mm});
            skArc(sketch, "E6.23.4.0", {"start": v(532.76, -95.5) * mm, "mid": v(552.9, -94.4) * mm, "end": v(532.76, -93.3) * mm});
            skLineSegment(sketch, "E6.23.4.1", {"start": v(532.76, -95.5) * mm, "end": v(531.7, -95.5) * mm});
            skLineSegment(sketch, "E6.23.4.2", {"start": v(532.76, -93.3) * mm, "end": v(531.7, -93.3) * mm});
            skLineSegment(sketch, "E6.23.4.3", {"start": v(531.7, -93.3) * mm, "end": v(531.7, -95.5) * mm});
            skArc(sketch, "E6.23.5.0", {"start": v(532.76, -119.1) * mm, "mid": v(552.9, -118) * mm, "end": v(532.76, -116.9) * mm});
            skLineSegment(sketch, "E6.23.5.1", {"start": v(532.76, -119.1) * mm, "end": v(531.7, -119.1) * mm});
            skLineSegment(sketch, "E6.23.5.2", {"start": v(532.76, -116.9) * mm, "end": v(531.7, -116.9) * mm});
            skLineSegment(sketch, "E6.23.5.3", {"start": v(531.7, -116.9) * mm, "end": v(531.7, -119.1) * mm});
            skArc(sketch, "E6.23.6.0", {"start": v(532.76, -142.7) * mm, "mid": v(552.9, -141.6) * mm, "end": v(532.76, -140.5) * mm});
            skLineSegment(sketch, "E6.23.6.1", {"start": v(532.76, -142.7) * mm, "end": v(531.7, -142.7) * mm});
            skLineSegment(sketch, "E6.23.6.2", {"start": v(532.76, -140.5) * mm, "end": v(531.7, -140.5) * mm});
            skLineSegment(sketch, "E6.23.6.3", {"start": v(531.7, -140.5) * mm, "end": v(531.7, -142.7) * mm});
            skArc(sketch, "E6.23.7.0", {"start": v(532.76, -166.3) * mm, "mid": v(552.9, -165.2) * mm, "end": v(532.76, -164.1) * mm});
            skLineSegment(sketch, "E6.23.7.1", {"start": v(532.76, -166.3) * mm, "end": v(531.7, -166.3) * mm});
            skLineSegment(sketch, "E6.23.7.2", {"start": v(532.76, -164.1) * mm, "end": v(531.7, -164.1) * mm});
            skLineSegment(sketch, "E6.23.7.3", {"start": v(531.7, -164.1) * mm, "end": v(531.7, -166.3) * mm});
            skArc(sketch, "E6.23.8.0", {"start": v(532.76, -189.9) * mm, "mid": v(552.9, -188.8) * mm, "end": v(532.76, -187.7) * mm});
            skLineSegment(sketch, "E6.23.8.1", {"start": v(532.76, -189.9) * mm, "end": v(531.7, -189.9) * mm});
            skLineSegment(sketch, "E6.23.8.2", {"start": v(532.76, -187.7) * mm, "end": v(531.7, -187.7) * mm});
            skLineSegment(sketch, "E6.23.8.3", {"start": v(531.7, -187.7) * mm, "end": v(531.7, -189.9) * mm});
            skArc(sketch, "E6.23.9.0", {"start": v(532.76, -213.5) * mm, "mid": v(552.9, -212.4) * mm, "end": v(532.76, -211.3) * mm});
            skLineSegment(sketch, "E6.23.9.1", {"start": v(532.76, -213.5) * mm, "end": v(531.7, -213.5) * mm});
            skLineSegment(sketch, "E6.23.9.2", {"start": v(532.76, -211.3) * mm, "end": v(531.7, -211.3) * mm});
            skLineSegment(sketch, "E6.23.9.3", {"start": v(531.7, -211.3) * mm, "end": v(531.7, -213.5) * mm});
            skArc(sketch, "E6.23.10.0", {"start": v(532.76, -237.1) * mm, "mid": v(552.9, -236) * mm, "end": v(532.76, -234.9) * mm});
            skLineSegment(sketch, "E6.23.10.1", {"start": v(532.76, -237.1) * mm, "end": v(531.7, -237.1) * mm});
            skLineSegment(sketch, "E6.23.10.2", {"start": v(532.76, -234.9) * mm, "end": v(531.7, -234.9) * mm});
            skLineSegment(sketch, "E6.23.10.3", {"start": v(531.7, -234.9) * mm, "end": v(531.7, -237.1) * mm});
            skArc(sketch, "E6.23.11.0", {"start": v(532.76, -260.7) * mm, "mid": v(552.9, -259.6) * mm, "end": v(532.76, -258.5) * mm});
            skLineSegment(sketch, "E6.23.11.1", {"start": v(532.76, -260.7) * mm, "end": v(531.7, -260.7) * mm});
            skLineSegment(sketch, "E6.23.11.2", {"start": v(532.76, -258.5) * mm, "end": v(531.7, -258.5) * mm});
            skLineSegment(sketch, "E6.23.11.3", {"start": v(531.7, -258.5) * mm, "end": v(531.7, -260.7) * mm});
            skArc(sketch, "E6.23.12.0", {"start": v(532.76, -284.3) * mm, "mid": v(552.9, -283.2) * mm, "end": v(532.76, -282.1) * mm});
            skLineSegment(sketch, "E6.23.12.1", {"start": v(532.76, -284.3) * mm, "end": v(531.7, -284.3) * mm});
            skLineSegment(sketch, "E6.23.12.2", {"start": v(532.76, -282.1) * mm, "end": v(531.7, -282.1) * mm});
            skLineSegment(sketch, "E6.23.12.3", {"start": v(531.7, -282.1) * mm, "end": v(531.7, -284.3) * mm});
            skArc(sketch, "E6.23.13.0", {"start": v(532.76, -307.9) * mm, "mid": v(552.9, -306.8) * mm, "end": v(532.76, -305.7) * mm});
            skLineSegment(sketch, "E6.23.13.1", {"start": v(532.76, -307.9) * mm, "end": v(531.7, -307.9) * mm});
            skLineSegment(sketch, "E6.23.13.2", {"start": v(532.76, -305.7) * mm, "end": v(531.7, -305.7) * mm});
            skLineSegment(sketch, "E6.23.13.3", {"start": v(531.7, -305.7) * mm, "end": v(531.7, -307.9) * mm});
            skArc(sketch, "E6.24.0.0", {"start": v(556.36, -1.1) * mm, "mid": v(576.5, 0) * mm, "end": v(556.36, 1.1) * mm});
            skLineSegment(sketch, "E6.24.0.1", {"start": v(556.36, -1.1) * mm, "end": v(555.3, -1.1) * mm});
            skLineSegment(sketch, "E6.24.0.2", {"start": v(556.36, 1.1) * mm, "end": v(555.3, 1.1) * mm});
            skLineSegment(sketch, "E6.24.0.3", {"start": v(555.3, 1.1) * mm, "end": v(555.3, -1.1) * mm});
            skArc(sketch, "E6.24.1.0", {"start": v(556.36, -24.7) * mm, "mid": v(576.5, -23.6) * mm, "end": v(556.36, -22.5) * mm});
            skLineSegment(sketch, "E6.24.1.1", {"start": v(556.36, -24.7) * mm, "end": v(555.3, -24.7) * mm});
            skLineSegment(sketch, "E6.24.1.2", {"start": v(556.36, -22.5) * mm, "end": v(555.3, -22.5) * mm});
            skLineSegment(sketch, "E6.24.1.3", {"start": v(555.3, -22.5) * mm, "end": v(555.3, -24.7) * mm});
            skArc(sketch, "E6.24.2.0", {"start": v(556.36, -48.3) * mm, "mid": v(576.5, -47.2) * mm, "end": v(556.36, -46.1) * mm});
            skLineSegment(sketch, "E6.24.2.1", {"start": v(556.36, -48.3) * mm, "end": v(555.3, -48.3) * mm});
            skLineSegment(sketch, "E6.24.2.2", {"start": v(556.36, -46.1) * mm, "end": v(555.3, -46.1) * mm});
            skLineSegment(sketch, "E6.24.2.3", {"start": v(555.3, -46.1) * mm, "end": v(555.3, -48.3) * mm});
            skArc(sketch, "E6.24.3.0", {"start": v(556.36, -71.9) * mm, "mid": v(576.5, -70.8) * mm, "end": v(556.36, -69.7) * mm});
            skLineSegment(sketch, "E6.24.3.1", {"start": v(556.36, -71.9) * mm, "end": v(555.3, -71.9) * mm});
            skLineSegment(sketch, "E6.24.3.2", {"start": v(556.36, -69.7) * mm, "end": v(555.3, -69.7) * mm});
            skLineSegment(sketch, "E6.24.3.3", {"start": v(555.3, -69.7) * mm, "end": v(555.3, -71.9) * mm});
            skArc(sketch, "E6.24.4.0", {"start": v(556.36, -95.5) * mm, "mid": v(576.5, -94.4) * mm, "end": v(556.36, -93.3) * mm});
            skLineSegment(sketch, "E6.24.4.1", {"start": v(556.36, -95.5) * mm, "end": v(555.3, -95.5) * mm});
            skLineSegment(sketch, "E6.24.4.2", {"start": v(556.36, -93.3) * mm, "end": v(555.3, -93.3) * mm});
            skLineSegment(sketch, "E6.24.4.3", {"start": v(555.3, -93.3) * mm, "end": v(555.3, -95.5) * mm});
            skArc(sketch, "E6.24.5.0", {"start": v(556.36, -119.1) * mm, "mid": v(576.5, -118) * mm, "end": v(556.36, -116.9) * mm});
            skLineSegment(sketch, "E6.24.5.1", {"start": v(556.36, -119.1) * mm, "end": v(555.3, -119.1) * mm});
            skLineSegment(sketch, "E6.24.5.2", {"start": v(556.36, -116.9) * mm, "end": v(555.3, -116.9) * mm});
            skLineSegment(sketch, "E6.24.5.3", {"start": v(555.3, -116.9) * mm, "end": v(555.3, -119.1) * mm});
            skArc(sketch, "E6.24.6.0", {"start": v(556.36, -142.7) * mm, "mid": v(576.5, -141.6) * mm, "end": v(556.36, -140.5) * mm});
            skLineSegment(sketch, "E6.24.6.1", {"start": v(556.36, -142.7) * mm, "end": v(555.3, -142.7) * mm});
            skLineSegment(sketch, "E6.24.6.2", {"start": v(556.36, -140.5) * mm, "end": v(555.3, -140.5) * mm});
            skLineSegment(sketch, "E6.24.6.3", {"start": v(555.3, -140.5) * mm, "end": v(555.3, -142.7) * mm});
            skArc(sketch, "E6.24.7.0", {"start": v(556.36, -166.3) * mm, "mid": v(576.5, -165.2) * mm, "end": v(556.36, -164.1) * mm});
            skLineSegment(sketch, "E6.24.7.1", {"start": v(556.36, -166.3) * mm, "end": v(555.3, -166.3) * mm});
            skLineSegment(sketch, "E6.24.7.2", {"start": v(556.36, -164.1) * mm, "end": v(555.3, -164.1) * mm});
            skLineSegment(sketch, "E6.24.7.3", {"start": v(555.3, -164.1) * mm, "end": v(555.3, -166.3) * mm});
            skArc(sketch, "E6.24.8.0", {"start": v(556.36, -189.9) * mm, "mid": v(576.5, -188.8) * mm, "end": v(556.36, -187.7) * mm});
            skLineSegment(sketch, "E6.24.8.1", {"start": v(556.36, -189.9) * mm, "end": v(555.3, -189.9) * mm});
            skLineSegment(sketch, "E6.24.8.2", {"start": v(556.36, -187.7) * mm, "end": v(555.3, -187.7) * mm});
            skLineSegment(sketch, "E6.24.8.3", {"start": v(555.3, -187.7) * mm, "end": v(555.3, -189.9) * mm});
            skArc(sketch, "E6.24.9.0", {"start": v(556.36, -213.5) * mm, "mid": v(576.5, -212.4) * mm, "end": v(556.36, -211.3) * mm});
            skLineSegment(sketch, "E6.24.9.1", {"start": v(556.36, -213.5) * mm, "end": v(555.3, -213.5) * mm});
            skLineSegment(sketch, "E6.24.9.2", {"start": v(556.36, -211.3) * mm, "end": v(555.3, -211.3) * mm});
            skLineSegment(sketch, "E6.24.9.3", {"start": v(555.3, -211.3) * mm, "end": v(555.3, -213.5) * mm});
            skArc(sketch, "E6.24.10.0", {"start": v(556.36, -237.1) * mm, "mid": v(576.5, -236) * mm, "end": v(556.36, -234.9) * mm});
            skLineSegment(sketch, "E6.24.10.1", {"start": v(556.36, -237.1) * mm, "end": v(555.3, -237.1) * mm});
            skLineSegment(sketch, "E6.24.10.2", {"start": v(556.36, -234.9) * mm, "end": v(555.3, -234.9) * mm});
            skLineSegment(sketch, "E6.24.10.3", {"start": v(555.3, -234.9) * mm, "end": v(555.3, -237.1) * mm});
            skArc(sketch, "E6.24.11.0", {"start": v(556.36, -260.7) * mm, "mid": v(576.5, -259.6) * mm, "end": v(556.36, -258.5) * mm});
            skLineSegment(sketch, "E6.24.11.1", {"start": v(556.36, -260.7) * mm, "end": v(555.3, -260.7) * mm});
            skLineSegment(sketch, "E6.24.11.2", {"start": v(556.36, -258.5) * mm, "end": v(555.3, -258.5) * mm});
            skLineSegment(sketch, "E6.24.11.3", {"start": v(555.3, -258.5) * mm, "end": v(555.3, -260.7) * mm});
            skArc(sketch, "E6.24.12.0", {"start": v(556.36, -284.3) * mm, "mid": v(576.5, -283.2) * mm, "end": v(556.36, -282.1) * mm});
            skLineSegment(sketch, "E6.24.12.1", {"start": v(556.36, -284.3) * mm, "end": v(555.3, -284.3) * mm});
            skLineSegment(sketch, "E6.24.12.2", {"start": v(556.36, -282.1) * mm, "end": v(555.3, -282.1) * mm});
            skLineSegment(sketch, "E6.24.12.3", {"start": v(555.3, -282.1) * mm, "end": v(555.3, -284.3) * mm});
            skArc(sketch, "E6.24.13.0", {"start": v(556.36, -307.9) * mm, "mid": v(576.5, -306.8) * mm, "end": v(556.36, -305.7) * mm});
            skLineSegment(sketch, "E6.24.13.1", {"start": v(556.36, -307.9) * mm, "end": v(555.3, -307.9) * mm});
            skLineSegment(sketch, "E6.24.13.2", {"start": v(556.36, -305.7) * mm, "end": v(555.3, -305.7) * mm});
            skLineSegment(sketch, "E6.24.13.3", {"start": v(555.3, -305.7) * mm, "end": v(555.3, -307.9) * mm});
            skLineSegment(sketch, "E6.direction1", {"start": v(-10.04, -1.1) * mm, "end": v(13.56, -1.1) * mm, "construction": true});
            skLineSegment(sketch, "E6.direction2", {"start": v(-10.04, -1.1) * mm, "end": v(-10.04, -24.7) * mm, "construction": true});
            skCircle(sketch, "E7.0.1.0", {"center": v(0, -23.6) * mm, "radius": 11.65 * mm, "construction": true});
            skCircle(sketch, "E7.1.0.0", {"center": v(23.6, 0) * mm, "radius": 11.65 * mm, "construction": true});
            skCircle(sketch, "E7.1.1.0", {"center": v(23.6, -23.6) * mm, "radius": 11.65 * mm, "construction": true});
            skLineSegment(sketch, "E7.direction1", {"start": v(0, 0) * mm, "end": v(23.6, 0) * mm, "construction": true});
            skLineSegment(sketch, "E7.direction2", {"start": v(0, 0) * mm, "end": v(0, -23.6) * mm, "construction": true});
            skSolve(sketch);
        }
        {
            var Q0;
            Q0 = qSketchRegion(id + "F0", true);
            extrude(context, id + "F1", {"entities" : qUnion([Q0]), "depth" : 5 * mm});
        }
    });
